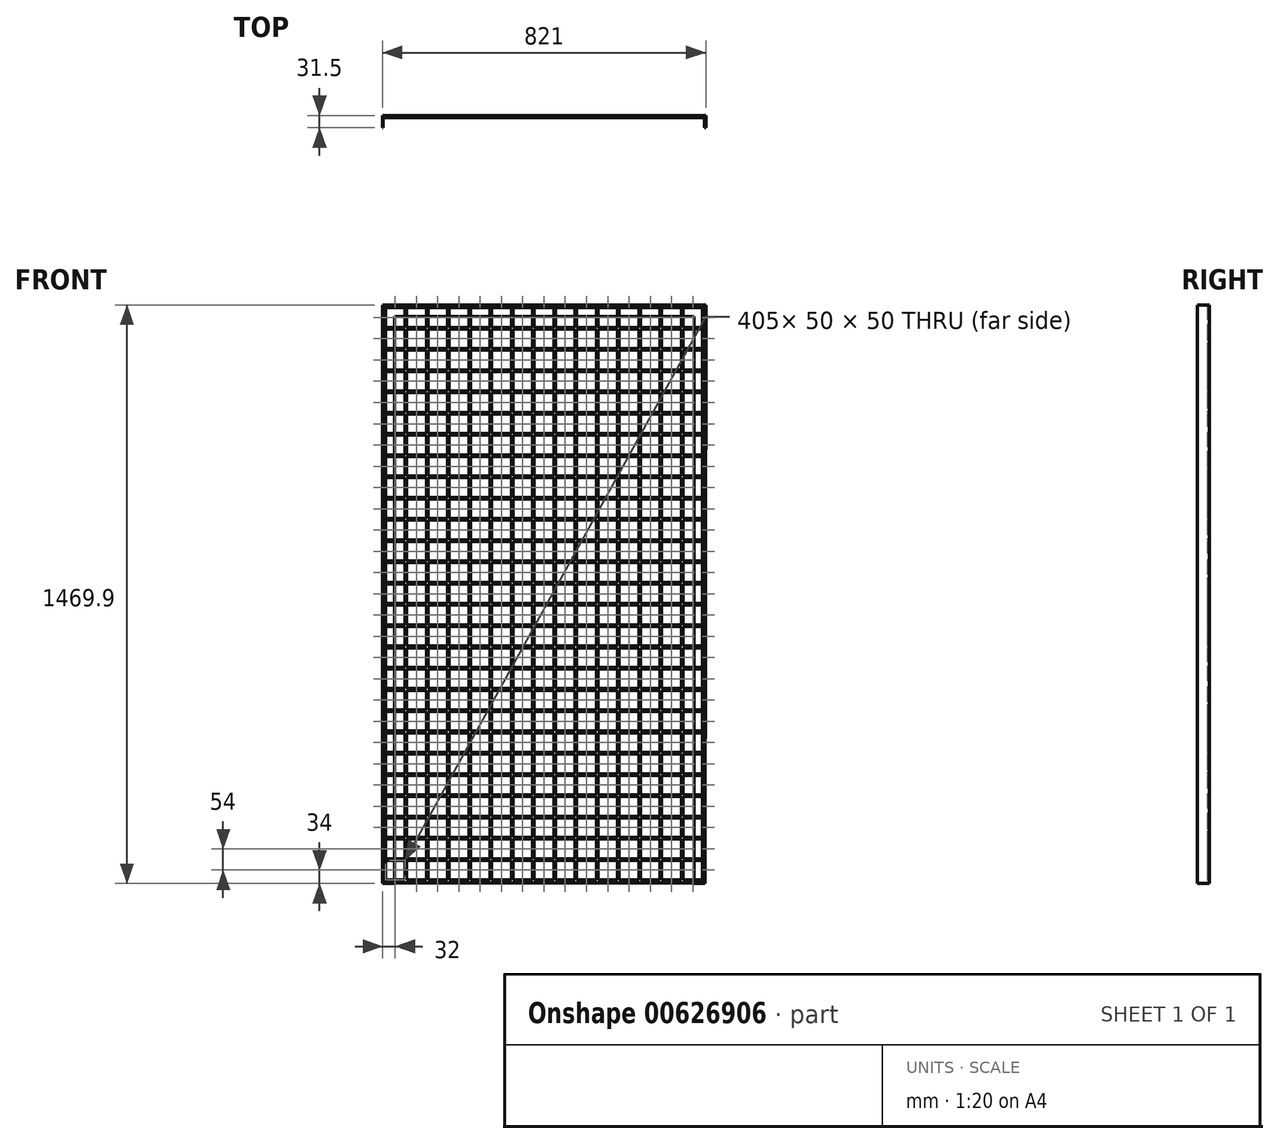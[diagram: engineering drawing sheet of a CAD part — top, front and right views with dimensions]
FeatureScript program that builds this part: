
annotation { "Feature Type Name" : "Feature", "Feature Type Description" : "" }
export const myFeature = defineFeature(function(context is Context, id is Id, definition is map)
    precondition{}
    {
        {
            var Q0;
            Q0=qCreatedBy(makeId("Front.planeOp"),FACE);
            var sketch = newSketch(context, id + "F0", { "sketchPlane" : qUnion([Q0])});
            skLineSegment(sketch, "E0.bottom", {"start": v(0, 0) * mm, "end": v(815, 0) * mm});
            skLineSegment(sketch, "E0.top", {"start": v(0, -1465) * mm, "end": v(815, -1465) * mm});
            skLineSegment(sketch, "E0.left", {"start": v(0, 0) * mm, "end": v(0, -1465) * mm});
            skLineSegment(sketch, "E0.right", {"start": v(815, 0) * mm, "end": v(815, -1465) * mm});
            skLineSegment(sketch, "E1.bottom", {"start": v(4, -4) * mm, "end": v(54, -4) * mm});
            skLineSegment(sketch, "E1.top", {"start": v(4, -54) * mm, "end": v(54, -54) * mm});
            skLineSegment(sketch, "E1.left", {"start": v(4, -4) * mm, "end": v(4, -54) * mm});
            skLineSegment(sketch, "E1.right", {"start": v(54, -4) * mm, "end": v(54, -54) * mm});
            skLineSegment(sketch, "E2.0.1.0", {"start": v(4, -58) * mm, "end": v(54, -58) * mm});
            skLineSegment(sketch, "E2.0.1.1", {"start": v(54, -58) * mm, "end": v(54, -108) * mm});
            skLineSegment(sketch, "E2.0.1.2", {"start": v(4, -108) * mm, "end": v(54, -108) * mm});
            skLineSegment(sketch, "E2.0.1.3", {"start": v(4, -58) * mm, "end": v(4, -108) * mm});
            skLineSegment(sketch, "E2.0.2.0", {"start": v(4, -112) * mm, "end": v(54, -112) * mm});
            skLineSegment(sketch, "E2.0.2.1", {"start": v(54, -112) * mm, "end": v(54, -162) * mm});
            skLineSegment(sketch, "E2.0.2.2", {"start": v(4, -162) * mm, "end": v(54, -162) * mm});
            skLineSegment(sketch, "E2.0.2.3", {"start": v(4, -112) * mm, "end": v(4, -162) * mm});
            skLineSegment(sketch, "E2.0.3.0", {"start": v(4, -166) * mm, "end": v(54, -166) * mm});
            skLineSegment(sketch, "E2.0.3.1", {"start": v(54, -166) * mm, "end": v(54, -216) * mm});
            skLineSegment(sketch, "E2.0.3.2", {"start": v(4, -216) * mm, "end": v(54, -216) * mm});
            skLineSegment(sketch, "E2.0.3.3", {"start": v(4, -166) * mm, "end": v(4, -216) * mm});
            skLineSegment(sketch, "E2.0.4.0", {"start": v(4, -220) * mm, "end": v(54, -220) * mm});
            skLineSegment(sketch, "E2.0.4.1", {"start": v(54, -220) * mm, "end": v(54, -270) * mm});
            skLineSegment(sketch, "E2.0.4.2", {"start": v(4, -270) * mm, "end": v(54, -270) * mm});
            skLineSegment(sketch, "E2.0.4.3", {"start": v(4, -220) * mm, "end": v(4, -270) * mm});
            skLineSegment(sketch, "E2.0.5.0", {"start": v(4, -274) * mm, "end": v(54, -274) * mm});
            skLineSegment(sketch, "E2.0.5.1", {"start": v(54, -274) * mm, "end": v(54, -324) * mm});
            skLineSegment(sketch, "E2.0.5.2", {"start": v(4, -324) * mm, "end": v(54, -324) * mm});
            skLineSegment(sketch, "E2.0.5.3", {"start": v(4, -274) * mm, "end": v(4, -324) * mm});
            skLineSegment(sketch, "E2.0.6.0", {"start": v(4, -328) * mm, "end": v(54, -328) * mm});
            skLineSegment(sketch, "E2.0.6.1", {"start": v(54, -328) * mm, "end": v(54, -378) * mm});
            skLineSegment(sketch, "E2.0.6.2", {"start": v(4, -378) * mm, "end": v(54, -378) * mm});
            skLineSegment(sketch, "E2.0.6.3", {"start": v(4, -328) * mm, "end": v(4, -378) * mm});
            skLineSegment(sketch, "E2.0.7.0", {"start": v(4, -382) * mm, "end": v(54, -382) * mm});
            skLineSegment(sketch, "E2.0.7.1", {"start": v(54, -382) * mm, "end": v(54, -432) * mm});
            skLineSegment(sketch, "E2.0.7.2", {"start": v(4, -432) * mm, "end": v(54, -432) * mm});
            skLineSegment(sketch, "E2.0.7.3", {"start": v(4, -382) * mm, "end": v(4, -432) * mm});
            skLineSegment(sketch, "E2.0.8.0", {"start": v(4, -436) * mm, "end": v(54, -436) * mm});
            skLineSegment(sketch, "E2.0.8.1", {"start": v(54, -436) * mm, "end": v(54, -486) * mm});
            skLineSegment(sketch, "E2.0.8.2", {"start": v(4, -486) * mm, "end": v(54, -486) * mm});
            skLineSegment(sketch, "E2.0.8.3", {"start": v(4, -436) * mm, "end": v(4, -486) * mm});
            skLineSegment(sketch, "E2.0.9.0", {"start": v(4, -490) * mm, "end": v(54, -490) * mm});
            skLineSegment(sketch, "E2.0.9.1", {"start": v(54, -490) * mm, "end": v(54, -540) * mm});
            skLineSegment(sketch, "E2.0.9.2", {"start": v(4, -540) * mm, "end": v(54, -540) * mm});
            skLineSegment(sketch, "E2.0.9.3", {"start": v(4, -490) * mm, "end": v(4, -540) * mm});
            skLineSegment(sketch, "E2.0.10.0", {"start": v(4, -544) * mm, "end": v(54, -544) * mm});
            skLineSegment(sketch, "E2.0.10.1", {"start": v(54, -544) * mm, "end": v(54, -594) * mm});
            skLineSegment(sketch, "E2.0.10.2", {"start": v(4, -594) * mm, "end": v(54, -594) * mm});
            skLineSegment(sketch, "E2.0.10.3", {"start": v(4, -544) * mm, "end": v(4, -594) * mm});
            skLineSegment(sketch, "E2.0.11.0", {"start": v(4, -598) * mm, "end": v(54, -598) * mm});
            skLineSegment(sketch, "E2.0.11.1", {"start": v(54, -598) * mm, "end": v(54, -648) * mm});
            skLineSegment(sketch, "E2.0.11.2", {"start": v(4, -648) * mm, "end": v(54, -648) * mm});
            skLineSegment(sketch, "E2.0.11.3", {"start": v(4, -598) * mm, "end": v(4, -648) * mm});
            skLineSegment(sketch, "E2.0.12.0", {"start": v(4, -652) * mm, "end": v(54, -652) * mm});
            skLineSegment(sketch, "E2.0.12.1", {"start": v(54, -652) * mm, "end": v(54, -702) * mm});
            skLineSegment(sketch, "E2.0.12.2", {"start": v(4, -702) * mm, "end": v(54, -702) * mm});
            skLineSegment(sketch, "E2.0.12.3", {"start": v(4, -652) * mm, "end": v(4, -702) * mm});
            skLineSegment(sketch, "E2.0.13.0", {"start": v(4, -706) * mm, "end": v(54, -706) * mm});
            skLineSegment(sketch, "E2.0.13.1", {"start": v(54, -706) * mm, "end": v(54, -756) * mm});
            skLineSegment(sketch, "E2.0.13.2", {"start": v(4, -756) * mm, "end": v(54, -756) * mm});
            skLineSegment(sketch, "E2.0.13.3", {"start": v(4, -706) * mm, "end": v(4, -756) * mm});
            skLineSegment(sketch, "E2.0.14.0", {"start": v(4, -760) * mm, "end": v(54, -760) * mm});
            skLineSegment(sketch, "E2.0.14.1", {"start": v(54, -760) * mm, "end": v(54, -810) * mm});
            skLineSegment(sketch, "E2.0.14.2", {"start": v(4, -810) * mm, "end": v(54, -810) * mm});
            skLineSegment(sketch, "E2.0.14.3", {"start": v(4, -760) * mm, "end": v(4, -810) * mm});
            skLineSegment(sketch, "E2.0.15.0", {"start": v(4, -814) * mm, "end": v(54, -814) * mm});
            skLineSegment(sketch, "E2.0.15.1", {"start": v(54, -814) * mm, "end": v(54, -864) * mm});
            skLineSegment(sketch, "E2.0.15.2", {"start": v(4, -864) * mm, "end": v(54, -864) * mm});
            skLineSegment(sketch, "E2.0.15.3", {"start": v(4, -814) * mm, "end": v(4, -864) * mm});
            skLineSegment(sketch, "E2.0.16.0", {"start": v(4, -868) * mm, "end": v(54, -868) * mm});
            skLineSegment(sketch, "E2.0.16.1", {"start": v(54, -868) * mm, "end": v(54, -918) * mm});
            skLineSegment(sketch, "E2.0.16.2", {"start": v(4, -918) * mm, "end": v(54, -918) * mm});
            skLineSegment(sketch, "E2.0.16.3", {"start": v(4, -868) * mm, "end": v(4, -918) * mm});
            skLineSegment(sketch, "E2.0.17.0", {"start": v(4, -922) * mm, "end": v(54, -922) * mm});
            skLineSegment(sketch, "E2.0.17.1", {"start": v(54, -922) * mm, "end": v(54, -972) * mm});
            skLineSegment(sketch, "E2.0.17.2", {"start": v(4, -972) * mm, "end": v(54, -972) * mm});
            skLineSegment(sketch, "E2.0.17.3", {"start": v(4, -922) * mm, "end": v(4, -972) * mm});
            skLineSegment(sketch, "E2.0.18.0", {"start": v(4, -976) * mm, "end": v(54, -976) * mm});
            skLineSegment(sketch, "E2.0.18.1", {"start": v(54, -976) * mm, "end": v(54, -1026) * mm});
            skLineSegment(sketch, "E2.0.18.2", {"start": v(4, -1026) * mm, "end": v(54, -1026) * mm});
            skLineSegment(sketch, "E2.0.18.3", {"start": v(4, -976) * mm, "end": v(4, -1026) * mm});
            skLineSegment(sketch, "E2.0.19.0", {"start": v(4, -1030) * mm, "end": v(54, -1030) * mm});
            skLineSegment(sketch, "E2.0.19.1", {"start": v(54, -1030) * mm, "end": v(54, -1080) * mm});
            skLineSegment(sketch, "E2.0.19.2", {"start": v(4, -1080) * mm, "end": v(54, -1080) * mm});
            skLineSegment(sketch, "E2.0.19.3", {"start": v(4, -1030) * mm, "end": v(4, -1080) * mm});
            skLineSegment(sketch, "E2.0.20.0", {"start": v(4, -1084) * mm, "end": v(54, -1084) * mm});
            skLineSegment(sketch, "E2.0.20.1", {"start": v(54, -1084) * mm, "end": v(54, -1134) * mm});
            skLineSegment(sketch, "E2.0.20.2", {"start": v(4, -1134) * mm, "end": v(54, -1134) * mm});
            skLineSegment(sketch, "E2.0.20.3", {"start": v(4, -1084) * mm, "end": v(4, -1134) * mm});
            skLineSegment(sketch, "E2.0.21.0", {"start": v(4, -1138) * mm, "end": v(54, -1138) * mm});
            skLineSegment(sketch, "E2.0.21.1", {"start": v(54, -1138) * mm, "end": v(54, -1188) * mm});
            skLineSegment(sketch, "E2.0.21.2", {"start": v(4, -1188) * mm, "end": v(54, -1188) * mm});
            skLineSegment(sketch, "E2.0.21.3", {"start": v(4, -1138) * mm, "end": v(4, -1188) * mm});
            skLineSegment(sketch, "E2.0.22.0", {"start": v(4, -1192) * mm, "end": v(54, -1192) * mm});
            skLineSegment(sketch, "E2.0.22.1", {"start": v(54, -1192) * mm, "end": v(54, -1242) * mm});
            skLineSegment(sketch, "E2.0.22.2", {"start": v(4, -1242) * mm, "end": v(54, -1242) * mm});
            skLineSegment(sketch, "E2.0.22.3", {"start": v(4, -1192) * mm, "end": v(4, -1242) * mm});
            skLineSegment(sketch, "E2.0.23.0", {"start": v(4, -1246) * mm, "end": v(54, -1246) * mm});
            skLineSegment(sketch, "E2.0.23.1", {"start": v(54, -1246) * mm, "end": v(54, -1296) * mm});
            skLineSegment(sketch, "E2.0.23.2", {"start": v(4, -1296) * mm, "end": v(54, -1296) * mm});
            skLineSegment(sketch, "E2.0.23.3", {"start": v(4, -1246) * mm, "end": v(4, -1296) * mm});
            skLineSegment(sketch, "E2.0.24.0", {"start": v(4, -1300) * mm, "end": v(54, -1300) * mm});
            skLineSegment(sketch, "E2.0.24.1", {"start": v(54, -1300) * mm, "end": v(54, -1350) * mm});
            skLineSegment(sketch, "E2.0.24.2", {"start": v(4, -1350) * mm, "end": v(54, -1350) * mm});
            skLineSegment(sketch, "E2.0.24.3", {"start": v(4, -1300) * mm, "end": v(4, -1350) * mm});
            skLineSegment(sketch, "E2.1.0.0", {"start": v(58, -4) * mm, "end": v(108, -4) * mm});
            skLineSegment(sketch, "E2.1.0.1", {"start": v(108, -4) * mm, "end": v(108, -54) * mm});
            skLineSegment(sketch, "E2.1.0.2", {"start": v(58, -54) * mm, "end": v(108, -54) * mm});
            skLineSegment(sketch, "E2.1.0.3", {"start": v(58, -4) * mm, "end": v(58, -54) * mm});
            skLineSegment(sketch, "E2.1.1.0", {"start": v(58, -58) * mm, "end": v(108, -58) * mm});
            skLineSegment(sketch, "E2.1.1.1", {"start": v(108, -58) * mm, "end": v(108, -108) * mm});
            skLineSegment(sketch, "E2.1.1.2", {"start": v(58, -108) * mm, "end": v(108, -108) * mm});
            skLineSegment(sketch, "E2.1.1.3", {"start": v(58, -58) * mm, "end": v(58, -108) * mm});
            skLineSegment(sketch, "E2.1.2.0", {"start": v(58, -112) * mm, "end": v(108, -112) * mm});
            skLineSegment(sketch, "E2.1.2.1", {"start": v(108, -112) * mm, "end": v(108, -162) * mm});
            skLineSegment(sketch, "E2.1.2.2", {"start": v(58, -162) * mm, "end": v(108, -162) * mm});
            skLineSegment(sketch, "E2.1.2.3", {"start": v(58, -112) * mm, "end": v(58, -162) * mm});
            skLineSegment(sketch, "E2.1.3.0", {"start": v(58, -166) * mm, "end": v(108, -166) * mm});
            skLineSegment(sketch, "E2.1.3.1", {"start": v(108, -166) * mm, "end": v(108, -216) * mm});
            skLineSegment(sketch, "E2.1.3.2", {"start": v(58, -216) * mm, "end": v(108, -216) * mm});
            skLineSegment(sketch, "E2.1.3.3", {"start": v(58, -166) * mm, "end": v(58, -216) * mm});
            skLineSegment(sketch, "E2.1.4.0", {"start": v(58, -220) * mm, "end": v(108, -220) * mm});
            skLineSegment(sketch, "E2.1.4.1", {"start": v(108, -220) * mm, "end": v(108, -270) * mm});
            skLineSegment(sketch, "E2.1.4.2", {"start": v(58, -270) * mm, "end": v(108, -270) * mm});
            skLineSegment(sketch, "E2.1.4.3", {"start": v(58, -220) * mm, "end": v(58, -270) * mm});
            skLineSegment(sketch, "E2.1.5.0", {"start": v(58, -274) * mm, "end": v(108, -274) * mm});
            skLineSegment(sketch, "E2.1.5.1", {"start": v(108, -274) * mm, "end": v(108, -324) * mm});
            skLineSegment(sketch, "E2.1.5.2", {"start": v(58, -324) * mm, "end": v(108, -324) * mm});
            skLineSegment(sketch, "E2.1.5.3", {"start": v(58, -274) * mm, "end": v(58, -324) * mm});
            skLineSegment(sketch, "E2.1.6.0", {"start": v(58, -328) * mm, "end": v(108, -328) * mm});
            skLineSegment(sketch, "E2.1.6.1", {"start": v(108, -328) * mm, "end": v(108, -378) * mm});
            skLineSegment(sketch, "E2.1.6.2", {"start": v(58, -378) * mm, "end": v(108, -378) * mm});
            skLineSegment(sketch, "E2.1.6.3", {"start": v(58, -328) * mm, "end": v(58, -378) * mm});
            skLineSegment(sketch, "E2.1.7.0", {"start": v(58, -382) * mm, "end": v(108, -382) * mm});
            skLineSegment(sketch, "E2.1.7.1", {"start": v(108, -382) * mm, "end": v(108, -432) * mm});
            skLineSegment(sketch, "E2.1.7.2", {"start": v(58, -432) * mm, "end": v(108, -432) * mm});
            skLineSegment(sketch, "E2.1.7.3", {"start": v(58, -382) * mm, "end": v(58, -432) * mm});
            skLineSegment(sketch, "E2.1.8.0", {"start": v(58, -436) * mm, "end": v(108, -436) * mm});
            skLineSegment(sketch, "E2.1.8.1", {"start": v(108, -436) * mm, "end": v(108, -486) * mm});
            skLineSegment(sketch, "E2.1.8.2", {"start": v(58, -486) * mm, "end": v(108, -486) * mm});
            skLineSegment(sketch, "E2.1.8.3", {"start": v(58, -436) * mm, "end": v(58, -486) * mm});
            skLineSegment(sketch, "E2.1.9.0", {"start": v(58, -490) * mm, "end": v(108, -490) * mm});
            skLineSegment(sketch, "E2.1.9.1", {"start": v(108, -490) * mm, "end": v(108, -540) * mm});
            skLineSegment(sketch, "E2.1.9.2", {"start": v(58, -540) * mm, "end": v(108, -540) * mm});
            skLineSegment(sketch, "E2.1.9.3", {"start": v(58, -490) * mm, "end": v(58, -540) * mm});
            skLineSegment(sketch, "E2.1.10.0", {"start": v(58, -544) * mm, "end": v(108, -544) * mm});
            skLineSegment(sketch, "E2.1.10.1", {"start": v(108, -544) * mm, "end": v(108, -594) * mm});
            skLineSegment(sketch, "E2.1.10.2", {"start": v(58, -594) * mm, "end": v(108, -594) * mm});
            skLineSegment(sketch, "E2.1.10.3", {"start": v(58, -544) * mm, "end": v(58, -594) * mm});
            skLineSegment(sketch, "E2.1.11.0", {"start": v(58, -598) * mm, "end": v(108, -598) * mm});
            skLineSegment(sketch, "E2.1.11.1", {"start": v(108, -598) * mm, "end": v(108, -648) * mm});
            skLineSegment(sketch, "E2.1.11.2", {"start": v(58, -648) * mm, "end": v(108, -648) * mm});
            skLineSegment(sketch, "E2.1.11.3", {"start": v(58, -598) * mm, "end": v(58, -648) * mm});
            skLineSegment(sketch, "E2.1.12.0", {"start": v(58, -652) * mm, "end": v(108, -652) * mm});
            skLineSegment(sketch, "E2.1.12.1", {"start": v(108, -652) * mm, "end": v(108, -702) * mm});
            skLineSegment(sketch, "E2.1.12.2", {"start": v(58, -702) * mm, "end": v(108, -702) * mm});
            skLineSegment(sketch, "E2.1.12.3", {"start": v(58, -652) * mm, "end": v(58, -702) * mm});
            skLineSegment(sketch, "E2.1.13.0", {"start": v(58, -706) * mm, "end": v(108, -706) * mm});
            skLineSegment(sketch, "E2.1.13.1", {"start": v(108, -706) * mm, "end": v(108, -756) * mm});
            skLineSegment(sketch, "E2.1.13.2", {"start": v(58, -756) * mm, "end": v(108, -756) * mm});
            skLineSegment(sketch, "E2.1.13.3", {"start": v(58, -706) * mm, "end": v(58, -756) * mm});
            skLineSegment(sketch, "E2.1.14.0", {"start": v(58, -760) * mm, "end": v(108, -760) * mm});
            skLineSegment(sketch, "E2.1.14.1", {"start": v(108, -760) * mm, "end": v(108, -810) * mm});
            skLineSegment(sketch, "E2.1.14.2", {"start": v(58, -810) * mm, "end": v(108, -810) * mm});
            skLineSegment(sketch, "E2.1.14.3", {"start": v(58, -760) * mm, "end": v(58, -810) * mm});
            skLineSegment(sketch, "E2.1.15.0", {"start": v(58, -814) * mm, "end": v(108, -814) * mm});
            skLineSegment(sketch, "E2.1.15.1", {"start": v(108, -814) * mm, "end": v(108, -864) * mm});
            skLineSegment(sketch, "E2.1.15.2", {"start": v(58, -864) * mm, "end": v(108, -864) * mm});
            skLineSegment(sketch, "E2.1.15.3", {"start": v(58, -814) * mm, "end": v(58, -864) * mm});
            skLineSegment(sketch, "E2.1.16.0", {"start": v(58, -868) * mm, "end": v(108, -868) * mm});
            skLineSegment(sketch, "E2.1.16.1", {"start": v(108, -868) * mm, "end": v(108, -918) * mm});
            skLineSegment(sketch, "E2.1.16.2", {"start": v(58, -918) * mm, "end": v(108, -918) * mm});
            skLineSegment(sketch, "E2.1.16.3", {"start": v(58, -868) * mm, "end": v(58, -918) * mm});
            skLineSegment(sketch, "E2.1.17.0", {"start": v(58, -922) * mm, "end": v(108, -922) * mm});
            skLineSegment(sketch, "E2.1.17.1", {"start": v(108, -922) * mm, "end": v(108, -972) * mm});
            skLineSegment(sketch, "E2.1.17.2", {"start": v(58, -972) * mm, "end": v(108, -972) * mm});
            skLineSegment(sketch, "E2.1.17.3", {"start": v(58, -922) * mm, "end": v(58, -972) * mm});
            skLineSegment(sketch, "E2.1.18.0", {"start": v(58, -976) * mm, "end": v(108, -976) * mm});
            skLineSegment(sketch, "E2.1.18.1", {"start": v(108, -976) * mm, "end": v(108, -1026) * mm});
            skLineSegment(sketch, "E2.1.18.2", {"start": v(58, -1026) * mm, "end": v(108, -1026) * mm});
            skLineSegment(sketch, "E2.1.18.3", {"start": v(58, -976) * mm, "end": v(58, -1026) * mm});
            skLineSegment(sketch, "E2.1.19.0", {"start": v(58, -1030) * mm, "end": v(108, -1030) * mm});
            skLineSegment(sketch, "E2.1.19.1", {"start": v(108, -1030) * mm, "end": v(108, -1080) * mm});
            skLineSegment(sketch, "E2.1.19.2", {"start": v(58, -1080) * mm, "end": v(108, -1080) * mm});
            skLineSegment(sketch, "E2.1.19.3", {"start": v(58, -1030) * mm, "end": v(58, -1080) * mm});
            skLineSegment(sketch, "E2.1.20.0", {"start": v(58, -1084) * mm, "end": v(108, -1084) * mm});
            skLineSegment(sketch, "E2.1.20.1", {"start": v(108, -1084) * mm, "end": v(108, -1134) * mm});
            skLineSegment(sketch, "E2.1.20.2", {"start": v(58, -1134) * mm, "end": v(108, -1134) * mm});
            skLineSegment(sketch, "E2.1.20.3", {"start": v(58, -1084) * mm, "end": v(58, -1134) * mm});
            skLineSegment(sketch, "E2.1.21.0", {"start": v(58, -1138) * mm, "end": v(108, -1138) * mm});
            skLineSegment(sketch, "E2.1.21.1", {"start": v(108, -1138) * mm, "end": v(108, -1188) * mm});
            skLineSegment(sketch, "E2.1.21.2", {"start": v(58, -1188) * mm, "end": v(108, -1188) * mm});
            skLineSegment(sketch, "E2.1.21.3", {"start": v(58, -1138) * mm, "end": v(58, -1188) * mm});
            skLineSegment(sketch, "E2.1.22.0", {"start": v(58, -1192) * mm, "end": v(108, -1192) * mm});
            skLineSegment(sketch, "E2.1.22.1", {"start": v(108, -1192) * mm, "end": v(108, -1242) * mm});
            skLineSegment(sketch, "E2.1.22.2", {"start": v(58, -1242) * mm, "end": v(108, -1242) * mm});
            skLineSegment(sketch, "E2.1.22.3", {"start": v(58, -1192) * mm, "end": v(58, -1242) * mm});
            skLineSegment(sketch, "E2.1.23.0", {"start": v(58, -1246) * mm, "end": v(108, -1246) * mm});
            skLineSegment(sketch, "E2.1.23.1", {"start": v(108, -1246) * mm, "end": v(108, -1296) * mm});
            skLineSegment(sketch, "E2.1.23.2", {"start": v(58, -1296) * mm, "end": v(108, -1296) * mm});
            skLineSegment(sketch, "E2.1.23.3", {"start": v(58, -1246) * mm, "end": v(58, -1296) * mm});
            skLineSegment(sketch, "E2.1.24.0", {"start": v(58, -1300) * mm, "end": v(108, -1300) * mm});
            skLineSegment(sketch, "E2.1.24.1", {"start": v(108, -1300) * mm, "end": v(108, -1350) * mm});
            skLineSegment(sketch, "E2.1.24.2", {"start": v(58, -1350) * mm, "end": v(108, -1350) * mm});
            skLineSegment(sketch, "E2.1.24.3", {"start": v(58, -1300) * mm, "end": v(58, -1350) * mm});
            skLineSegment(sketch, "E2.2.0.0", {"start": v(112, -4) * mm, "end": v(162, -4) * mm});
            skLineSegment(sketch, "E2.2.0.1", {"start": v(162, -4) * mm, "end": v(162, -54) * mm});
            skLineSegment(sketch, "E2.2.0.2", {"start": v(112, -54) * mm, "end": v(162, -54) * mm});
            skLineSegment(sketch, "E2.2.0.3", {"start": v(112, -4) * mm, "end": v(112, -54) * mm});
            skLineSegment(sketch, "E2.2.1.0", {"start": v(112, -58) * mm, "end": v(162, -58) * mm});
            skLineSegment(sketch, "E2.2.1.1", {"start": v(162, -58) * mm, "end": v(162, -108) * mm});
            skLineSegment(sketch, "E2.2.1.2", {"start": v(112, -108) * mm, "end": v(162, -108) * mm});
            skLineSegment(sketch, "E2.2.1.3", {"start": v(112, -58) * mm, "end": v(112, -108) * mm});
            skLineSegment(sketch, "E2.2.2.0", {"start": v(112, -112) * mm, "end": v(162, -112) * mm});
            skLineSegment(sketch, "E2.2.2.1", {"start": v(162, -112) * mm, "end": v(162, -162) * mm});
            skLineSegment(sketch, "E2.2.2.2", {"start": v(112, -162) * mm, "end": v(162, -162) * mm});
            skLineSegment(sketch, "E2.2.2.3", {"start": v(112, -112) * mm, "end": v(112, -162) * mm});
            skLineSegment(sketch, "E2.2.3.0", {"start": v(112, -166) * mm, "end": v(162, -166) * mm});
            skLineSegment(sketch, "E2.2.3.1", {"start": v(162, -166) * mm, "end": v(162, -216) * mm});
            skLineSegment(sketch, "E2.2.3.2", {"start": v(112, -216) * mm, "end": v(162, -216) * mm});
            skLineSegment(sketch, "E2.2.3.3", {"start": v(112, -166) * mm, "end": v(112, -216) * mm});
            skLineSegment(sketch, "E2.2.4.0", {"start": v(112, -220) * mm, "end": v(162, -220) * mm});
            skLineSegment(sketch, "E2.2.4.1", {"start": v(162, -220) * mm, "end": v(162, -270) * mm});
            skLineSegment(sketch, "E2.2.4.2", {"start": v(112, -270) * mm, "end": v(162, -270) * mm});
            skLineSegment(sketch, "E2.2.4.3", {"start": v(112, -220) * mm, "end": v(112, -270) * mm});
            skLineSegment(sketch, "E2.2.5.0", {"start": v(112, -274) * mm, "end": v(162, -274) * mm});
            skLineSegment(sketch, "E2.2.5.1", {"start": v(162, -274) * mm, "end": v(162, -324) * mm});
            skLineSegment(sketch, "E2.2.5.2", {"start": v(112, -324) * mm, "end": v(162, -324) * mm});
            skLineSegment(sketch, "E2.2.5.3", {"start": v(112, -274) * mm, "end": v(112, -324) * mm});
            skLineSegment(sketch, "E2.2.6.0", {"start": v(112, -328) * mm, "end": v(162, -328) * mm});
            skLineSegment(sketch, "E2.2.6.1", {"start": v(162, -328) * mm, "end": v(162, -378) * mm});
            skLineSegment(sketch, "E2.2.6.2", {"start": v(112, -378) * mm, "end": v(162, -378) * mm});
            skLineSegment(sketch, "E2.2.6.3", {"start": v(112, -328) * mm, "end": v(112, -378) * mm});
            skLineSegment(sketch, "E2.2.7.0", {"start": v(112, -382) * mm, "end": v(162, -382) * mm});
            skLineSegment(sketch, "E2.2.7.1", {"start": v(162, -382) * mm, "end": v(162, -432) * mm});
            skLineSegment(sketch, "E2.2.7.2", {"start": v(112, -432) * mm, "end": v(162, -432) * mm});
            skLineSegment(sketch, "E2.2.7.3", {"start": v(112, -382) * mm, "end": v(112, -432) * mm});
            skLineSegment(sketch, "E2.2.8.0", {"start": v(112, -436) * mm, "end": v(162, -436) * mm});
            skLineSegment(sketch, "E2.2.8.1", {"start": v(162, -436) * mm, "end": v(162, -486) * mm});
            skLineSegment(sketch, "E2.2.8.2", {"start": v(112, -486) * mm, "end": v(162, -486) * mm});
            skLineSegment(sketch, "E2.2.8.3", {"start": v(112, -436) * mm, "end": v(112, -486) * mm});
            skLineSegment(sketch, "E2.2.9.0", {"start": v(112, -490) * mm, "end": v(162, -490) * mm});
            skLineSegment(sketch, "E2.2.9.1", {"start": v(162, -490) * mm, "end": v(162, -540) * mm});
            skLineSegment(sketch, "E2.2.9.2", {"start": v(112, -540) * mm, "end": v(162, -540) * mm});
            skLineSegment(sketch, "E2.2.9.3", {"start": v(112, -490) * mm, "end": v(112, -540) * mm});
            skLineSegment(sketch, "E2.2.10.0", {"start": v(112, -544) * mm, "end": v(162, -544) * mm});
            skLineSegment(sketch, "E2.2.10.1", {"start": v(162, -544) * mm, "end": v(162, -594) * mm});
            skLineSegment(sketch, "E2.2.10.2", {"start": v(112, -594) * mm, "end": v(162, -594) * mm});
            skLineSegment(sketch, "E2.2.10.3", {"start": v(112, -544) * mm, "end": v(112, -594) * mm});
            skLineSegment(sketch, "E2.2.11.0", {"start": v(112, -598) * mm, "end": v(162, -598) * mm});
            skLineSegment(sketch, "E2.2.11.1", {"start": v(162, -598) * mm, "end": v(162, -648) * mm});
            skLineSegment(sketch, "E2.2.11.2", {"start": v(112, -648) * mm, "end": v(162, -648) * mm});
            skLineSegment(sketch, "E2.2.11.3", {"start": v(112, -598) * mm, "end": v(112, -648) * mm});
            skLineSegment(sketch, "E2.2.12.0", {"start": v(112, -652) * mm, "end": v(162, -652) * mm});
            skLineSegment(sketch, "E2.2.12.1", {"start": v(162, -652) * mm, "end": v(162, -702) * mm});
            skLineSegment(sketch, "E2.2.12.2", {"start": v(112, -702) * mm, "end": v(162, -702) * mm});
            skLineSegment(sketch, "E2.2.12.3", {"start": v(112, -652) * mm, "end": v(112, -702) * mm});
            skLineSegment(sketch, "E2.2.13.0", {"start": v(112, -706) * mm, "end": v(162, -706) * mm});
            skLineSegment(sketch, "E2.2.13.1", {"start": v(162, -706) * mm, "end": v(162, -756) * mm});
            skLineSegment(sketch, "E2.2.13.2", {"start": v(112, -756) * mm, "end": v(162, -756) * mm});
            skLineSegment(sketch, "E2.2.13.3", {"start": v(112, -706) * mm, "end": v(112, -756) * mm});
            skLineSegment(sketch, "E2.2.14.0", {"start": v(112, -760) * mm, "end": v(162, -760) * mm});
            skLineSegment(sketch, "E2.2.14.1", {"start": v(162, -760) * mm, "end": v(162, -810) * mm});
            skLineSegment(sketch, "E2.2.14.2", {"start": v(112, -810) * mm, "end": v(162, -810) * mm});
            skLineSegment(sketch, "E2.2.14.3", {"start": v(112, -760) * mm, "end": v(112, -810) * mm});
            skLineSegment(sketch, "E2.2.15.0", {"start": v(112, -814) * mm, "end": v(162, -814) * mm});
            skLineSegment(sketch, "E2.2.15.1", {"start": v(162, -814) * mm, "end": v(162, -864) * mm});
            skLineSegment(sketch, "E2.2.15.2", {"start": v(112, -864) * mm, "end": v(162, -864) * mm});
            skLineSegment(sketch, "E2.2.15.3", {"start": v(112, -814) * mm, "end": v(112, -864) * mm});
            skLineSegment(sketch, "E2.2.16.0", {"start": v(112, -868) * mm, "end": v(162, -868) * mm});
            skLineSegment(sketch, "E2.2.16.1", {"start": v(162, -868) * mm, "end": v(162, -918) * mm});
            skLineSegment(sketch, "E2.2.16.2", {"start": v(112, -918) * mm, "end": v(162, -918) * mm});
            skLineSegment(sketch, "E2.2.16.3", {"start": v(112, -868) * mm, "end": v(112, -918) * mm});
            skLineSegment(sketch, "E2.2.17.0", {"start": v(112, -922) * mm, "end": v(162, -922) * mm});
            skLineSegment(sketch, "E2.2.17.1", {"start": v(162, -922) * mm, "end": v(162, -972) * mm});
            skLineSegment(sketch, "E2.2.17.2", {"start": v(112, -972) * mm, "end": v(162, -972) * mm});
            skLineSegment(sketch, "E2.2.17.3", {"start": v(112, -922) * mm, "end": v(112, -972) * mm});
            skLineSegment(sketch, "E2.2.18.0", {"start": v(112, -976) * mm, "end": v(162, -976) * mm});
            skLineSegment(sketch, "E2.2.18.1", {"start": v(162, -976) * mm, "end": v(162, -1026) * mm});
            skLineSegment(sketch, "E2.2.18.2", {"start": v(112, -1026) * mm, "end": v(162, -1026) * mm});
            skLineSegment(sketch, "E2.2.18.3", {"start": v(112, -976) * mm, "end": v(112, -1026) * mm});
            skLineSegment(sketch, "E2.2.19.0", {"start": v(112, -1030) * mm, "end": v(162, -1030) * mm});
            skLineSegment(sketch, "E2.2.19.1", {"start": v(162, -1030) * mm, "end": v(162, -1080) * mm});
            skLineSegment(sketch, "E2.2.19.2", {"start": v(112, -1080) * mm, "end": v(162, -1080) * mm});
            skLineSegment(sketch, "E2.2.19.3", {"start": v(112, -1030) * mm, "end": v(112, -1080) * mm});
            skLineSegment(sketch, "E2.2.20.0", {"start": v(112, -1084) * mm, "end": v(162, -1084) * mm});
            skLineSegment(sketch, "E2.2.20.1", {"start": v(162, -1084) * mm, "end": v(162, -1134) * mm});
            skLineSegment(sketch, "E2.2.20.2", {"start": v(112, -1134) * mm, "end": v(162, -1134) * mm});
            skLineSegment(sketch, "E2.2.20.3", {"start": v(112, -1084) * mm, "end": v(112, -1134) * mm});
            skLineSegment(sketch, "E2.2.21.0", {"start": v(112, -1138) * mm, "end": v(162, -1138) * mm});
            skLineSegment(sketch, "E2.2.21.1", {"start": v(162, -1138) * mm, "end": v(162, -1188) * mm});
            skLineSegment(sketch, "E2.2.21.2", {"start": v(112, -1188) * mm, "end": v(162, -1188) * mm});
            skLineSegment(sketch, "E2.2.21.3", {"start": v(112, -1138) * mm, "end": v(112, -1188) * mm});
            skLineSegment(sketch, "E2.2.22.0", {"start": v(112, -1192) * mm, "end": v(162, -1192) * mm});
            skLineSegment(sketch, "E2.2.22.1", {"start": v(162, -1192) * mm, "end": v(162, -1242) * mm});
            skLineSegment(sketch, "E2.2.22.2", {"start": v(112, -1242) * mm, "end": v(162, -1242) * mm});
            skLineSegment(sketch, "E2.2.22.3", {"start": v(112, -1192) * mm, "end": v(112, -1242) * mm});
            skLineSegment(sketch, "E2.2.23.0", {"start": v(112, -1246) * mm, "end": v(162, -1246) * mm});
            skLineSegment(sketch, "E2.2.23.1", {"start": v(162, -1246) * mm, "end": v(162, -1296) * mm});
            skLineSegment(sketch, "E2.2.23.2", {"start": v(112, -1296) * mm, "end": v(162, -1296) * mm});
            skLineSegment(sketch, "E2.2.23.3", {"start": v(112, -1246) * mm, "end": v(112, -1296) * mm});
            skLineSegment(sketch, "E2.2.24.0", {"start": v(112, -1300) * mm, "end": v(162, -1300) * mm});
            skLineSegment(sketch, "E2.2.24.1", {"start": v(162, -1300) * mm, "end": v(162, -1350) * mm});
            skLineSegment(sketch, "E2.2.24.2", {"start": v(112, -1350) * mm, "end": v(162, -1350) * mm});
            skLineSegment(sketch, "E2.2.24.3", {"start": v(112, -1300) * mm, "end": v(112, -1350) * mm});
            skLineSegment(sketch, "E2.3.0.0", {"start": v(166, -4) * mm, "end": v(216, -4) * mm});
            skLineSegment(sketch, "E2.3.0.1", {"start": v(216, -4) * mm, "end": v(216, -54) * mm});
            skLineSegment(sketch, "E2.3.0.2", {"start": v(166, -54) * mm, "end": v(216, -54) * mm});
            skLineSegment(sketch, "E2.3.0.3", {"start": v(166, -4) * mm, "end": v(166, -54) * mm});
            skLineSegment(sketch, "E2.3.1.0", {"start": v(166, -58) * mm, "end": v(216, -58) * mm});
            skLineSegment(sketch, "E2.3.1.1", {"start": v(216, -58) * mm, "end": v(216, -108) * mm});
            skLineSegment(sketch, "E2.3.1.2", {"start": v(166, -108) * mm, "end": v(216, -108) * mm});
            skLineSegment(sketch, "E2.3.1.3", {"start": v(166, -58) * mm, "end": v(166, -108) * mm});
            skLineSegment(sketch, "E2.3.2.0", {"start": v(166, -112) * mm, "end": v(216, -112) * mm});
            skLineSegment(sketch, "E2.3.2.1", {"start": v(216, -112) * mm, "end": v(216, -162) * mm});
            skLineSegment(sketch, "E2.3.2.2", {"start": v(166, -162) * mm, "end": v(216, -162) * mm});
            skLineSegment(sketch, "E2.3.2.3", {"start": v(166, -112) * mm, "end": v(166, -162) * mm});
            skLineSegment(sketch, "E2.3.3.0", {"start": v(166, -166) * mm, "end": v(216, -166) * mm});
            skLineSegment(sketch, "E2.3.3.1", {"start": v(216, -166) * mm, "end": v(216, -216) * mm});
            skLineSegment(sketch, "E2.3.3.2", {"start": v(166, -216) * mm, "end": v(216, -216) * mm});
            skLineSegment(sketch, "E2.3.3.3", {"start": v(166, -166) * mm, "end": v(166, -216) * mm});
            skLineSegment(sketch, "E2.3.4.0", {"start": v(166, -220) * mm, "end": v(216, -220) * mm});
            skLineSegment(sketch, "E2.3.4.1", {"start": v(216, -220) * mm, "end": v(216, -270) * mm});
            skLineSegment(sketch, "E2.3.4.2", {"start": v(166, -270) * mm, "end": v(216, -270) * mm});
            skLineSegment(sketch, "E2.3.4.3", {"start": v(166, -220) * mm, "end": v(166, -270) * mm});
            skLineSegment(sketch, "E2.3.5.0", {"start": v(166, -274) * mm, "end": v(216, -274) * mm});
            skLineSegment(sketch, "E2.3.5.1", {"start": v(216, -274) * mm, "end": v(216, -324) * mm});
            skLineSegment(sketch, "E2.3.5.2", {"start": v(166, -324) * mm, "end": v(216, -324) * mm});
            skLineSegment(sketch, "E2.3.5.3", {"start": v(166, -274) * mm, "end": v(166, -324) * mm});
            skLineSegment(sketch, "E2.3.6.0", {"start": v(166, -328) * mm, "end": v(216, -328) * mm});
            skLineSegment(sketch, "E2.3.6.1", {"start": v(216, -328) * mm, "end": v(216, -378) * mm});
            skLineSegment(sketch, "E2.3.6.2", {"start": v(166, -378) * mm, "end": v(216, -378) * mm});
            skLineSegment(sketch, "E2.3.6.3", {"start": v(166, -328) * mm, "end": v(166, -378) * mm});
            skLineSegment(sketch, "E2.3.7.0", {"start": v(166, -382) * mm, "end": v(216, -382) * mm});
            skLineSegment(sketch, "E2.3.7.1", {"start": v(216, -382) * mm, "end": v(216, -432) * mm});
            skLineSegment(sketch, "E2.3.7.2", {"start": v(166, -432) * mm, "end": v(216, -432) * mm});
            skLineSegment(sketch, "E2.3.7.3", {"start": v(166, -382) * mm, "end": v(166, -432) * mm});
            skLineSegment(sketch, "E2.3.8.0", {"start": v(166, -436) * mm, "end": v(216, -436) * mm});
            skLineSegment(sketch, "E2.3.8.1", {"start": v(216, -436) * mm, "end": v(216, -486) * mm});
            skLineSegment(sketch, "E2.3.8.2", {"start": v(166, -486) * mm, "end": v(216, -486) * mm});
            skLineSegment(sketch, "E2.3.8.3", {"start": v(166, -436) * mm, "end": v(166, -486) * mm});
            skLineSegment(sketch, "E2.3.9.0", {"start": v(166, -490) * mm, "end": v(216, -490) * mm});
            skLineSegment(sketch, "E2.3.9.1", {"start": v(216, -490) * mm, "end": v(216, -540) * mm});
            skLineSegment(sketch, "E2.3.9.2", {"start": v(166, -540) * mm, "end": v(216, -540) * mm});
            skLineSegment(sketch, "E2.3.9.3", {"start": v(166, -490) * mm, "end": v(166, -540) * mm});
            skLineSegment(sketch, "E2.3.10.0", {"start": v(166, -544) * mm, "end": v(216, -544) * mm});
            skLineSegment(sketch, "E2.3.10.1", {"start": v(216, -544) * mm, "end": v(216, -594) * mm});
            skLineSegment(sketch, "E2.3.10.2", {"start": v(166, -594) * mm, "end": v(216, -594) * mm});
            skLineSegment(sketch, "E2.3.10.3", {"start": v(166, -544) * mm, "end": v(166, -594) * mm});
            skLineSegment(sketch, "E2.3.11.0", {"start": v(166, -598) * mm, "end": v(216, -598) * mm});
            skLineSegment(sketch, "E2.3.11.1", {"start": v(216, -598) * mm, "end": v(216, -648) * mm});
            skLineSegment(sketch, "E2.3.11.2", {"start": v(166, -648) * mm, "end": v(216, -648) * mm});
            skLineSegment(sketch, "E2.3.11.3", {"start": v(166, -598) * mm, "end": v(166, -648) * mm});
            skLineSegment(sketch, "E2.3.12.0", {"start": v(166, -652) * mm, "end": v(216, -652) * mm});
            skLineSegment(sketch, "E2.3.12.1", {"start": v(216, -652) * mm, "end": v(216, -702) * mm});
            skLineSegment(sketch, "E2.3.12.2", {"start": v(166, -702) * mm, "end": v(216, -702) * mm});
            skLineSegment(sketch, "E2.3.12.3", {"start": v(166, -652) * mm, "end": v(166, -702) * mm});
            skLineSegment(sketch, "E2.3.13.0", {"start": v(166, -706) * mm, "end": v(216, -706) * mm});
            skLineSegment(sketch, "E2.3.13.1", {"start": v(216, -706) * mm, "end": v(216, -756) * mm});
            skLineSegment(sketch, "E2.3.13.2", {"start": v(166, -756) * mm, "end": v(216, -756) * mm});
            skLineSegment(sketch, "E2.3.13.3", {"start": v(166, -706) * mm, "end": v(166, -756) * mm});
            skLineSegment(sketch, "E2.3.14.0", {"start": v(166, -760) * mm, "end": v(216, -760) * mm});
            skLineSegment(sketch, "E2.3.14.1", {"start": v(216, -760) * mm, "end": v(216, -810) * mm});
            skLineSegment(sketch, "E2.3.14.2", {"start": v(166, -810) * mm, "end": v(216, -810) * mm});
            skLineSegment(sketch, "E2.3.14.3", {"start": v(166, -760) * mm, "end": v(166, -810) * mm});
            skLineSegment(sketch, "E2.3.15.0", {"start": v(166, -814) * mm, "end": v(216, -814) * mm});
            skLineSegment(sketch, "E2.3.15.1", {"start": v(216, -814) * mm, "end": v(216, -864) * mm});
            skLineSegment(sketch, "E2.3.15.2", {"start": v(166, -864) * mm, "end": v(216, -864) * mm});
            skLineSegment(sketch, "E2.3.15.3", {"start": v(166, -814) * mm, "end": v(166, -864) * mm});
            skLineSegment(sketch, "E2.3.16.0", {"start": v(166, -868) * mm, "end": v(216, -868) * mm});
            skLineSegment(sketch, "E2.3.16.1", {"start": v(216, -868) * mm, "end": v(216, -918) * mm});
            skLineSegment(sketch, "E2.3.16.2", {"start": v(166, -918) * mm, "end": v(216, -918) * mm});
            skLineSegment(sketch, "E2.3.16.3", {"start": v(166, -868) * mm, "end": v(166, -918) * mm});
            skLineSegment(sketch, "E2.3.17.0", {"start": v(166, -922) * mm, "end": v(216, -922) * mm});
            skLineSegment(sketch, "E2.3.17.1", {"start": v(216, -922) * mm, "end": v(216, -972) * mm});
            skLineSegment(sketch, "E2.3.17.2", {"start": v(166, -972) * mm, "end": v(216, -972) * mm});
            skLineSegment(sketch, "E2.3.17.3", {"start": v(166, -922) * mm, "end": v(166, -972) * mm});
            skLineSegment(sketch, "E2.3.18.0", {"start": v(166, -976) * mm, "end": v(216, -976) * mm});
            skLineSegment(sketch, "E2.3.18.1", {"start": v(216, -976) * mm, "end": v(216, -1026) * mm});
            skLineSegment(sketch, "E2.3.18.2", {"start": v(166, -1026) * mm, "end": v(216, -1026) * mm});
            skLineSegment(sketch, "E2.3.18.3", {"start": v(166, -976) * mm, "end": v(166, -1026) * mm});
            skLineSegment(sketch, "E2.3.19.0", {"start": v(166, -1030) * mm, "end": v(216, -1030) * mm});
            skLineSegment(sketch, "E2.3.19.1", {"start": v(216, -1030) * mm, "end": v(216, -1080) * mm});
            skLineSegment(sketch, "E2.3.19.2", {"start": v(166, -1080) * mm, "end": v(216, -1080) * mm});
            skLineSegment(sketch, "E2.3.19.3", {"start": v(166, -1030) * mm, "end": v(166, -1080) * mm});
            skLineSegment(sketch, "E2.3.20.0", {"start": v(166, -1084) * mm, "end": v(216, -1084) * mm});
            skLineSegment(sketch, "E2.3.20.1", {"start": v(216, -1084) * mm, "end": v(216, -1134) * mm});
            skLineSegment(sketch, "E2.3.20.2", {"start": v(166, -1134) * mm, "end": v(216, -1134) * mm});
            skLineSegment(sketch, "E2.3.20.3", {"start": v(166, -1084) * mm, "end": v(166, -1134) * mm});
            skLineSegment(sketch, "E2.3.21.0", {"start": v(166, -1138) * mm, "end": v(216, -1138) * mm});
            skLineSegment(sketch, "E2.3.21.1", {"start": v(216, -1138) * mm, "end": v(216, -1188) * mm});
            skLineSegment(sketch, "E2.3.21.2", {"start": v(166, -1188) * mm, "end": v(216, -1188) * mm});
            skLineSegment(sketch, "E2.3.21.3", {"start": v(166, -1138) * mm, "end": v(166, -1188) * mm});
            skLineSegment(sketch, "E2.3.22.0", {"start": v(166, -1192) * mm, "end": v(216, -1192) * mm});
            skLineSegment(sketch, "E2.3.22.1", {"start": v(216, -1192) * mm, "end": v(216, -1242) * mm});
            skLineSegment(sketch, "E2.3.22.2", {"start": v(166, -1242) * mm, "end": v(216, -1242) * mm});
            skLineSegment(sketch, "E2.3.22.3", {"start": v(166, -1192) * mm, "end": v(166, -1242) * mm});
            skLineSegment(sketch, "E2.3.23.0", {"start": v(166, -1246) * mm, "end": v(216, -1246) * mm});
            skLineSegment(sketch, "E2.3.23.1", {"start": v(216, -1246) * mm, "end": v(216, -1296) * mm});
            skLineSegment(sketch, "E2.3.23.2", {"start": v(166, -1296) * mm, "end": v(216, -1296) * mm});
            skLineSegment(sketch, "E2.3.23.3", {"start": v(166, -1246) * mm, "end": v(166, -1296) * mm});
            skLineSegment(sketch, "E2.3.24.0", {"start": v(166, -1300) * mm, "end": v(216, -1300) * mm});
            skLineSegment(sketch, "E2.3.24.1", {"start": v(216, -1300) * mm, "end": v(216, -1350) * mm});
            skLineSegment(sketch, "E2.3.24.2", {"start": v(166, -1350) * mm, "end": v(216, -1350) * mm});
            skLineSegment(sketch, "E2.3.24.3", {"start": v(166, -1300) * mm, "end": v(166, -1350) * mm});
            skLineSegment(sketch, "E2.4.0.0", {"start": v(220, -4) * mm, "end": v(270, -4) * mm});
            skLineSegment(sketch, "E2.4.0.1", {"start": v(270, -4) * mm, "end": v(270, -54) * mm});
            skLineSegment(sketch, "E2.4.0.2", {"start": v(220, -54) * mm, "end": v(270, -54) * mm});
            skLineSegment(sketch, "E2.4.0.3", {"start": v(220, -4) * mm, "end": v(220, -54) * mm});
            skLineSegment(sketch, "E2.4.1.0", {"start": v(220, -58) * mm, "end": v(270, -58) * mm});
            skLineSegment(sketch, "E2.4.1.1", {"start": v(270, -58) * mm, "end": v(270, -108) * mm});
            skLineSegment(sketch, "E2.4.1.2", {"start": v(220, -108) * mm, "end": v(270, -108) * mm});
            skLineSegment(sketch, "E2.4.1.3", {"start": v(220, -58) * mm, "end": v(220, -108) * mm});
            skLineSegment(sketch, "E2.4.2.0", {"start": v(220, -112) * mm, "end": v(270, -112) * mm});
            skLineSegment(sketch, "E2.4.2.1", {"start": v(270, -112) * mm, "end": v(270, -162) * mm});
            skLineSegment(sketch, "E2.4.2.2", {"start": v(220, -162) * mm, "end": v(270, -162) * mm});
            skLineSegment(sketch, "E2.4.2.3", {"start": v(220, -112) * mm, "end": v(220, -162) * mm});
            skLineSegment(sketch, "E2.4.3.0", {"start": v(220, -166) * mm, "end": v(270, -166) * mm});
            skLineSegment(sketch, "E2.4.3.1", {"start": v(270, -166) * mm, "end": v(270, -216) * mm});
            skLineSegment(sketch, "E2.4.3.2", {"start": v(220, -216) * mm, "end": v(270, -216) * mm});
            skLineSegment(sketch, "E2.4.3.3", {"start": v(220, -166) * mm, "end": v(220, -216) * mm});
            skLineSegment(sketch, "E2.4.4.0", {"start": v(220, -220) * mm, "end": v(270, -220) * mm});
            skLineSegment(sketch, "E2.4.4.1", {"start": v(270, -220) * mm, "end": v(270, -270) * mm});
            skLineSegment(sketch, "E2.4.4.2", {"start": v(220, -270) * mm, "end": v(270, -270) * mm});
            skLineSegment(sketch, "E2.4.4.3", {"start": v(220, -220) * mm, "end": v(220, -270) * mm});
            skLineSegment(sketch, "E2.4.5.0", {"start": v(220, -274) * mm, "end": v(270, -274) * mm});
            skLineSegment(sketch, "E2.4.5.1", {"start": v(270, -274) * mm, "end": v(270, -324) * mm});
            skLineSegment(sketch, "E2.4.5.2", {"start": v(220, -324) * mm, "end": v(270, -324) * mm});
            skLineSegment(sketch, "E2.4.5.3", {"start": v(220, -274) * mm, "end": v(220, -324) * mm});
            skLineSegment(sketch, "E2.4.6.0", {"start": v(220, -328) * mm, "end": v(270, -328) * mm});
            skLineSegment(sketch, "E2.4.6.1", {"start": v(270, -328) * mm, "end": v(270, -378) * mm});
            skLineSegment(sketch, "E2.4.6.2", {"start": v(220, -378) * mm, "end": v(270, -378) * mm});
            skLineSegment(sketch, "E2.4.6.3", {"start": v(220, -328) * mm, "end": v(220, -378) * mm});
            skLineSegment(sketch, "E2.4.7.0", {"start": v(220, -382) * mm, "end": v(270, -382) * mm});
            skLineSegment(sketch, "E2.4.7.1", {"start": v(270, -382) * mm, "end": v(270, -432) * mm});
            skLineSegment(sketch, "E2.4.7.2", {"start": v(220, -432) * mm, "end": v(270, -432) * mm});
            skLineSegment(sketch, "E2.4.7.3", {"start": v(220, -382) * mm, "end": v(220, -432) * mm});
            skLineSegment(sketch, "E2.4.8.0", {"start": v(220, -436) * mm, "end": v(270, -436) * mm});
            skLineSegment(sketch, "E2.4.8.1", {"start": v(270, -436) * mm, "end": v(270, -486) * mm});
            skLineSegment(sketch, "E2.4.8.2", {"start": v(220, -486) * mm, "end": v(270, -486) * mm});
            skLineSegment(sketch, "E2.4.8.3", {"start": v(220, -436) * mm, "end": v(220, -486) * mm});
            skLineSegment(sketch, "E2.4.9.0", {"start": v(220, -490) * mm, "end": v(270, -490) * mm});
            skLineSegment(sketch, "E2.4.9.1", {"start": v(270, -490) * mm, "end": v(270, -540) * mm});
            skLineSegment(sketch, "E2.4.9.2", {"start": v(220, -540) * mm, "end": v(270, -540) * mm});
            skLineSegment(sketch, "E2.4.9.3", {"start": v(220, -490) * mm, "end": v(220, -540) * mm});
            skLineSegment(sketch, "E2.4.10.0", {"start": v(220, -544) * mm, "end": v(270, -544) * mm});
            skLineSegment(sketch, "E2.4.10.1", {"start": v(270, -544) * mm, "end": v(270, -594) * mm});
            skLineSegment(sketch, "E2.4.10.2", {"start": v(220, -594) * mm, "end": v(270, -594) * mm});
            skLineSegment(sketch, "E2.4.10.3", {"start": v(220, -544) * mm, "end": v(220, -594) * mm});
            skLineSegment(sketch, "E2.4.11.0", {"start": v(220, -598) * mm, "end": v(270, -598) * mm});
            skLineSegment(sketch, "E2.4.11.1", {"start": v(270, -598) * mm, "end": v(270, -648) * mm});
            skLineSegment(sketch, "E2.4.11.2", {"start": v(220, -648) * mm, "end": v(270, -648) * mm});
            skLineSegment(sketch, "E2.4.11.3", {"start": v(220, -598) * mm, "end": v(220, -648) * mm});
            skLineSegment(sketch, "E2.4.12.0", {"start": v(220, -652) * mm, "end": v(270, -652) * mm});
            skLineSegment(sketch, "E2.4.12.1", {"start": v(270, -652) * mm, "end": v(270, -702) * mm});
            skLineSegment(sketch, "E2.4.12.2", {"start": v(220, -702) * mm, "end": v(270, -702) * mm});
            skLineSegment(sketch, "E2.4.12.3", {"start": v(220, -652) * mm, "end": v(220, -702) * mm});
            skLineSegment(sketch, "E2.4.13.0", {"start": v(220, -706) * mm, "end": v(270, -706) * mm});
            skLineSegment(sketch, "E2.4.13.1", {"start": v(270, -706) * mm, "end": v(270, -756) * mm});
            skLineSegment(sketch, "E2.4.13.2", {"start": v(220, -756) * mm, "end": v(270, -756) * mm});
            skLineSegment(sketch, "E2.4.13.3", {"start": v(220, -706) * mm, "end": v(220, -756) * mm});
            skLineSegment(sketch, "E2.4.14.0", {"start": v(220, -760) * mm, "end": v(270, -760) * mm});
            skLineSegment(sketch, "E2.4.14.1", {"start": v(270, -760) * mm, "end": v(270, -810) * mm});
            skLineSegment(sketch, "E2.4.14.2", {"start": v(220, -810) * mm, "end": v(270, -810) * mm});
            skLineSegment(sketch, "E2.4.14.3", {"start": v(220, -760) * mm, "end": v(220, -810) * mm});
            skLineSegment(sketch, "E2.4.15.0", {"start": v(220, -814) * mm, "end": v(270, -814) * mm});
            skLineSegment(sketch, "E2.4.15.1", {"start": v(270, -814) * mm, "end": v(270, -864) * mm});
            skLineSegment(sketch, "E2.4.15.2", {"start": v(220, -864) * mm, "end": v(270, -864) * mm});
            skLineSegment(sketch, "E2.4.15.3", {"start": v(220, -814) * mm, "end": v(220, -864) * mm});
            skLineSegment(sketch, "E2.4.16.0", {"start": v(220, -868) * mm, "end": v(270, -868) * mm});
            skLineSegment(sketch, "E2.4.16.1", {"start": v(270, -868) * mm, "end": v(270, -918) * mm});
            skLineSegment(sketch, "E2.4.16.2", {"start": v(220, -918) * mm, "end": v(270, -918) * mm});
            skLineSegment(sketch, "E2.4.16.3", {"start": v(220, -868) * mm, "end": v(220, -918) * mm});
            skLineSegment(sketch, "E2.4.17.0", {"start": v(220, -922) * mm, "end": v(270, -922) * mm});
            skLineSegment(sketch, "E2.4.17.1", {"start": v(270, -922) * mm, "end": v(270, -972) * mm});
            skLineSegment(sketch, "E2.4.17.2", {"start": v(220, -972) * mm, "end": v(270, -972) * mm});
            skLineSegment(sketch, "E2.4.17.3", {"start": v(220, -922) * mm, "end": v(220, -972) * mm});
            skLineSegment(sketch, "E2.4.18.0", {"start": v(220, -976) * mm, "end": v(270, -976) * mm});
            skLineSegment(sketch, "E2.4.18.1", {"start": v(270, -976) * mm, "end": v(270, -1026) * mm});
            skLineSegment(sketch, "E2.4.18.2", {"start": v(220, -1026) * mm, "end": v(270, -1026) * mm});
            skLineSegment(sketch, "E2.4.18.3", {"start": v(220, -976) * mm, "end": v(220, -1026) * mm});
            skLineSegment(sketch, "E2.4.19.0", {"start": v(220, -1030) * mm, "end": v(270, -1030) * mm});
            skLineSegment(sketch, "E2.4.19.1", {"start": v(270, -1030) * mm, "end": v(270, -1080) * mm});
            skLineSegment(sketch, "E2.4.19.2", {"start": v(220, -1080) * mm, "end": v(270, -1080) * mm});
            skLineSegment(sketch, "E2.4.19.3", {"start": v(220, -1030) * mm, "end": v(220, -1080) * mm});
            skLineSegment(sketch, "E2.4.20.0", {"start": v(220, -1084) * mm, "end": v(270, -1084) * mm});
            skLineSegment(sketch, "E2.4.20.1", {"start": v(270, -1084) * mm, "end": v(270, -1134) * mm});
            skLineSegment(sketch, "E2.4.20.2", {"start": v(220, -1134) * mm, "end": v(270, -1134) * mm});
            skLineSegment(sketch, "E2.4.20.3", {"start": v(220, -1084) * mm, "end": v(220, -1134) * mm});
            skLineSegment(sketch, "E2.4.21.0", {"start": v(220, -1138) * mm, "end": v(270, -1138) * mm});
            skLineSegment(sketch, "E2.4.21.1", {"start": v(270, -1138) * mm, "end": v(270, -1188) * mm});
            skLineSegment(sketch, "E2.4.21.2", {"start": v(220, -1188) * mm, "end": v(270, -1188) * mm});
            skLineSegment(sketch, "E2.4.21.3", {"start": v(220, -1138) * mm, "end": v(220, -1188) * mm});
            skLineSegment(sketch, "E2.4.22.0", {"start": v(220, -1192) * mm, "end": v(270, -1192) * mm});
            skLineSegment(sketch, "E2.4.22.1", {"start": v(270, -1192) * mm, "end": v(270, -1242) * mm});
            skLineSegment(sketch, "E2.4.22.2", {"start": v(220, -1242) * mm, "end": v(270, -1242) * mm});
            skLineSegment(sketch, "E2.4.22.3", {"start": v(220, -1192) * mm, "end": v(220, -1242) * mm});
            skLineSegment(sketch, "E2.4.23.0", {"start": v(220, -1246) * mm, "end": v(270, -1246) * mm});
            skLineSegment(sketch, "E2.4.23.1", {"start": v(270, -1246) * mm, "end": v(270, -1296) * mm});
            skLineSegment(sketch, "E2.4.23.2", {"start": v(220, -1296) * mm, "end": v(270, -1296) * mm});
            skLineSegment(sketch, "E2.4.23.3", {"start": v(220, -1246) * mm, "end": v(220, -1296) * mm});
            skLineSegment(sketch, "E2.4.24.0", {"start": v(220, -1300) * mm, "end": v(270, -1300) * mm});
            skLineSegment(sketch, "E2.4.24.1", {"start": v(270, -1300) * mm, "end": v(270, -1350) * mm});
            skLineSegment(sketch, "E2.4.24.2", {"start": v(220, -1350) * mm, "end": v(270, -1350) * mm});
            skLineSegment(sketch, "E2.4.24.3", {"start": v(220, -1300) * mm, "end": v(220, -1350) * mm});
            skLineSegment(sketch, "E2.5.0.0", {"start": v(274, -4) * mm, "end": v(324, -4) * mm});
            skLineSegment(sketch, "E2.5.0.1", {"start": v(324, -4) * mm, "end": v(324, -54) * mm});
            skLineSegment(sketch, "E2.5.0.2", {"start": v(274, -54) * mm, "end": v(324, -54) * mm});
            skLineSegment(sketch, "E2.5.0.3", {"start": v(274, -4) * mm, "end": v(274, -54) * mm});
            skLineSegment(sketch, "E2.5.1.0", {"start": v(274, -58) * mm, "end": v(324, -58) * mm});
            skLineSegment(sketch, "E2.5.1.1", {"start": v(324, -58) * mm, "end": v(324, -108) * mm});
            skLineSegment(sketch, "E2.5.1.2", {"start": v(274, -108) * mm, "end": v(324, -108) * mm});
            skLineSegment(sketch, "E2.5.1.3", {"start": v(274, -58) * mm, "end": v(274, -108) * mm});
            skLineSegment(sketch, "E2.5.2.0", {"start": v(274, -112) * mm, "end": v(324, -112) * mm});
            skLineSegment(sketch, "E2.5.2.1", {"start": v(324, -112) * mm, "end": v(324, -162) * mm});
            skLineSegment(sketch, "E2.5.2.2", {"start": v(274, -162) * mm, "end": v(324, -162) * mm});
            skLineSegment(sketch, "E2.5.2.3", {"start": v(274, -112) * mm, "end": v(274, -162) * mm});
            skLineSegment(sketch, "E2.5.3.0", {"start": v(274, -166) * mm, "end": v(324, -166) * mm});
            skLineSegment(sketch, "E2.5.3.1", {"start": v(324, -166) * mm, "end": v(324, -216) * mm});
            skLineSegment(sketch, "E2.5.3.2", {"start": v(274, -216) * mm, "end": v(324, -216) * mm});
            skLineSegment(sketch, "E2.5.3.3", {"start": v(274, -166) * mm, "end": v(274, -216) * mm});
            skLineSegment(sketch, "E2.5.4.0", {"start": v(274, -220) * mm, "end": v(324, -220) * mm});
            skLineSegment(sketch, "E2.5.4.1", {"start": v(324, -220) * mm, "end": v(324, -270) * mm});
            skLineSegment(sketch, "E2.5.4.2", {"start": v(274, -270) * mm, "end": v(324, -270) * mm});
            skLineSegment(sketch, "E2.5.4.3", {"start": v(274, -220) * mm, "end": v(274, -270) * mm});
            skLineSegment(sketch, "E2.5.5.0", {"start": v(274, -274) * mm, "end": v(324, -274) * mm});
            skLineSegment(sketch, "E2.5.5.1", {"start": v(324, -274) * mm, "end": v(324, -324) * mm});
            skLineSegment(sketch, "E2.5.5.2", {"start": v(274, -324) * mm, "end": v(324, -324) * mm});
            skLineSegment(sketch, "E2.5.5.3", {"start": v(274, -274) * mm, "end": v(274, -324) * mm});
            skLineSegment(sketch, "E2.5.6.0", {"start": v(274, -328) * mm, "end": v(324, -328) * mm});
            skLineSegment(sketch, "E2.5.6.1", {"start": v(324, -328) * mm, "end": v(324, -378) * mm});
            skLineSegment(sketch, "E2.5.6.2", {"start": v(274, -378) * mm, "end": v(324, -378) * mm});
            skLineSegment(sketch, "E2.5.6.3", {"start": v(274, -328) * mm, "end": v(274, -378) * mm});
            skLineSegment(sketch, "E2.5.7.0", {"start": v(274, -382) * mm, "end": v(324, -382) * mm});
            skLineSegment(sketch, "E2.5.7.1", {"start": v(324, -382) * mm, "end": v(324, -432) * mm});
            skLineSegment(sketch, "E2.5.7.2", {"start": v(274, -432) * mm, "end": v(324, -432) * mm});
            skLineSegment(sketch, "E2.5.7.3", {"start": v(274, -382) * mm, "end": v(274, -432) * mm});
            skLineSegment(sketch, "E2.5.8.0", {"start": v(274, -436) * mm, "end": v(324, -436) * mm});
            skLineSegment(sketch, "E2.5.8.1", {"start": v(324, -436) * mm, "end": v(324, -486) * mm});
            skLineSegment(sketch, "E2.5.8.2", {"start": v(274, -486) * mm, "end": v(324, -486) * mm});
            skLineSegment(sketch, "E2.5.8.3", {"start": v(274, -436) * mm, "end": v(274, -486) * mm});
            skLineSegment(sketch, "E2.5.9.0", {"start": v(274, -490) * mm, "end": v(324, -490) * mm});
            skLineSegment(sketch, "E2.5.9.1", {"start": v(324, -490) * mm, "end": v(324, -540) * mm});
            skLineSegment(sketch, "E2.5.9.2", {"start": v(274, -540) * mm, "end": v(324, -540) * mm});
            skLineSegment(sketch, "E2.5.9.3", {"start": v(274, -490) * mm, "end": v(274, -540) * mm});
            skLineSegment(sketch, "E2.5.10.0", {"start": v(274, -544) * mm, "end": v(324, -544) * mm});
            skLineSegment(sketch, "E2.5.10.1", {"start": v(324, -544) * mm, "end": v(324, -594) * mm});
            skLineSegment(sketch, "E2.5.10.2", {"start": v(274, -594) * mm, "end": v(324, -594) * mm});
            skLineSegment(sketch, "E2.5.10.3", {"start": v(274, -544) * mm, "end": v(274, -594) * mm});
            skLineSegment(sketch, "E2.5.11.0", {"start": v(274, -598) * mm, "end": v(324, -598) * mm});
            skLineSegment(sketch, "E2.5.11.1", {"start": v(324, -598) * mm, "end": v(324, -648) * mm});
            skLineSegment(sketch, "E2.5.11.2", {"start": v(274, -648) * mm, "end": v(324, -648) * mm});
            skLineSegment(sketch, "E2.5.11.3", {"start": v(274, -598) * mm, "end": v(274, -648) * mm});
            skLineSegment(sketch, "E2.5.12.0", {"start": v(274, -652) * mm, "end": v(324, -652) * mm});
            skLineSegment(sketch, "E2.5.12.1", {"start": v(324, -652) * mm, "end": v(324, -702) * mm});
            skLineSegment(sketch, "E2.5.12.2", {"start": v(274, -702) * mm, "end": v(324, -702) * mm});
            skLineSegment(sketch, "E2.5.12.3", {"start": v(274, -652) * mm, "end": v(274, -702) * mm});
            skLineSegment(sketch, "E2.5.13.0", {"start": v(274, -706) * mm, "end": v(324, -706) * mm});
            skLineSegment(sketch, "E2.5.13.1", {"start": v(324, -706) * mm, "end": v(324, -756) * mm});
            skLineSegment(sketch, "E2.5.13.2", {"start": v(274, -756) * mm, "end": v(324, -756) * mm});
            skLineSegment(sketch, "E2.5.13.3", {"start": v(274, -706) * mm, "end": v(274, -756) * mm});
            skLineSegment(sketch, "E2.5.14.0", {"start": v(274, -760) * mm, "end": v(324, -760) * mm});
            skLineSegment(sketch, "E2.5.14.1", {"start": v(324, -760) * mm, "end": v(324, -810) * mm});
            skLineSegment(sketch, "E2.5.14.2", {"start": v(274, -810) * mm, "end": v(324, -810) * mm});
            skLineSegment(sketch, "E2.5.14.3", {"start": v(274, -760) * mm, "end": v(274, -810) * mm});
            skLineSegment(sketch, "E2.5.15.0", {"start": v(274, -814) * mm, "end": v(324, -814) * mm});
            skLineSegment(sketch, "E2.5.15.1", {"start": v(324, -814) * mm, "end": v(324, -864) * mm});
            skLineSegment(sketch, "E2.5.15.2", {"start": v(274, -864) * mm, "end": v(324, -864) * mm});
            skLineSegment(sketch, "E2.5.15.3", {"start": v(274, -814) * mm, "end": v(274, -864) * mm});
            skLineSegment(sketch, "E2.5.16.0", {"start": v(274, -868) * mm, "end": v(324, -868) * mm});
            skLineSegment(sketch, "E2.5.16.1", {"start": v(324, -868) * mm, "end": v(324, -918) * mm});
            skLineSegment(sketch, "E2.5.16.2", {"start": v(274, -918) * mm, "end": v(324, -918) * mm});
            skLineSegment(sketch, "E2.5.16.3", {"start": v(274, -868) * mm, "end": v(274, -918) * mm});
            skLineSegment(sketch, "E2.5.17.0", {"start": v(274, -922) * mm, "end": v(324, -922) * mm});
            skLineSegment(sketch, "E2.5.17.1", {"start": v(324, -922) * mm, "end": v(324, -972) * mm});
            skLineSegment(sketch, "E2.5.17.2", {"start": v(274, -972) * mm, "end": v(324, -972) * mm});
            skLineSegment(sketch, "E2.5.17.3", {"start": v(274, -922) * mm, "end": v(274, -972) * mm});
            skLineSegment(sketch, "E2.5.18.0", {"start": v(274, -976) * mm, "end": v(324, -976) * mm});
            skLineSegment(sketch, "E2.5.18.1", {"start": v(324, -976) * mm, "end": v(324, -1026) * mm});
            skLineSegment(sketch, "E2.5.18.2", {"start": v(274, -1026) * mm, "end": v(324, -1026) * mm});
            skLineSegment(sketch, "E2.5.18.3", {"start": v(274, -976) * mm, "end": v(274, -1026) * mm});
            skLineSegment(sketch, "E2.5.19.0", {"start": v(274, -1030) * mm, "end": v(324, -1030) * mm});
            skLineSegment(sketch, "E2.5.19.1", {"start": v(324, -1030) * mm, "end": v(324, -1080) * mm});
            skLineSegment(sketch, "E2.5.19.2", {"start": v(274, -1080) * mm, "end": v(324, -1080) * mm});
            skLineSegment(sketch, "E2.5.19.3", {"start": v(274, -1030) * mm, "end": v(274, -1080) * mm});
            skLineSegment(sketch, "E2.5.20.0", {"start": v(274, -1084) * mm, "end": v(324, -1084) * mm});
            skLineSegment(sketch, "E2.5.20.1", {"start": v(324, -1084) * mm, "end": v(324, -1134) * mm});
            skLineSegment(sketch, "E2.5.20.2", {"start": v(274, -1134) * mm, "end": v(324, -1134) * mm});
            skLineSegment(sketch, "E2.5.20.3", {"start": v(274, -1084) * mm, "end": v(274, -1134) * mm});
            skLineSegment(sketch, "E2.5.21.0", {"start": v(274, -1138) * mm, "end": v(324, -1138) * mm});
            skLineSegment(sketch, "E2.5.21.1", {"start": v(324, -1138) * mm, "end": v(324, -1188) * mm});
            skLineSegment(sketch, "E2.5.21.2", {"start": v(274, -1188) * mm, "end": v(324, -1188) * mm});
            skLineSegment(sketch, "E2.5.21.3", {"start": v(274, -1138) * mm, "end": v(274, -1188) * mm});
            skLineSegment(sketch, "E2.5.22.0", {"start": v(274, -1192) * mm, "end": v(324, -1192) * mm});
            skLineSegment(sketch, "E2.5.22.1", {"start": v(324, -1192) * mm, "end": v(324, -1242) * mm});
            skLineSegment(sketch, "E2.5.22.2", {"start": v(274, -1242) * mm, "end": v(324, -1242) * mm});
            skLineSegment(sketch, "E2.5.22.3", {"start": v(274, -1192) * mm, "end": v(274, -1242) * mm});
            skLineSegment(sketch, "E2.5.23.0", {"start": v(274, -1246) * mm, "end": v(324, -1246) * mm});
            skLineSegment(sketch, "E2.5.23.1", {"start": v(324, -1246) * mm, "end": v(324, -1296) * mm});
            skLineSegment(sketch, "E2.5.23.2", {"start": v(274, -1296) * mm, "end": v(324, -1296) * mm});
            skLineSegment(sketch, "E2.5.23.3", {"start": v(274, -1246) * mm, "end": v(274, -1296) * mm});
            skLineSegment(sketch, "E2.5.24.0", {"start": v(274, -1300) * mm, "end": v(324, -1300) * mm});
            skLineSegment(sketch, "E2.5.24.1", {"start": v(324, -1300) * mm, "end": v(324, -1350) * mm});
            skLineSegment(sketch, "E2.5.24.2", {"start": v(274, -1350) * mm, "end": v(324, -1350) * mm});
            skLineSegment(sketch, "E2.5.24.3", {"start": v(274, -1300) * mm, "end": v(274, -1350) * mm});
            skLineSegment(sketch, "E2.6.0.0", {"start": v(328, -4) * mm, "end": v(378, -4) * mm});
            skLineSegment(sketch, "E2.6.0.1", {"start": v(378, -4) * mm, "end": v(378, -54) * mm});
            skLineSegment(sketch, "E2.6.0.2", {"start": v(328, -54) * mm, "end": v(378, -54) * mm});
            skLineSegment(sketch, "E2.6.0.3", {"start": v(328, -4) * mm, "end": v(328, -54) * mm});
            skLineSegment(sketch, "E2.6.1.0", {"start": v(328, -58) * mm, "end": v(378, -58) * mm});
            skLineSegment(sketch, "E2.6.1.1", {"start": v(378, -58) * mm, "end": v(378, -108) * mm});
            skLineSegment(sketch, "E2.6.1.2", {"start": v(328, -108) * mm, "end": v(378, -108) * mm});
            skLineSegment(sketch, "E2.6.1.3", {"start": v(328, -58) * mm, "end": v(328, -108) * mm});
            skLineSegment(sketch, "E2.6.2.0", {"start": v(328, -112) * mm, "end": v(378, -112) * mm});
            skLineSegment(sketch, "E2.6.2.1", {"start": v(378, -112) * mm, "end": v(378, -162) * mm});
            skLineSegment(sketch, "E2.6.2.2", {"start": v(328, -162) * mm, "end": v(378, -162) * mm});
            skLineSegment(sketch, "E2.6.2.3", {"start": v(328, -112) * mm, "end": v(328, -162) * mm});
            skLineSegment(sketch, "E2.6.3.0", {"start": v(328, -166) * mm, "end": v(378, -166) * mm});
            skLineSegment(sketch, "E2.6.3.1", {"start": v(378, -166) * mm, "end": v(378, -216) * mm});
            skLineSegment(sketch, "E2.6.3.2", {"start": v(328, -216) * mm, "end": v(378, -216) * mm});
            skLineSegment(sketch, "E2.6.3.3", {"start": v(328, -166) * mm, "end": v(328, -216) * mm});
            skLineSegment(sketch, "E2.6.4.0", {"start": v(328, -220) * mm, "end": v(378, -220) * mm});
            skLineSegment(sketch, "E2.6.4.1", {"start": v(378, -220) * mm, "end": v(378, -270) * mm});
            skLineSegment(sketch, "E2.6.4.2", {"start": v(328, -270) * mm, "end": v(378, -270) * mm});
            skLineSegment(sketch, "E2.6.4.3", {"start": v(328, -220) * mm, "end": v(328, -270) * mm});
            skLineSegment(sketch, "E2.6.5.0", {"start": v(328, -274) * mm, "end": v(378, -274) * mm});
            skLineSegment(sketch, "E2.6.5.1", {"start": v(378, -274) * mm, "end": v(378, -324) * mm});
            skLineSegment(sketch, "E2.6.5.2", {"start": v(328, -324) * mm, "end": v(378, -324) * mm});
            skLineSegment(sketch, "E2.6.5.3", {"start": v(328, -274) * mm, "end": v(328, -324) * mm});
            skLineSegment(sketch, "E2.6.6.0", {"start": v(328, -328) * mm, "end": v(378, -328) * mm});
            skLineSegment(sketch, "E2.6.6.1", {"start": v(378, -328) * mm, "end": v(378, -378) * mm});
            skLineSegment(sketch, "E2.6.6.2", {"start": v(328, -378) * mm, "end": v(378, -378) * mm});
            skLineSegment(sketch, "E2.6.6.3", {"start": v(328, -328) * mm, "end": v(328, -378) * mm});
            skLineSegment(sketch, "E2.6.7.0", {"start": v(328, -382) * mm, "end": v(378, -382) * mm});
            skLineSegment(sketch, "E2.6.7.1", {"start": v(378, -382) * mm, "end": v(378, -432) * mm});
            skLineSegment(sketch, "E2.6.7.2", {"start": v(328, -432) * mm, "end": v(378, -432) * mm});
            skLineSegment(sketch, "E2.6.7.3", {"start": v(328, -382) * mm, "end": v(328, -432) * mm});
            skLineSegment(sketch, "E2.6.8.0", {"start": v(328, -436) * mm, "end": v(378, -436) * mm});
            skLineSegment(sketch, "E2.6.8.1", {"start": v(378, -436) * mm, "end": v(378, -486) * mm});
            skLineSegment(sketch, "E2.6.8.2", {"start": v(328, -486) * mm, "end": v(378, -486) * mm});
            skLineSegment(sketch, "E2.6.8.3", {"start": v(328, -436) * mm, "end": v(328, -486) * mm});
            skLineSegment(sketch, "E2.6.9.0", {"start": v(328, -490) * mm, "end": v(378, -490) * mm});
            skLineSegment(sketch, "E2.6.9.1", {"start": v(378, -490) * mm, "end": v(378, -540) * mm});
            skLineSegment(sketch, "E2.6.9.2", {"start": v(328, -540) * mm, "end": v(378, -540) * mm});
            skLineSegment(sketch, "E2.6.9.3", {"start": v(328, -490) * mm, "end": v(328, -540) * mm});
            skLineSegment(sketch, "E2.6.10.0", {"start": v(328, -544) * mm, "end": v(378, -544) * mm});
            skLineSegment(sketch, "E2.6.10.1", {"start": v(378, -544) * mm, "end": v(378, -594) * mm});
            skLineSegment(sketch, "E2.6.10.2", {"start": v(328, -594) * mm, "end": v(378, -594) * mm});
            skLineSegment(sketch, "E2.6.10.3", {"start": v(328, -544) * mm, "end": v(328, -594) * mm});
            skLineSegment(sketch, "E2.6.11.0", {"start": v(328, -598) * mm, "end": v(378, -598) * mm});
            skLineSegment(sketch, "E2.6.11.1", {"start": v(378, -598) * mm, "end": v(378, -648) * mm});
            skLineSegment(sketch, "E2.6.11.2", {"start": v(328, -648) * mm, "end": v(378, -648) * mm});
            skLineSegment(sketch, "E2.6.11.3", {"start": v(328, -598) * mm, "end": v(328, -648) * mm});
            skLineSegment(sketch, "E2.6.12.0", {"start": v(328, -652) * mm, "end": v(378, -652) * mm});
            skLineSegment(sketch, "E2.6.12.1", {"start": v(378, -652) * mm, "end": v(378, -702) * mm});
            skLineSegment(sketch, "E2.6.12.2", {"start": v(328, -702) * mm, "end": v(378, -702) * mm});
            skLineSegment(sketch, "E2.6.12.3", {"start": v(328, -652) * mm, "end": v(328, -702) * mm});
            skLineSegment(sketch, "E2.6.13.0", {"start": v(328, -706) * mm, "end": v(378, -706) * mm});
            skLineSegment(sketch, "E2.6.13.1", {"start": v(378, -706) * mm, "end": v(378, -756) * mm});
            skLineSegment(sketch, "E2.6.13.2", {"start": v(328, -756) * mm, "end": v(378, -756) * mm});
            skLineSegment(sketch, "E2.6.13.3", {"start": v(328, -706) * mm, "end": v(328, -756) * mm});
            skLineSegment(sketch, "E2.6.14.0", {"start": v(328, -760) * mm, "end": v(378, -760) * mm});
            skLineSegment(sketch, "E2.6.14.1", {"start": v(378, -760) * mm, "end": v(378, -810) * mm});
            skLineSegment(sketch, "E2.6.14.2", {"start": v(328, -810) * mm, "end": v(378, -810) * mm});
            skLineSegment(sketch, "E2.6.14.3", {"start": v(328, -760) * mm, "end": v(328, -810) * mm});
            skLineSegment(sketch, "E2.6.15.0", {"start": v(328, -814) * mm, "end": v(378, -814) * mm});
            skLineSegment(sketch, "E2.6.15.1", {"start": v(378, -814) * mm, "end": v(378, -864) * mm});
            skLineSegment(sketch, "E2.6.15.2", {"start": v(328, -864) * mm, "end": v(378, -864) * mm});
            skLineSegment(sketch, "E2.6.15.3", {"start": v(328, -814) * mm, "end": v(328, -864) * mm});
            skLineSegment(sketch, "E2.6.16.0", {"start": v(328, -868) * mm, "end": v(378, -868) * mm});
            skLineSegment(sketch, "E2.6.16.1", {"start": v(378, -868) * mm, "end": v(378, -918) * mm});
            skLineSegment(sketch, "E2.6.16.2", {"start": v(328, -918) * mm, "end": v(378, -918) * mm});
            skLineSegment(sketch, "E2.6.16.3", {"start": v(328, -868) * mm, "end": v(328, -918) * mm});
            skLineSegment(sketch, "E2.6.17.0", {"start": v(328, -922) * mm, "end": v(378, -922) * mm});
            skLineSegment(sketch, "E2.6.17.1", {"start": v(378, -922) * mm, "end": v(378, -972) * mm});
            skLineSegment(sketch, "E2.6.17.2", {"start": v(328, -972) * mm, "end": v(378, -972) * mm});
            skLineSegment(sketch, "E2.6.17.3", {"start": v(328, -922) * mm, "end": v(328, -972) * mm});
            skLineSegment(sketch, "E2.6.18.0", {"start": v(328, -976) * mm, "end": v(378, -976) * mm});
            skLineSegment(sketch, "E2.6.18.1", {"start": v(378, -976) * mm, "end": v(378, -1026) * mm});
            skLineSegment(sketch, "E2.6.18.2", {"start": v(328, -1026) * mm, "end": v(378, -1026) * mm});
            skLineSegment(sketch, "E2.6.18.3", {"start": v(328, -976) * mm, "end": v(328, -1026) * mm});
            skLineSegment(sketch, "E2.6.19.0", {"start": v(328, -1030) * mm, "end": v(378, -1030) * mm});
            skLineSegment(sketch, "E2.6.19.1", {"start": v(378, -1030) * mm, "end": v(378, -1080) * mm});
            skLineSegment(sketch, "E2.6.19.2", {"start": v(328, -1080) * mm, "end": v(378, -1080) * mm});
            skLineSegment(sketch, "E2.6.19.3", {"start": v(328, -1030) * mm, "end": v(328, -1080) * mm});
            skLineSegment(sketch, "E2.6.20.0", {"start": v(328, -1084) * mm, "end": v(378, -1084) * mm});
            skLineSegment(sketch, "E2.6.20.1", {"start": v(378, -1084) * mm, "end": v(378, -1134) * mm});
            skLineSegment(sketch, "E2.6.20.2", {"start": v(328, -1134) * mm, "end": v(378, -1134) * mm});
            skLineSegment(sketch, "E2.6.20.3", {"start": v(328, -1084) * mm, "end": v(328, -1134) * mm});
            skLineSegment(sketch, "E2.6.21.0", {"start": v(328, -1138) * mm, "end": v(378, -1138) * mm});
            skLineSegment(sketch, "E2.6.21.1", {"start": v(378, -1138) * mm, "end": v(378, -1188) * mm});
            skLineSegment(sketch, "E2.6.21.2", {"start": v(328, -1188) * mm, "end": v(378, -1188) * mm});
            skLineSegment(sketch, "E2.6.21.3", {"start": v(328, -1138) * mm, "end": v(328, -1188) * mm});
            skLineSegment(sketch, "E2.6.22.0", {"start": v(328, -1192) * mm, "end": v(378, -1192) * mm});
            skLineSegment(sketch, "E2.6.22.1", {"start": v(378, -1192) * mm, "end": v(378, -1242) * mm});
            skLineSegment(sketch, "E2.6.22.2", {"start": v(328, -1242) * mm, "end": v(378, -1242) * mm});
            skLineSegment(sketch, "E2.6.22.3", {"start": v(328, -1192) * mm, "end": v(328, -1242) * mm});
            skLineSegment(sketch, "E2.6.23.0", {"start": v(328, -1246) * mm, "end": v(378, -1246) * mm});
            skLineSegment(sketch, "E2.6.23.1", {"start": v(378, -1246) * mm, "end": v(378, -1296) * mm});
            skLineSegment(sketch, "E2.6.23.2", {"start": v(328, -1296) * mm, "end": v(378, -1296) * mm});
            skLineSegment(sketch, "E2.6.23.3", {"start": v(328, -1246) * mm, "end": v(328, -1296) * mm});
            skLineSegment(sketch, "E2.6.24.0", {"start": v(328, -1300) * mm, "end": v(378, -1300) * mm});
            skLineSegment(sketch, "E2.6.24.1", {"start": v(378, -1300) * mm, "end": v(378, -1350) * mm});
            skLineSegment(sketch, "E2.6.24.2", {"start": v(328, -1350) * mm, "end": v(378, -1350) * mm});
            skLineSegment(sketch, "E2.6.24.3", {"start": v(328, -1300) * mm, "end": v(328, -1350) * mm});
            skLineSegment(sketch, "E2.direction1", {"start": v(4, -4) * mm, "end": v(58, -4) * mm, "construction": true});
            skLineSegment(sketch, "E2.direction2", {"start": v(4, -4) * mm, "end": v(4, -58) * mm, "construction": true});
            skLineSegment(sketch, "E3.0.0.25", {"start": v(4, -1354) * mm, "end": v(54, -1354) * mm});
            skLineSegment(sketch, "E3.3.0.25", {"start": v(54, -1354) * mm, "end": v(54, -1404) * mm});
            skLineSegment(sketch, "E3.6.0.25", {"start": v(4, -1404) * mm, "end": v(54, -1404) * mm});
            skLineSegment(sketch, "E3.9.0.25", {"start": v(4, -1354) * mm, "end": v(4, -1404) * mm});
            skLineSegment(sketch, "E3.0.1.25", {"start": v(58, -1354) * mm, "end": v(108, -1354) * mm});
            skLineSegment(sketch, "E3.3.1.25", {"start": v(108, -1354) * mm, "end": v(108, -1404) * mm});
            skLineSegment(sketch, "E3.6.1.25", {"start": v(58, -1404) * mm, "end": v(108, -1404) * mm});
            skLineSegment(sketch, "E3.9.1.25", {"start": v(58, -1354) * mm, "end": v(58, -1404) * mm});
            skLineSegment(sketch, "E3.0.2.25", {"start": v(112, -1354) * mm, "end": v(162, -1354) * mm});
            skLineSegment(sketch, "E3.3.2.25", {"start": v(162, -1354) * mm, "end": v(162, -1404) * mm});
            skLineSegment(sketch, "E3.6.2.25", {"start": v(112, -1404) * mm, "end": v(162, -1404) * mm});
            skLineSegment(sketch, "E3.9.2.25", {"start": v(112, -1354) * mm, "end": v(112, -1404) * mm});
            skLineSegment(sketch, "E3.0.3.25", {"start": v(166, -1354) * mm, "end": v(216, -1354) * mm});
            skLineSegment(sketch, "E3.3.3.25", {"start": v(216, -1354) * mm, "end": v(216, -1404) * mm});
            skLineSegment(sketch, "E3.6.3.25", {"start": v(166, -1404) * mm, "end": v(216, -1404) * mm});
            skLineSegment(sketch, "E3.9.3.25", {"start": v(166, -1354) * mm, "end": v(166, -1404) * mm});
            skLineSegment(sketch, "E3.0.4.25", {"start": v(220, -1354) * mm, "end": v(270, -1354) * mm});
            skLineSegment(sketch, "E3.3.4.25", {"start": v(270, -1354) * mm, "end": v(270, -1404) * mm});
            skLineSegment(sketch, "E3.6.4.25", {"start": v(220, -1404) * mm, "end": v(270, -1404) * mm});
            skLineSegment(sketch, "E3.9.4.25", {"start": v(220, -1354) * mm, "end": v(220, -1404) * mm});
            skLineSegment(sketch, "E3.0.5.25", {"start": v(274, -1354) * mm, "end": v(324, -1354) * mm});
            skLineSegment(sketch, "E3.3.5.25", {"start": v(324, -1354) * mm, "end": v(324, -1404) * mm});
            skLineSegment(sketch, "E3.6.5.25", {"start": v(274, -1404) * mm, "end": v(324, -1404) * mm});
            skLineSegment(sketch, "E3.9.5.25", {"start": v(274, -1354) * mm, "end": v(274, -1404) * mm});
            skLineSegment(sketch, "E3.0.6.25", {"start": v(328, -1354) * mm, "end": v(378, -1354) * mm});
            skLineSegment(sketch, "E3.3.6.25", {"start": v(378, -1354) * mm, "end": v(378, -1404) * mm});
            skLineSegment(sketch, "E3.6.6.25", {"start": v(328, -1404) * mm, "end": v(378, -1404) * mm});
            skLineSegment(sketch, "E3.9.6.25", {"start": v(328, -1354) * mm, "end": v(328, -1404) * mm});
            skLineSegment(sketch, "E4.0.7.0", {"start": v(382, -4) * mm, "end": v(432, -4) * mm});
            skLineSegment(sketch, "E4.3.7.0", {"start": v(432, -4) * mm, "end": v(432, -54) * mm});
            skLineSegment(sketch, "E4.6.7.0", {"start": v(382, -54) * mm, "end": v(432, -54) * mm});
            skLineSegment(sketch, "E4.9.7.0", {"start": v(382, -4) * mm, "end": v(382, -54) * mm});
            skLineSegment(sketch, "E4.0.7.1", {"start": v(382, -58) * mm, "end": v(432, -58) * mm});
            skLineSegment(sketch, "E4.3.7.1", {"start": v(432, -58) * mm, "end": v(432, -108) * mm});
            skLineSegment(sketch, "E4.6.7.1", {"start": v(382, -108) * mm, "end": v(432, -108) * mm});
            skLineSegment(sketch, "E4.9.7.1", {"start": v(382, -58) * mm, "end": v(382, -108) * mm});
            skLineSegment(sketch, "E4.0.7.2", {"start": v(382, -112) * mm, "end": v(432, -112) * mm});
            skLineSegment(sketch, "E4.3.7.2", {"start": v(432, -112) * mm, "end": v(432, -162) * mm});
            skLineSegment(sketch, "E4.6.7.2", {"start": v(382, -162) * mm, "end": v(432, -162) * mm});
            skLineSegment(sketch, "E4.9.7.2", {"start": v(382, -112) * mm, "end": v(382, -162) * mm});
            skLineSegment(sketch, "E4.0.7.3", {"start": v(382, -166) * mm, "end": v(432, -166) * mm});
            skLineSegment(sketch, "E4.3.7.3", {"start": v(432, -166) * mm, "end": v(432, -216) * mm});
            skLineSegment(sketch, "E4.6.7.3", {"start": v(382, -216) * mm, "end": v(432, -216) * mm});
            skLineSegment(sketch, "E4.9.7.3", {"start": v(382, -166) * mm, "end": v(382, -216) * mm});
            skLineSegment(sketch, "E4.0.7.4", {"start": v(382, -220) * mm, "end": v(432, -220) * mm});
            skLineSegment(sketch, "E4.3.7.4", {"start": v(432, -220) * mm, "end": v(432, -270) * mm});
            skLineSegment(sketch, "E4.6.7.4", {"start": v(382, -270) * mm, "end": v(432, -270) * mm});
            skLineSegment(sketch, "E4.9.7.4", {"start": v(382, -220) * mm, "end": v(382, -270) * mm});
            skLineSegment(sketch, "E4.0.7.5", {"start": v(382, -274) * mm, "end": v(432, -274) * mm});
            skLineSegment(sketch, "E4.3.7.5", {"start": v(432, -274) * mm, "end": v(432, -324) * mm});
            skLineSegment(sketch, "E4.6.7.5", {"start": v(382, -324) * mm, "end": v(432, -324) * mm});
            skLineSegment(sketch, "E4.9.7.5", {"start": v(382, -274) * mm, "end": v(382, -324) * mm});
            skLineSegment(sketch, "E4.0.7.6", {"start": v(382, -328) * mm, "end": v(432, -328) * mm});
            skLineSegment(sketch, "E4.3.7.6", {"start": v(432, -328) * mm, "end": v(432, -378) * mm});
            skLineSegment(sketch, "E4.6.7.6", {"start": v(382, -378) * mm, "end": v(432, -378) * mm});
            skLineSegment(sketch, "E4.9.7.6", {"start": v(382, -328) * mm, "end": v(382, -378) * mm});
            skLineSegment(sketch, "E4.0.7.7", {"start": v(382, -382) * mm, "end": v(432, -382) * mm});
            skLineSegment(sketch, "E4.3.7.7", {"start": v(432, -382) * mm, "end": v(432, -432) * mm});
            skLineSegment(sketch, "E4.6.7.7", {"start": v(382, -432) * mm, "end": v(432, -432) * mm});
            skLineSegment(sketch, "E4.9.7.7", {"start": v(382, -382) * mm, "end": v(382, -432) * mm});
            skLineSegment(sketch, "E4.0.7.8", {"start": v(382, -436) * mm, "end": v(432, -436) * mm});
            skLineSegment(sketch, "E4.3.7.8", {"start": v(432, -436) * mm, "end": v(432, -486) * mm});
            skLineSegment(sketch, "E4.6.7.8", {"start": v(382, -486) * mm, "end": v(432, -486) * mm});
            skLineSegment(sketch, "E4.9.7.8", {"start": v(382, -436) * mm, "end": v(382, -486) * mm});
            skLineSegment(sketch, "E4.0.7.9", {"start": v(382, -490) * mm, "end": v(432, -490) * mm});
            skLineSegment(sketch, "E4.3.7.9", {"start": v(432, -490) * mm, "end": v(432, -540) * mm});
            skLineSegment(sketch, "E4.6.7.9", {"start": v(382, -540) * mm, "end": v(432, -540) * mm});
            skLineSegment(sketch, "E4.9.7.9", {"start": v(382, -490) * mm, "end": v(382, -540) * mm});
            skLineSegment(sketch, "E4.0.7.10", {"start": v(382, -544) * mm, "end": v(432, -544) * mm});
            skLineSegment(sketch, "E4.3.7.10", {"start": v(432, -544) * mm, "end": v(432, -594) * mm});
            skLineSegment(sketch, "E4.6.7.10", {"start": v(382, -594) * mm, "end": v(432, -594) * mm});
            skLineSegment(sketch, "E4.9.7.10", {"start": v(382, -544) * mm, "end": v(382, -594) * mm});
            skLineSegment(sketch, "E4.0.7.11", {"start": v(382, -598) * mm, "end": v(432, -598) * mm});
            skLineSegment(sketch, "E4.3.7.11", {"start": v(432, -598) * mm, "end": v(432, -648) * mm});
            skLineSegment(sketch, "E4.6.7.11", {"start": v(382, -648) * mm, "end": v(432, -648) * mm});
            skLineSegment(sketch, "E4.9.7.11", {"start": v(382, -598) * mm, "end": v(382, -648) * mm});
            skLineSegment(sketch, "E4.0.7.12", {"start": v(382, -652) * mm, "end": v(432, -652) * mm});
            skLineSegment(sketch, "E4.3.7.12", {"start": v(432, -652) * mm, "end": v(432, -702) * mm});
            skLineSegment(sketch, "E4.6.7.12", {"start": v(382, -702) * mm, "end": v(432, -702) * mm});
            skLineSegment(sketch, "E4.9.7.12", {"start": v(382, -652) * mm, "end": v(382, -702) * mm});
            skLineSegment(sketch, "E4.0.7.13", {"start": v(382, -706) * mm, "end": v(432, -706) * mm});
            skLineSegment(sketch, "E4.3.7.13", {"start": v(432, -706) * mm, "end": v(432, -756) * mm});
            skLineSegment(sketch, "E4.6.7.13", {"start": v(382, -756) * mm, "end": v(432, -756) * mm});
            skLineSegment(sketch, "E4.9.7.13", {"start": v(382, -706) * mm, "end": v(382, -756) * mm});
            skLineSegment(sketch, "E4.0.7.14", {"start": v(382, -760) * mm, "end": v(432, -760) * mm});
            skLineSegment(sketch, "E4.3.7.14", {"start": v(432, -760) * mm, "end": v(432, -810) * mm});
            skLineSegment(sketch, "E4.6.7.14", {"start": v(382, -810) * mm, "end": v(432, -810) * mm});
            skLineSegment(sketch, "E4.9.7.14", {"start": v(382, -760) * mm, "end": v(382, -810) * mm});
            skLineSegment(sketch, "E4.0.7.15", {"start": v(382, -814) * mm, "end": v(432, -814) * mm});
            skLineSegment(sketch, "E4.3.7.15", {"start": v(432, -814) * mm, "end": v(432, -864) * mm});
            skLineSegment(sketch, "E4.6.7.15", {"start": v(382, -864) * mm, "end": v(432, -864) * mm});
            skLineSegment(sketch, "E4.9.7.15", {"start": v(382, -814) * mm, "end": v(382, -864) * mm});
            skLineSegment(sketch, "E4.0.7.16", {"start": v(382, -868) * mm, "end": v(432, -868) * mm});
            skLineSegment(sketch, "E4.3.7.16", {"start": v(432, -868) * mm, "end": v(432, -918) * mm});
            skLineSegment(sketch, "E4.6.7.16", {"start": v(382, -918) * mm, "end": v(432, -918) * mm});
            skLineSegment(sketch, "E4.9.7.16", {"start": v(382, -868) * mm, "end": v(382, -918) * mm});
            skLineSegment(sketch, "E4.0.7.17", {"start": v(382, -922) * mm, "end": v(432, -922) * mm});
            skLineSegment(sketch, "E4.3.7.17", {"start": v(432, -922) * mm, "end": v(432, -972) * mm});
            skLineSegment(sketch, "E4.6.7.17", {"start": v(382, -972) * mm, "end": v(432, -972) * mm});
            skLineSegment(sketch, "E4.9.7.17", {"start": v(382, -922) * mm, "end": v(382, -972) * mm});
            skLineSegment(sketch, "E4.0.7.18", {"start": v(382, -976) * mm, "end": v(432, -976) * mm});
            skLineSegment(sketch, "E4.3.7.18", {"start": v(432, -976) * mm, "end": v(432, -1026) * mm});
            skLineSegment(sketch, "E4.6.7.18", {"start": v(382, -1026) * mm, "end": v(432, -1026) * mm});
            skLineSegment(sketch, "E4.9.7.18", {"start": v(382, -976) * mm, "end": v(382, -1026) * mm});
            skLineSegment(sketch, "E4.0.7.19", {"start": v(382, -1030) * mm, "end": v(432, -1030) * mm});
            skLineSegment(sketch, "E4.3.7.19", {"start": v(432, -1030) * mm, "end": v(432, -1080) * mm});
            skLineSegment(sketch, "E4.6.7.19", {"start": v(382, -1080) * mm, "end": v(432, -1080) * mm});
            skLineSegment(sketch, "E4.9.7.19", {"start": v(382, -1030) * mm, "end": v(382, -1080) * mm});
            skLineSegment(sketch, "E4.0.7.20", {"start": v(382, -1084) * mm, "end": v(432, -1084) * mm});
            skLineSegment(sketch, "E4.3.7.20", {"start": v(432, -1084) * mm, "end": v(432, -1134) * mm});
            skLineSegment(sketch, "E4.6.7.20", {"start": v(382, -1134) * mm, "end": v(432, -1134) * mm});
            skLineSegment(sketch, "E4.9.7.20", {"start": v(382, -1084) * mm, "end": v(382, -1134) * mm});
            skLineSegment(sketch, "E4.0.7.21", {"start": v(382, -1138) * mm, "end": v(432, -1138) * mm});
            skLineSegment(sketch, "E4.3.7.21", {"start": v(432, -1138) * mm, "end": v(432, -1188) * mm});
            skLineSegment(sketch, "E4.6.7.21", {"start": v(382, -1188) * mm, "end": v(432, -1188) * mm});
            skLineSegment(sketch, "E4.9.7.21", {"start": v(382, -1138) * mm, "end": v(382, -1188) * mm});
            skLineSegment(sketch, "E4.0.7.22", {"start": v(382, -1192) * mm, "end": v(432, -1192) * mm});
            skLineSegment(sketch, "E4.3.7.22", {"start": v(432, -1192) * mm, "end": v(432, -1242) * mm});
            skLineSegment(sketch, "E4.6.7.22", {"start": v(382, -1242) * mm, "end": v(432, -1242) * mm});
            skLineSegment(sketch, "E4.9.7.22", {"start": v(382, -1192) * mm, "end": v(382, -1242) * mm});
            skLineSegment(sketch, "E4.0.7.23", {"start": v(382, -1246) * mm, "end": v(432, -1246) * mm});
            skLineSegment(sketch, "E4.3.7.23", {"start": v(432, -1246) * mm, "end": v(432, -1296) * mm});
            skLineSegment(sketch, "E4.6.7.23", {"start": v(382, -1296) * mm, "end": v(432, -1296) * mm});
            skLineSegment(sketch, "E4.9.7.23", {"start": v(382, -1246) * mm, "end": v(382, -1296) * mm});
            skLineSegment(sketch, "E4.0.7.24", {"start": v(382, -1300) * mm, "end": v(432, -1300) * mm});
            skLineSegment(sketch, "E4.3.7.24", {"start": v(432, -1300) * mm, "end": v(432, -1350) * mm});
            skLineSegment(sketch, "E4.6.7.24", {"start": v(382, -1350) * mm, "end": v(432, -1350) * mm});
            skLineSegment(sketch, "E4.9.7.24", {"start": v(382, -1300) * mm, "end": v(382, -1350) * mm});
            skLineSegment(sketch, "E4.0.7.25", {"start": v(382, -1354) * mm, "end": v(432, -1354) * mm});
            skLineSegment(sketch, "E4.3.7.25", {"start": v(432, -1354) * mm, "end": v(432, -1404) * mm});
            skLineSegment(sketch, "E4.6.7.25", {"start": v(382, -1404) * mm, "end": v(432, -1404) * mm});
            skLineSegment(sketch, "E4.9.7.25", {"start": v(382, -1354) * mm, "end": v(382, -1404) * mm});
            skLineSegment(sketch, "E5.0.8.0", {"start": v(436, -4) * mm, "end": v(486, -4) * mm});
            skLineSegment(sketch, "E5.3.8.0", {"start": v(486, -4) * mm, "end": v(486, -54) * mm});
            skLineSegment(sketch, "E5.6.8.0", {"start": v(436, -54) * mm, "end": v(486, -54) * mm});
            skLineSegment(sketch, "E5.9.8.0", {"start": v(436, -4) * mm, "end": v(436, -54) * mm});
            skLineSegment(sketch, "E5.0.8.1", {"start": v(436, -58) * mm, "end": v(486, -58) * mm});
            skLineSegment(sketch, "E5.3.8.1", {"start": v(486, -58) * mm, "end": v(486, -108) * mm});
            skLineSegment(sketch, "E5.6.8.1", {"start": v(436, -108) * mm, "end": v(486, -108) * mm});
            skLineSegment(sketch, "E5.9.8.1", {"start": v(436, -58) * mm, "end": v(436, -108) * mm});
            skLineSegment(sketch, "E5.0.8.2", {"start": v(436, -112) * mm, "end": v(486, -112) * mm});
            skLineSegment(sketch, "E5.3.8.2", {"start": v(486, -112) * mm, "end": v(486, -162) * mm});
            skLineSegment(sketch, "E5.6.8.2", {"start": v(436, -162) * mm, "end": v(486, -162) * mm});
            skLineSegment(sketch, "E5.9.8.2", {"start": v(436, -112) * mm, "end": v(436, -162) * mm});
            skLineSegment(sketch, "E5.0.8.3", {"start": v(436, -166) * mm, "end": v(486, -166) * mm});
            skLineSegment(sketch, "E5.3.8.3", {"start": v(486, -166) * mm, "end": v(486, -216) * mm});
            skLineSegment(sketch, "E5.6.8.3", {"start": v(436, -216) * mm, "end": v(486, -216) * mm});
            skLineSegment(sketch, "E5.9.8.3", {"start": v(436, -166) * mm, "end": v(436, -216) * mm});
            skLineSegment(sketch, "E5.0.8.4", {"start": v(436, -220) * mm, "end": v(486, -220) * mm});
            skLineSegment(sketch, "E5.3.8.4", {"start": v(486, -220) * mm, "end": v(486, -270) * mm});
            skLineSegment(sketch, "E5.6.8.4", {"start": v(436, -270) * mm, "end": v(486, -270) * mm});
            skLineSegment(sketch, "E5.9.8.4", {"start": v(436, -220) * mm, "end": v(436, -270) * mm});
            skLineSegment(sketch, "E5.0.8.5", {"start": v(436, -274) * mm, "end": v(486, -274) * mm});
            skLineSegment(sketch, "E5.3.8.5", {"start": v(486, -274) * mm, "end": v(486, -324) * mm});
            skLineSegment(sketch, "E5.6.8.5", {"start": v(436, -324) * mm, "end": v(486, -324) * mm});
            skLineSegment(sketch, "E5.9.8.5", {"start": v(436, -274) * mm, "end": v(436, -324) * mm});
            skLineSegment(sketch, "E5.0.8.6", {"start": v(436, -328) * mm, "end": v(486, -328) * mm});
            skLineSegment(sketch, "E5.3.8.6", {"start": v(486, -328) * mm, "end": v(486, -378) * mm});
            skLineSegment(sketch, "E5.6.8.6", {"start": v(436, -378) * mm, "end": v(486, -378) * mm});
            skLineSegment(sketch, "E5.9.8.6", {"start": v(436, -328) * mm, "end": v(436, -378) * mm});
            skLineSegment(sketch, "E5.0.8.7", {"start": v(436, -382) * mm, "end": v(486, -382) * mm});
            skLineSegment(sketch, "E5.3.8.7", {"start": v(486, -382) * mm, "end": v(486, -432) * mm});
            skLineSegment(sketch, "E5.6.8.7", {"start": v(436, -432) * mm, "end": v(486, -432) * mm});
            skLineSegment(sketch, "E5.9.8.7", {"start": v(436, -382) * mm, "end": v(436, -432) * mm});
            skLineSegment(sketch, "E5.0.8.8", {"start": v(436, -436) * mm, "end": v(486, -436) * mm});
            skLineSegment(sketch, "E5.3.8.8", {"start": v(486, -436) * mm, "end": v(486, -486) * mm});
            skLineSegment(sketch, "E5.6.8.8", {"start": v(436, -486) * mm, "end": v(486, -486) * mm});
            skLineSegment(sketch, "E5.9.8.8", {"start": v(436, -436) * mm, "end": v(436, -486) * mm});
            skLineSegment(sketch, "E5.0.8.9", {"start": v(436, -490) * mm, "end": v(486, -490) * mm});
            skLineSegment(sketch, "E5.3.8.9", {"start": v(486, -490) * mm, "end": v(486, -540) * mm});
            skLineSegment(sketch, "E5.6.8.9", {"start": v(436, -540) * mm, "end": v(486, -540) * mm});
            skLineSegment(sketch, "E5.9.8.9", {"start": v(436, -490) * mm, "end": v(436, -540) * mm});
            skLineSegment(sketch, "E5.0.8.10", {"start": v(436, -544) * mm, "end": v(486, -544) * mm});
            skLineSegment(sketch, "E5.3.8.10", {"start": v(486, -544) * mm, "end": v(486, -594) * mm});
            skLineSegment(sketch, "E5.6.8.10", {"start": v(436, -594) * mm, "end": v(486, -594) * mm});
            skLineSegment(sketch, "E5.9.8.10", {"start": v(436, -544) * mm, "end": v(436, -594) * mm});
            skLineSegment(sketch, "E5.0.8.11", {"start": v(436, -598) * mm, "end": v(486, -598) * mm});
            skLineSegment(sketch, "E5.3.8.11", {"start": v(486, -598) * mm, "end": v(486, -648) * mm});
            skLineSegment(sketch, "E5.6.8.11", {"start": v(436, -648) * mm, "end": v(486, -648) * mm});
            skLineSegment(sketch, "E5.9.8.11", {"start": v(436, -598) * mm, "end": v(436, -648) * mm});
            skLineSegment(sketch, "E5.0.8.12", {"start": v(436, -652) * mm, "end": v(486, -652) * mm});
            skLineSegment(sketch, "E5.3.8.12", {"start": v(486, -652) * mm, "end": v(486, -702) * mm});
            skLineSegment(sketch, "E5.6.8.12", {"start": v(436, -702) * mm, "end": v(486, -702) * mm});
            skLineSegment(sketch, "E5.9.8.12", {"start": v(436, -652) * mm, "end": v(436, -702) * mm});
            skLineSegment(sketch, "E5.0.8.13", {"start": v(436, -706) * mm, "end": v(486, -706) * mm});
            skLineSegment(sketch, "E5.3.8.13", {"start": v(486, -706) * mm, "end": v(486, -756) * mm});
            skLineSegment(sketch, "E5.6.8.13", {"start": v(436, -756) * mm, "end": v(486, -756) * mm});
            skLineSegment(sketch, "E5.9.8.13", {"start": v(436, -706) * mm, "end": v(436, -756) * mm});
            skLineSegment(sketch, "E5.0.8.14", {"start": v(436, -760) * mm, "end": v(486, -760) * mm});
            skLineSegment(sketch, "E5.3.8.14", {"start": v(486, -760) * mm, "end": v(486, -810) * mm});
            skLineSegment(sketch, "E5.6.8.14", {"start": v(436, -810) * mm, "end": v(486, -810) * mm});
            skLineSegment(sketch, "E5.9.8.14", {"start": v(436, -760) * mm, "end": v(436, -810) * mm});
            skLineSegment(sketch, "E5.0.8.15", {"start": v(436, -814) * mm, "end": v(486, -814) * mm});
            skLineSegment(sketch, "E5.3.8.15", {"start": v(486, -814) * mm, "end": v(486, -864) * mm});
            skLineSegment(sketch, "E5.6.8.15", {"start": v(436, -864) * mm, "end": v(486, -864) * mm});
            skLineSegment(sketch, "E5.9.8.15", {"start": v(436, -814) * mm, "end": v(436, -864) * mm});
            skLineSegment(sketch, "E5.0.8.16", {"start": v(436, -868) * mm, "end": v(486, -868) * mm});
            skLineSegment(sketch, "E5.3.8.16", {"start": v(486, -868) * mm, "end": v(486, -918) * mm});
            skLineSegment(sketch, "E5.6.8.16", {"start": v(436, -918) * mm, "end": v(486, -918) * mm});
            skLineSegment(sketch, "E5.9.8.16", {"start": v(436, -868) * mm, "end": v(436, -918) * mm});
            skLineSegment(sketch, "E5.0.8.17", {"start": v(436, -922) * mm, "end": v(486, -922) * mm});
            skLineSegment(sketch, "E5.3.8.17", {"start": v(486, -922) * mm, "end": v(486, -972) * mm});
            skLineSegment(sketch, "E5.6.8.17", {"start": v(436, -972) * mm, "end": v(486, -972) * mm});
            skLineSegment(sketch, "E5.9.8.17", {"start": v(436, -922) * mm, "end": v(436, -972) * mm});
            skLineSegment(sketch, "E5.0.8.18", {"start": v(436, -976) * mm, "end": v(486, -976) * mm});
            skLineSegment(sketch, "E5.3.8.18", {"start": v(486, -976) * mm, "end": v(486, -1026) * mm});
            skLineSegment(sketch, "E5.6.8.18", {"start": v(436, -1026) * mm, "end": v(486, -1026) * mm});
            skLineSegment(sketch, "E5.9.8.18", {"start": v(436, -976) * mm, "end": v(436, -1026) * mm});
            skLineSegment(sketch, "E5.0.8.19", {"start": v(436, -1030) * mm, "end": v(486, -1030) * mm});
            skLineSegment(sketch, "E5.3.8.19", {"start": v(486, -1030) * mm, "end": v(486, -1080) * mm});
            skLineSegment(sketch, "E5.6.8.19", {"start": v(436, -1080) * mm, "end": v(486, -1080) * mm});
            skLineSegment(sketch, "E5.9.8.19", {"start": v(436, -1030) * mm, "end": v(436, -1080) * mm});
            skLineSegment(sketch, "E5.0.8.20", {"start": v(436, -1084) * mm, "end": v(486, -1084) * mm});
            skLineSegment(sketch, "E5.3.8.20", {"start": v(486, -1084) * mm, "end": v(486, -1134) * mm});
            skLineSegment(sketch, "E5.6.8.20", {"start": v(436, -1134) * mm, "end": v(486, -1134) * mm});
            skLineSegment(sketch, "E5.9.8.20", {"start": v(436, -1084) * mm, "end": v(436, -1134) * mm});
            skLineSegment(sketch, "E5.0.8.21", {"start": v(436, -1138) * mm, "end": v(486, -1138) * mm});
            skLineSegment(sketch, "E5.3.8.21", {"start": v(486, -1138) * mm, "end": v(486, -1188) * mm});
            skLineSegment(sketch, "E5.6.8.21", {"start": v(436, -1188) * mm, "end": v(486, -1188) * mm});
            skLineSegment(sketch, "E5.9.8.21", {"start": v(436, -1138) * mm, "end": v(436, -1188) * mm});
            skLineSegment(sketch, "E5.0.8.22", {"start": v(436, -1192) * mm, "end": v(486, -1192) * mm});
            skLineSegment(sketch, "E5.3.8.22", {"start": v(486, -1192) * mm, "end": v(486, -1242) * mm});
            skLineSegment(sketch, "E5.6.8.22", {"start": v(436, -1242) * mm, "end": v(486, -1242) * mm});
            skLineSegment(sketch, "E5.9.8.22", {"start": v(436, -1192) * mm, "end": v(436, -1242) * mm});
            skLineSegment(sketch, "E5.0.8.23", {"start": v(436, -1246) * mm, "end": v(486, -1246) * mm});
            skLineSegment(sketch, "E5.3.8.23", {"start": v(486, -1246) * mm, "end": v(486, -1296) * mm});
            skLineSegment(sketch, "E5.6.8.23", {"start": v(436, -1296) * mm, "end": v(486, -1296) * mm});
            skLineSegment(sketch, "E5.9.8.23", {"start": v(436, -1246) * mm, "end": v(436, -1296) * mm});
            skLineSegment(sketch, "E5.0.8.24", {"start": v(436, -1300) * mm, "end": v(486, -1300) * mm});
            skLineSegment(sketch, "E5.3.8.24", {"start": v(486, -1300) * mm, "end": v(486, -1350) * mm});
            skLineSegment(sketch, "E5.6.8.24", {"start": v(436, -1350) * mm, "end": v(486, -1350) * mm});
            skLineSegment(sketch, "E5.9.8.24", {"start": v(436, -1300) * mm, "end": v(436, -1350) * mm});
            skLineSegment(sketch, "E5.0.8.25", {"start": v(436, -1354) * mm, "end": v(486, -1354) * mm});
            skLineSegment(sketch, "E5.3.8.25", {"start": v(486, -1354) * mm, "end": v(486, -1404) * mm});
            skLineSegment(sketch, "E5.6.8.25", {"start": v(436, -1404) * mm, "end": v(486, -1404) * mm});
            skLineSegment(sketch, "E5.9.8.25", {"start": v(436, -1354) * mm, "end": v(436, -1404) * mm});
            skLineSegment(sketch, "E6.0.9.0", {"start": v(490, -4) * mm, "end": v(540, -4) * mm});
            skLineSegment(sketch, "E6.3.9.0", {"start": v(540, -4) * mm, "end": v(540, -54) * mm});
            skLineSegment(sketch, "E6.6.9.0", {"start": v(490, -54) * mm, "end": v(540, -54) * mm});
            skLineSegment(sketch, "E6.9.9.0", {"start": v(490, -4) * mm, "end": v(490, -54) * mm});
            skLineSegment(sketch, "E6.0.9.1", {"start": v(490, -58) * mm, "end": v(540, -58) * mm});
            skLineSegment(sketch, "E6.3.9.1", {"start": v(540, -58) * mm, "end": v(540, -108) * mm});
            skLineSegment(sketch, "E6.6.9.1", {"start": v(490, -108) * mm, "end": v(540, -108) * mm});
            skLineSegment(sketch, "E6.9.9.1", {"start": v(490, -58) * mm, "end": v(490, -108) * mm});
            skLineSegment(sketch, "E6.0.9.2", {"start": v(490, -112) * mm, "end": v(540, -112) * mm});
            skLineSegment(sketch, "E6.3.9.2", {"start": v(540, -112) * mm, "end": v(540, -162) * mm});
            skLineSegment(sketch, "E6.6.9.2", {"start": v(490, -162) * mm, "end": v(540, -162) * mm});
            skLineSegment(sketch, "E6.9.9.2", {"start": v(490, -112) * mm, "end": v(490, -162) * mm});
            skLineSegment(sketch, "E6.0.9.3", {"start": v(490, -166) * mm, "end": v(540, -166) * mm});
            skLineSegment(sketch, "E6.3.9.3", {"start": v(540, -166) * mm, "end": v(540, -216) * mm});
            skLineSegment(sketch, "E6.6.9.3", {"start": v(490, -216) * mm, "end": v(540, -216) * mm});
            skLineSegment(sketch, "E6.9.9.3", {"start": v(490, -166) * mm, "end": v(490, -216) * mm});
            skLineSegment(sketch, "E6.0.9.4", {"start": v(490, -220) * mm, "end": v(540, -220) * mm});
            skLineSegment(sketch, "E6.3.9.4", {"start": v(540, -220) * mm, "end": v(540, -270) * mm});
            skLineSegment(sketch, "E6.6.9.4", {"start": v(490, -270) * mm, "end": v(540, -270) * mm});
            skLineSegment(sketch, "E6.9.9.4", {"start": v(490, -220) * mm, "end": v(490, -270) * mm});
            skLineSegment(sketch, "E6.0.9.5", {"start": v(490, -274) * mm, "end": v(540, -274) * mm});
            skLineSegment(sketch, "E6.3.9.5", {"start": v(540, -274) * mm, "end": v(540, -324) * mm});
            skLineSegment(sketch, "E6.6.9.5", {"start": v(490, -324) * mm, "end": v(540, -324) * mm});
            skLineSegment(sketch, "E6.9.9.5", {"start": v(490, -274) * mm, "end": v(490, -324) * mm});
            skLineSegment(sketch, "E6.0.9.6", {"start": v(490, -328) * mm, "end": v(540, -328) * mm});
            skLineSegment(sketch, "E6.3.9.6", {"start": v(540, -328) * mm, "end": v(540, -378) * mm});
            skLineSegment(sketch, "E6.6.9.6", {"start": v(490, -378) * mm, "end": v(540, -378) * mm});
            skLineSegment(sketch, "E6.9.9.6", {"start": v(490, -328) * mm, "end": v(490, -378) * mm});
            skLineSegment(sketch, "E6.0.9.7", {"start": v(490, -382) * mm, "end": v(540, -382) * mm});
            skLineSegment(sketch, "E6.3.9.7", {"start": v(540, -382) * mm, "end": v(540, -432) * mm});
            skLineSegment(sketch, "E6.6.9.7", {"start": v(490, -432) * mm, "end": v(540, -432) * mm});
            skLineSegment(sketch, "E6.9.9.7", {"start": v(490, -382) * mm, "end": v(490, -432) * mm});
            skLineSegment(sketch, "E6.0.9.8", {"start": v(490, -436) * mm, "end": v(540, -436) * mm});
            skLineSegment(sketch, "E6.3.9.8", {"start": v(540, -436) * mm, "end": v(540, -486) * mm});
            skLineSegment(sketch, "E6.6.9.8", {"start": v(490, -486) * mm, "end": v(540, -486) * mm});
            skLineSegment(sketch, "E6.9.9.8", {"start": v(490, -436) * mm, "end": v(490, -486) * mm});
            skLineSegment(sketch, "E6.0.9.9", {"start": v(490, -490) * mm, "end": v(540, -490) * mm});
            skLineSegment(sketch, "E6.3.9.9", {"start": v(540, -490) * mm, "end": v(540, -540) * mm});
            skLineSegment(sketch, "E6.6.9.9", {"start": v(490, -540) * mm, "end": v(540, -540) * mm});
            skLineSegment(sketch, "E6.9.9.9", {"start": v(490, -490) * mm, "end": v(490, -540) * mm});
            skLineSegment(sketch, "E6.0.9.10", {"start": v(490, -544) * mm, "end": v(540, -544) * mm});
            skLineSegment(sketch, "E6.3.9.10", {"start": v(540, -544) * mm, "end": v(540, -594) * mm});
            skLineSegment(sketch, "E6.6.9.10", {"start": v(490, -594) * mm, "end": v(540, -594) * mm});
            skLineSegment(sketch, "E6.9.9.10", {"start": v(490, -544) * mm, "end": v(490, -594) * mm});
            skLineSegment(sketch, "E6.0.9.11", {"start": v(490, -598) * mm, "end": v(540, -598) * mm});
            skLineSegment(sketch, "E6.3.9.11", {"start": v(540, -598) * mm, "end": v(540, -648) * mm});
            skLineSegment(sketch, "E6.6.9.11", {"start": v(490, -648) * mm, "end": v(540, -648) * mm});
            skLineSegment(sketch, "E6.9.9.11", {"start": v(490, -598) * mm, "end": v(490, -648) * mm});
            skLineSegment(sketch, "E6.0.9.12", {"start": v(490, -652) * mm, "end": v(540, -652) * mm});
            skLineSegment(sketch, "E6.3.9.12", {"start": v(540, -652) * mm, "end": v(540, -702) * mm});
            skLineSegment(sketch, "E6.6.9.12", {"start": v(490, -702) * mm, "end": v(540, -702) * mm});
            skLineSegment(sketch, "E6.9.9.12", {"start": v(490, -652) * mm, "end": v(490, -702) * mm});
            skLineSegment(sketch, "E6.0.9.13", {"start": v(490, -706) * mm, "end": v(540, -706) * mm});
            skLineSegment(sketch, "E6.3.9.13", {"start": v(540, -706) * mm, "end": v(540, -756) * mm});
            skLineSegment(sketch, "E6.6.9.13", {"start": v(490, -756) * mm, "end": v(540, -756) * mm});
            skLineSegment(sketch, "E6.9.9.13", {"start": v(490, -706) * mm, "end": v(490, -756) * mm});
            skLineSegment(sketch, "E6.0.9.14", {"start": v(490, -760) * mm, "end": v(540, -760) * mm});
            skLineSegment(sketch, "E6.3.9.14", {"start": v(540, -760) * mm, "end": v(540, -810) * mm});
            skLineSegment(sketch, "E6.6.9.14", {"start": v(490, -810) * mm, "end": v(540, -810) * mm});
            skLineSegment(sketch, "E6.9.9.14", {"start": v(490, -760) * mm, "end": v(490, -810) * mm});
            skLineSegment(sketch, "E6.0.9.15", {"start": v(490, -814) * mm, "end": v(540, -814) * mm});
            skLineSegment(sketch, "E6.3.9.15", {"start": v(540, -814) * mm, "end": v(540, -864) * mm});
            skLineSegment(sketch, "E6.6.9.15", {"start": v(490, -864) * mm, "end": v(540, -864) * mm});
            skLineSegment(sketch, "E6.9.9.15", {"start": v(490, -814) * mm, "end": v(490, -864) * mm});
            skLineSegment(sketch, "E6.0.9.16", {"start": v(490, -868) * mm, "end": v(540, -868) * mm});
            skLineSegment(sketch, "E6.3.9.16", {"start": v(540, -868) * mm, "end": v(540, -918) * mm});
            skLineSegment(sketch, "E6.6.9.16", {"start": v(490, -918) * mm, "end": v(540, -918) * mm});
            skLineSegment(sketch, "E6.9.9.16", {"start": v(490, -868) * mm, "end": v(490, -918) * mm});
            skLineSegment(sketch, "E6.0.9.17", {"start": v(490, -922) * mm, "end": v(540, -922) * mm});
            skLineSegment(sketch, "E6.3.9.17", {"start": v(540, -922) * mm, "end": v(540, -972) * mm});
            skLineSegment(sketch, "E6.6.9.17", {"start": v(490, -972) * mm, "end": v(540, -972) * mm});
            skLineSegment(sketch, "E6.9.9.17", {"start": v(490, -922) * mm, "end": v(490, -972) * mm});
            skLineSegment(sketch, "E6.0.9.18", {"start": v(490, -976) * mm, "end": v(540, -976) * mm});
            skLineSegment(sketch, "E6.3.9.18", {"start": v(540, -976) * mm, "end": v(540, -1026) * mm});
            skLineSegment(sketch, "E6.6.9.18", {"start": v(490, -1026) * mm, "end": v(540, -1026) * mm});
            skLineSegment(sketch, "E6.9.9.18", {"start": v(490, -976) * mm, "end": v(490, -1026) * mm});
            skLineSegment(sketch, "E6.0.9.19", {"start": v(490, -1030) * mm, "end": v(540, -1030) * mm});
            skLineSegment(sketch, "E6.3.9.19", {"start": v(540, -1030) * mm, "end": v(540, -1080) * mm});
            skLineSegment(sketch, "E6.6.9.19", {"start": v(490, -1080) * mm, "end": v(540, -1080) * mm});
            skLineSegment(sketch, "E6.9.9.19", {"start": v(490, -1030) * mm, "end": v(490, -1080) * mm});
            skLineSegment(sketch, "E6.0.9.20", {"start": v(490, -1084) * mm, "end": v(540, -1084) * mm});
            skLineSegment(sketch, "E6.3.9.20", {"start": v(540, -1084) * mm, "end": v(540, -1134) * mm});
            skLineSegment(sketch, "E6.6.9.20", {"start": v(490, -1134) * mm, "end": v(540, -1134) * mm});
            skLineSegment(sketch, "E6.9.9.20", {"start": v(490, -1084) * mm, "end": v(490, -1134) * mm});
            skLineSegment(sketch, "E6.0.9.21", {"start": v(490, -1138) * mm, "end": v(540, -1138) * mm});
            skLineSegment(sketch, "E6.3.9.21", {"start": v(540, -1138) * mm, "end": v(540, -1188) * mm});
            skLineSegment(sketch, "E6.6.9.21", {"start": v(490, -1188) * mm, "end": v(540, -1188) * mm});
            skLineSegment(sketch, "E6.9.9.21", {"start": v(490, -1138) * mm, "end": v(490, -1188) * mm});
            skLineSegment(sketch, "E6.0.9.22", {"start": v(490, -1192) * mm, "end": v(540, -1192) * mm});
            skLineSegment(sketch, "E6.3.9.22", {"start": v(540, -1192) * mm, "end": v(540, -1242) * mm});
            skLineSegment(sketch, "E6.6.9.22", {"start": v(490, -1242) * mm, "end": v(540, -1242) * mm});
            skLineSegment(sketch, "E6.9.9.22", {"start": v(490, -1192) * mm, "end": v(490, -1242) * mm});
            skLineSegment(sketch, "E6.0.9.23", {"start": v(490, -1246) * mm, "end": v(540, -1246) * mm});
            skLineSegment(sketch, "E6.3.9.23", {"start": v(540, -1246) * mm, "end": v(540, -1296) * mm});
            skLineSegment(sketch, "E6.6.9.23", {"start": v(490, -1296) * mm, "end": v(540, -1296) * mm});
            skLineSegment(sketch, "E6.9.9.23", {"start": v(490, -1246) * mm, "end": v(490, -1296) * mm});
            skLineSegment(sketch, "E6.0.9.24", {"start": v(490, -1300) * mm, "end": v(540, -1300) * mm});
            skLineSegment(sketch, "E6.3.9.24", {"start": v(540, -1300) * mm, "end": v(540, -1350) * mm});
            skLineSegment(sketch, "E6.6.9.24", {"start": v(490, -1350) * mm, "end": v(540, -1350) * mm});
            skLineSegment(sketch, "E6.9.9.24", {"start": v(490, -1300) * mm, "end": v(490, -1350) * mm});
            skLineSegment(sketch, "E6.0.9.25", {"start": v(490, -1354) * mm, "end": v(540, -1354) * mm});
            skLineSegment(sketch, "E6.3.9.25", {"start": v(540, -1354) * mm, "end": v(540, -1404) * mm});
            skLineSegment(sketch, "E6.6.9.25", {"start": v(490, -1404) * mm, "end": v(540, -1404) * mm});
            skLineSegment(sketch, "E6.9.9.25", {"start": v(490, -1354) * mm, "end": v(490, -1404) * mm});
            skLineSegment(sketch, "E7.0.10.0", {"start": v(544, -4) * mm, "end": v(594, -4) * mm});
            skLineSegment(sketch, "E7.3.10.0", {"start": v(594, -4) * mm, "end": v(594, -54) * mm});
            skLineSegment(sketch, "E7.6.10.0", {"start": v(544, -54) * mm, "end": v(594, -54) * mm});
            skLineSegment(sketch, "E7.9.10.0", {"start": v(544, -4) * mm, "end": v(544, -54) * mm});
            skLineSegment(sketch, "E7.0.10.1", {"start": v(544, -58) * mm, "end": v(594, -58) * mm});
            skLineSegment(sketch, "E7.3.10.1", {"start": v(594, -58) * mm, "end": v(594, -108) * mm});
            skLineSegment(sketch, "E7.6.10.1", {"start": v(544, -108) * mm, "end": v(594, -108) * mm});
            skLineSegment(sketch, "E7.9.10.1", {"start": v(544, -58) * mm, "end": v(544, -108) * mm});
            skLineSegment(sketch, "E7.0.10.2", {"start": v(544, -112) * mm, "end": v(594, -112) * mm});
            skLineSegment(sketch, "E7.3.10.2", {"start": v(594, -112) * mm, "end": v(594, -162) * mm});
            skLineSegment(sketch, "E7.6.10.2", {"start": v(544, -162) * mm, "end": v(594, -162) * mm});
            skLineSegment(sketch, "E7.9.10.2", {"start": v(544, -112) * mm, "end": v(544, -162) * mm});
            skLineSegment(sketch, "E7.0.10.3", {"start": v(544, -166) * mm, "end": v(594, -166) * mm});
            skLineSegment(sketch, "E7.3.10.3", {"start": v(594, -166) * mm, "end": v(594, -216) * mm});
            skLineSegment(sketch, "E7.6.10.3", {"start": v(544, -216) * mm, "end": v(594, -216) * mm});
            skLineSegment(sketch, "E7.9.10.3", {"start": v(544, -166) * mm, "end": v(544, -216) * mm});
            skLineSegment(sketch, "E7.0.10.4", {"start": v(544, -220) * mm, "end": v(594, -220) * mm});
            skLineSegment(sketch, "E7.3.10.4", {"start": v(594, -220) * mm, "end": v(594, -270) * mm});
            skLineSegment(sketch, "E7.6.10.4", {"start": v(544, -270) * mm, "end": v(594, -270) * mm});
            skLineSegment(sketch, "E7.9.10.4", {"start": v(544, -220) * mm, "end": v(544, -270) * mm});
            skLineSegment(sketch, "E7.0.10.5", {"start": v(544, -274) * mm, "end": v(594, -274) * mm});
            skLineSegment(sketch, "E7.3.10.5", {"start": v(594, -274) * mm, "end": v(594, -324) * mm});
            skLineSegment(sketch, "E7.6.10.5", {"start": v(544, -324) * mm, "end": v(594, -324) * mm});
            skLineSegment(sketch, "E7.9.10.5", {"start": v(544, -274) * mm, "end": v(544, -324) * mm});
            skLineSegment(sketch, "E7.0.10.6", {"start": v(544, -328) * mm, "end": v(594, -328) * mm});
            skLineSegment(sketch, "E7.3.10.6", {"start": v(594, -328) * mm, "end": v(594, -378) * mm});
            skLineSegment(sketch, "E7.6.10.6", {"start": v(544, -378) * mm, "end": v(594, -378) * mm});
            skLineSegment(sketch, "E7.9.10.6", {"start": v(544, -328) * mm, "end": v(544, -378) * mm});
            skLineSegment(sketch, "E7.0.10.7", {"start": v(544, -382) * mm, "end": v(594, -382) * mm});
            skLineSegment(sketch, "E7.3.10.7", {"start": v(594, -382) * mm, "end": v(594, -432) * mm});
            skLineSegment(sketch, "E7.6.10.7", {"start": v(544, -432) * mm, "end": v(594, -432) * mm});
            skLineSegment(sketch, "E7.9.10.7", {"start": v(544, -382) * mm, "end": v(544, -432) * mm});
            skLineSegment(sketch, "E7.0.10.8", {"start": v(544, -436) * mm, "end": v(594, -436) * mm});
            skLineSegment(sketch, "E7.3.10.8", {"start": v(594, -436) * mm, "end": v(594, -486) * mm});
            skLineSegment(sketch, "E7.6.10.8", {"start": v(544, -486) * mm, "end": v(594, -486) * mm});
            skLineSegment(sketch, "E7.9.10.8", {"start": v(544, -436) * mm, "end": v(544, -486) * mm});
            skLineSegment(sketch, "E7.0.10.9", {"start": v(544, -490) * mm, "end": v(594, -490) * mm});
            skLineSegment(sketch, "E7.3.10.9", {"start": v(594, -490) * mm, "end": v(594, -540) * mm});
            skLineSegment(sketch, "E7.6.10.9", {"start": v(544, -540) * mm, "end": v(594, -540) * mm});
            skLineSegment(sketch, "E7.9.10.9", {"start": v(544, -490) * mm, "end": v(544, -540) * mm});
            skLineSegment(sketch, "E7.0.10.10", {"start": v(544, -544) * mm, "end": v(594, -544) * mm});
            skLineSegment(sketch, "E7.3.10.10", {"start": v(594, -544) * mm, "end": v(594, -594) * mm});
            skLineSegment(sketch, "E7.6.10.10", {"start": v(544, -594) * mm, "end": v(594, -594) * mm});
            skLineSegment(sketch, "E7.9.10.10", {"start": v(544, -544) * mm, "end": v(544, -594) * mm});
            skLineSegment(sketch, "E7.0.10.11", {"start": v(544, -598) * mm, "end": v(594, -598) * mm});
            skLineSegment(sketch, "E7.3.10.11", {"start": v(594, -598) * mm, "end": v(594, -648) * mm});
            skLineSegment(sketch, "E7.6.10.11", {"start": v(544, -648) * mm, "end": v(594, -648) * mm});
            skLineSegment(sketch, "E7.9.10.11", {"start": v(544, -598) * mm, "end": v(544, -648) * mm});
            skLineSegment(sketch, "E7.0.10.12", {"start": v(544, -652) * mm, "end": v(594, -652) * mm});
            skLineSegment(sketch, "E7.3.10.12", {"start": v(594, -652) * mm, "end": v(594, -702) * mm});
            skLineSegment(sketch, "E7.6.10.12", {"start": v(544, -702) * mm, "end": v(594, -702) * mm});
            skLineSegment(sketch, "E7.9.10.12", {"start": v(544, -652) * mm, "end": v(544, -702) * mm});
            skLineSegment(sketch, "E7.0.10.13", {"start": v(544, -706) * mm, "end": v(594, -706) * mm});
            skLineSegment(sketch, "E7.3.10.13", {"start": v(594, -706) * mm, "end": v(594, -756) * mm});
            skLineSegment(sketch, "E7.6.10.13", {"start": v(544, -756) * mm, "end": v(594, -756) * mm});
            skLineSegment(sketch, "E7.9.10.13", {"start": v(544, -706) * mm, "end": v(544, -756) * mm});
            skLineSegment(sketch, "E7.0.10.14", {"start": v(544, -760) * mm, "end": v(594, -760) * mm});
            skLineSegment(sketch, "E7.3.10.14", {"start": v(594, -760) * mm, "end": v(594, -810) * mm});
            skLineSegment(sketch, "E7.6.10.14", {"start": v(544, -810) * mm, "end": v(594, -810) * mm});
            skLineSegment(sketch, "E7.9.10.14", {"start": v(544, -760) * mm, "end": v(544, -810) * mm});
            skLineSegment(sketch, "E7.0.10.15", {"start": v(544, -814) * mm, "end": v(594, -814) * mm});
            skLineSegment(sketch, "E7.3.10.15", {"start": v(594, -814) * mm, "end": v(594, -864) * mm});
            skLineSegment(sketch, "E7.6.10.15", {"start": v(544, -864) * mm, "end": v(594, -864) * mm});
            skLineSegment(sketch, "E7.9.10.15", {"start": v(544, -814) * mm, "end": v(544, -864) * mm});
            skLineSegment(sketch, "E7.0.10.16", {"start": v(544, -868) * mm, "end": v(594, -868) * mm});
            skLineSegment(sketch, "E7.3.10.16", {"start": v(594, -868) * mm, "end": v(594, -918) * mm});
            skLineSegment(sketch, "E7.6.10.16", {"start": v(544, -918) * mm, "end": v(594, -918) * mm});
            skLineSegment(sketch, "E7.9.10.16", {"start": v(544, -868) * mm, "end": v(544, -918) * mm});
            skLineSegment(sketch, "E7.0.10.17", {"start": v(544, -922) * mm, "end": v(594, -922) * mm});
            skLineSegment(sketch, "E7.3.10.17", {"start": v(594, -922) * mm, "end": v(594, -972) * mm});
            skLineSegment(sketch, "E7.6.10.17", {"start": v(544, -972) * mm, "end": v(594, -972) * mm});
            skLineSegment(sketch, "E7.9.10.17", {"start": v(544, -922) * mm, "end": v(544, -972) * mm});
            skLineSegment(sketch, "E7.0.10.18", {"start": v(544, -976) * mm, "end": v(594, -976) * mm});
            skLineSegment(sketch, "E7.3.10.18", {"start": v(594, -976) * mm, "end": v(594, -1026) * mm});
            skLineSegment(sketch, "E7.6.10.18", {"start": v(544, -1026) * mm, "end": v(594, -1026) * mm});
            skLineSegment(sketch, "E7.9.10.18", {"start": v(544, -976) * mm, "end": v(544, -1026) * mm});
            skLineSegment(sketch, "E7.0.10.19", {"start": v(544, -1030) * mm, "end": v(594, -1030) * mm});
            skLineSegment(sketch, "E7.3.10.19", {"start": v(594, -1030) * mm, "end": v(594, -1080) * mm});
            skLineSegment(sketch, "E7.6.10.19", {"start": v(544, -1080) * mm, "end": v(594, -1080) * mm});
            skLineSegment(sketch, "E7.9.10.19", {"start": v(544, -1030) * mm, "end": v(544, -1080) * mm});
            skLineSegment(sketch, "E7.0.10.20", {"start": v(544, -1084) * mm, "end": v(594, -1084) * mm});
            skLineSegment(sketch, "E7.3.10.20", {"start": v(594, -1084) * mm, "end": v(594, -1134) * mm});
            skLineSegment(sketch, "E7.6.10.20", {"start": v(544, -1134) * mm, "end": v(594, -1134) * mm});
            skLineSegment(sketch, "E7.9.10.20", {"start": v(544, -1084) * mm, "end": v(544, -1134) * mm});
            skLineSegment(sketch, "E7.0.10.21", {"start": v(544, -1138) * mm, "end": v(594, -1138) * mm});
            skLineSegment(sketch, "E7.3.10.21", {"start": v(594, -1138) * mm, "end": v(594, -1188) * mm});
            skLineSegment(sketch, "E7.6.10.21", {"start": v(544, -1188) * mm, "end": v(594, -1188) * mm});
            skLineSegment(sketch, "E7.9.10.21", {"start": v(544, -1138) * mm, "end": v(544, -1188) * mm});
            skLineSegment(sketch, "E7.0.10.22", {"start": v(544, -1192) * mm, "end": v(594, -1192) * mm});
            skLineSegment(sketch, "E7.3.10.22", {"start": v(594, -1192) * mm, "end": v(594, -1242) * mm});
            skLineSegment(sketch, "E7.6.10.22", {"start": v(544, -1242) * mm, "end": v(594, -1242) * mm});
            skLineSegment(sketch, "E7.9.10.22", {"start": v(544, -1192) * mm, "end": v(544, -1242) * mm});
            skLineSegment(sketch, "E7.0.10.23", {"start": v(544, -1246) * mm, "end": v(594, -1246) * mm});
            skLineSegment(sketch, "E7.3.10.23", {"start": v(594, -1246) * mm, "end": v(594, -1296) * mm});
            skLineSegment(sketch, "E7.6.10.23", {"start": v(544, -1296) * mm, "end": v(594, -1296) * mm});
            skLineSegment(sketch, "E7.9.10.23", {"start": v(544, -1246) * mm, "end": v(544, -1296) * mm});
            skLineSegment(sketch, "E7.0.10.24", {"start": v(544, -1300) * mm, "end": v(594, -1300) * mm});
            skLineSegment(sketch, "E7.3.10.24", {"start": v(594, -1300) * mm, "end": v(594, -1350) * mm});
            skLineSegment(sketch, "E7.6.10.24", {"start": v(544, -1350) * mm, "end": v(594, -1350) * mm});
            skLineSegment(sketch, "E7.9.10.24", {"start": v(544, -1300) * mm, "end": v(544, -1350) * mm});
            skLineSegment(sketch, "E7.0.10.25", {"start": v(544, -1354) * mm, "end": v(594, -1354) * mm});
            skLineSegment(sketch, "E7.3.10.25", {"start": v(594, -1354) * mm, "end": v(594, -1404) * mm});
            skLineSegment(sketch, "E7.6.10.25", {"start": v(544, -1404) * mm, "end": v(594, -1404) * mm});
            skLineSegment(sketch, "E7.9.10.25", {"start": v(544, -1354) * mm, "end": v(544, -1404) * mm});
            skLineSegment(sketch, "E8.0.11.0", {"start": v(598, -4) * mm, "end": v(648, -4) * mm});
            skLineSegment(sketch, "E8.3.11.0", {"start": v(648, -4) * mm, "end": v(648, -54) * mm});
            skLineSegment(sketch, "E8.6.11.0", {"start": v(598, -54) * mm, "end": v(648, -54) * mm});
            skLineSegment(sketch, "E8.9.11.0", {"start": v(598, -4) * mm, "end": v(598, -54) * mm});
            skLineSegment(sketch, "E8.0.11.1", {"start": v(598, -58) * mm, "end": v(648, -58) * mm});
            skLineSegment(sketch, "E8.3.11.1", {"start": v(648, -58) * mm, "end": v(648, -108) * mm});
            skLineSegment(sketch, "E8.6.11.1", {"start": v(598, -108) * mm, "end": v(648, -108) * mm});
            skLineSegment(sketch, "E8.9.11.1", {"start": v(598, -58) * mm, "end": v(598, -108) * mm});
            skLineSegment(sketch, "E8.0.11.2", {"start": v(598, -112) * mm, "end": v(648, -112) * mm});
            skLineSegment(sketch, "E8.3.11.2", {"start": v(648, -112) * mm, "end": v(648, -162) * mm});
            skLineSegment(sketch, "E8.6.11.2", {"start": v(598, -162) * mm, "end": v(648, -162) * mm});
            skLineSegment(sketch, "E8.9.11.2", {"start": v(598, -112) * mm, "end": v(598, -162) * mm});
            skLineSegment(sketch, "E8.0.11.3", {"start": v(598, -166) * mm, "end": v(648, -166) * mm});
            skLineSegment(sketch, "E8.3.11.3", {"start": v(648, -166) * mm, "end": v(648, -216) * mm});
            skLineSegment(sketch, "E8.6.11.3", {"start": v(598, -216) * mm, "end": v(648, -216) * mm});
            skLineSegment(sketch, "E8.9.11.3", {"start": v(598, -166) * mm, "end": v(598, -216) * mm});
            skLineSegment(sketch, "E8.0.11.4", {"start": v(598, -220) * mm, "end": v(648, -220) * mm});
            skLineSegment(sketch, "E8.3.11.4", {"start": v(648, -220) * mm, "end": v(648, -270) * mm});
            skLineSegment(sketch, "E8.6.11.4", {"start": v(598, -270) * mm, "end": v(648, -270) * mm});
            skLineSegment(sketch, "E8.9.11.4", {"start": v(598, -220) * mm, "end": v(598, -270) * mm});
            skLineSegment(sketch, "E8.0.11.5", {"start": v(598, -274) * mm, "end": v(648, -274) * mm});
            skLineSegment(sketch, "E8.3.11.5", {"start": v(648, -274) * mm, "end": v(648, -324) * mm});
            skLineSegment(sketch, "E8.6.11.5", {"start": v(598, -324) * mm, "end": v(648, -324) * mm});
            skLineSegment(sketch, "E8.9.11.5", {"start": v(598, -274) * mm, "end": v(598, -324) * mm});
            skLineSegment(sketch, "E8.0.11.6", {"start": v(598, -328) * mm, "end": v(648, -328) * mm});
            skLineSegment(sketch, "E8.3.11.6", {"start": v(648, -328) * mm, "end": v(648, -378) * mm});
            skLineSegment(sketch, "E8.6.11.6", {"start": v(598, -378) * mm, "end": v(648, -378) * mm});
            skLineSegment(sketch, "E8.9.11.6", {"start": v(598, -328) * mm, "end": v(598, -378) * mm});
            skLineSegment(sketch, "E8.0.11.7", {"start": v(598, -382) * mm, "end": v(648, -382) * mm});
            skLineSegment(sketch, "E8.3.11.7", {"start": v(648, -382) * mm, "end": v(648, -432) * mm});
            skLineSegment(sketch, "E8.6.11.7", {"start": v(598, -432) * mm, "end": v(648, -432) * mm});
            skLineSegment(sketch, "E8.9.11.7", {"start": v(598, -382) * mm, "end": v(598, -432) * mm});
            skLineSegment(sketch, "E8.0.11.8", {"start": v(598, -436) * mm, "end": v(648, -436) * mm});
            skLineSegment(sketch, "E8.3.11.8", {"start": v(648, -436) * mm, "end": v(648, -486) * mm});
            skLineSegment(sketch, "E8.6.11.8", {"start": v(598, -486) * mm, "end": v(648, -486) * mm});
            skLineSegment(sketch, "E8.9.11.8", {"start": v(598, -436) * mm, "end": v(598, -486) * mm});
            skLineSegment(sketch, "E8.0.11.9", {"start": v(598, -490) * mm, "end": v(648, -490) * mm});
            skLineSegment(sketch, "E8.3.11.9", {"start": v(648, -490) * mm, "end": v(648, -540) * mm});
            skLineSegment(sketch, "E8.6.11.9", {"start": v(598, -540) * mm, "end": v(648, -540) * mm});
            skLineSegment(sketch, "E8.9.11.9", {"start": v(598, -490) * mm, "end": v(598, -540) * mm});
            skLineSegment(sketch, "E8.0.11.10", {"start": v(598, -544) * mm, "end": v(648, -544) * mm});
            skLineSegment(sketch, "E8.3.11.10", {"start": v(648, -544) * mm, "end": v(648, -594) * mm});
            skLineSegment(sketch, "E8.6.11.10", {"start": v(598, -594) * mm, "end": v(648, -594) * mm});
            skLineSegment(sketch, "E8.9.11.10", {"start": v(598, -544) * mm, "end": v(598, -594) * mm});
            skLineSegment(sketch, "E8.0.11.11", {"start": v(598, -598) * mm, "end": v(648, -598) * mm});
            skLineSegment(sketch, "E8.3.11.11", {"start": v(648, -598) * mm, "end": v(648, -648) * mm});
            skLineSegment(sketch, "E8.6.11.11", {"start": v(598, -648) * mm, "end": v(648, -648) * mm});
            skLineSegment(sketch, "E8.9.11.11", {"start": v(598, -598) * mm, "end": v(598, -648) * mm});
            skLineSegment(sketch, "E8.0.11.12", {"start": v(598, -652) * mm, "end": v(648, -652) * mm});
            skLineSegment(sketch, "E8.3.11.12", {"start": v(648, -652) * mm, "end": v(648, -702) * mm});
            skLineSegment(sketch, "E8.6.11.12", {"start": v(598, -702) * mm, "end": v(648, -702) * mm});
            skLineSegment(sketch, "E8.9.11.12", {"start": v(598, -652) * mm, "end": v(598, -702) * mm});
            skLineSegment(sketch, "E8.0.11.13", {"start": v(598, -706) * mm, "end": v(648, -706) * mm});
            skLineSegment(sketch, "E8.3.11.13", {"start": v(648, -706) * mm, "end": v(648, -756) * mm});
            skLineSegment(sketch, "E8.6.11.13", {"start": v(598, -756) * mm, "end": v(648, -756) * mm});
            skLineSegment(sketch, "E8.9.11.13", {"start": v(598, -706) * mm, "end": v(598, -756) * mm});
            skLineSegment(sketch, "E8.0.11.14", {"start": v(598, -760) * mm, "end": v(648, -760) * mm});
            skLineSegment(sketch, "E8.3.11.14", {"start": v(648, -760) * mm, "end": v(648, -810) * mm});
            skLineSegment(sketch, "E8.6.11.14", {"start": v(598, -810) * mm, "end": v(648, -810) * mm});
            skLineSegment(sketch, "E8.9.11.14", {"start": v(598, -760) * mm, "end": v(598, -810) * mm});
            skLineSegment(sketch, "E8.0.11.15", {"start": v(598, -814) * mm, "end": v(648, -814) * mm});
            skLineSegment(sketch, "E8.3.11.15", {"start": v(648, -814) * mm, "end": v(648, -864) * mm});
            skLineSegment(sketch, "E8.6.11.15", {"start": v(598, -864) * mm, "end": v(648, -864) * mm});
            skLineSegment(sketch, "E8.9.11.15", {"start": v(598, -814) * mm, "end": v(598, -864) * mm});
            skLineSegment(sketch, "E8.0.11.16", {"start": v(598, -868) * mm, "end": v(648, -868) * mm});
            skLineSegment(sketch, "E8.3.11.16", {"start": v(648, -868) * mm, "end": v(648, -918) * mm});
            skLineSegment(sketch, "E8.6.11.16", {"start": v(598, -918) * mm, "end": v(648, -918) * mm});
            skLineSegment(sketch, "E8.9.11.16", {"start": v(598, -868) * mm, "end": v(598, -918) * mm});
            skLineSegment(sketch, "E8.0.11.17", {"start": v(598, -922) * mm, "end": v(648, -922) * mm});
            skLineSegment(sketch, "E8.3.11.17", {"start": v(648, -922) * mm, "end": v(648, -972) * mm});
            skLineSegment(sketch, "E8.6.11.17", {"start": v(598, -972) * mm, "end": v(648, -972) * mm});
            skLineSegment(sketch, "E8.9.11.17", {"start": v(598, -922) * mm, "end": v(598, -972) * mm});
            skLineSegment(sketch, "E8.0.11.18", {"start": v(598, -976) * mm, "end": v(648, -976) * mm});
            skLineSegment(sketch, "E8.3.11.18", {"start": v(648, -976) * mm, "end": v(648, -1026) * mm});
            skLineSegment(sketch, "E8.6.11.18", {"start": v(598, -1026) * mm, "end": v(648, -1026) * mm});
            skLineSegment(sketch, "E8.9.11.18", {"start": v(598, -976) * mm, "end": v(598, -1026) * mm});
            skLineSegment(sketch, "E8.0.11.19", {"start": v(598, -1030) * mm, "end": v(648, -1030) * mm});
            skLineSegment(sketch, "E8.3.11.19", {"start": v(648, -1030) * mm, "end": v(648, -1080) * mm});
            skLineSegment(sketch, "E8.6.11.19", {"start": v(598, -1080) * mm, "end": v(648, -1080) * mm});
            skLineSegment(sketch, "E8.9.11.19", {"start": v(598, -1030) * mm, "end": v(598, -1080) * mm});
            skLineSegment(sketch, "E8.0.11.20", {"start": v(598, -1084) * mm, "end": v(648, -1084) * mm});
            skLineSegment(sketch, "E8.3.11.20", {"start": v(648, -1084) * mm, "end": v(648, -1134) * mm});
            skLineSegment(sketch, "E8.6.11.20", {"start": v(598, -1134) * mm, "end": v(648, -1134) * mm});
            skLineSegment(sketch, "E8.9.11.20", {"start": v(598, -1084) * mm, "end": v(598, -1134) * mm});
            skLineSegment(sketch, "E8.0.11.21", {"start": v(598, -1138) * mm, "end": v(648, -1138) * mm});
            skLineSegment(sketch, "E8.3.11.21", {"start": v(648, -1138) * mm, "end": v(648, -1188) * mm});
            skLineSegment(sketch, "E8.6.11.21", {"start": v(598, -1188) * mm, "end": v(648, -1188) * mm});
            skLineSegment(sketch, "E8.9.11.21", {"start": v(598, -1138) * mm, "end": v(598, -1188) * mm});
            skLineSegment(sketch, "E8.0.11.22", {"start": v(598, -1192) * mm, "end": v(648, -1192) * mm});
            skLineSegment(sketch, "E8.3.11.22", {"start": v(648, -1192) * mm, "end": v(648, -1242) * mm});
            skLineSegment(sketch, "E8.6.11.22", {"start": v(598, -1242) * mm, "end": v(648, -1242) * mm});
            skLineSegment(sketch, "E8.9.11.22", {"start": v(598, -1192) * mm, "end": v(598, -1242) * mm});
            skLineSegment(sketch, "E8.0.11.23", {"start": v(598, -1246) * mm, "end": v(648, -1246) * mm});
            skLineSegment(sketch, "E8.3.11.23", {"start": v(648, -1246) * mm, "end": v(648, -1296) * mm});
            skLineSegment(sketch, "E8.6.11.23", {"start": v(598, -1296) * mm, "end": v(648, -1296) * mm});
            skLineSegment(sketch, "E8.9.11.23", {"start": v(598, -1246) * mm, "end": v(598, -1296) * mm});
            skLineSegment(sketch, "E8.0.11.24", {"start": v(598, -1300) * mm, "end": v(648, -1300) * mm});
            skLineSegment(sketch, "E8.3.11.24", {"start": v(648, -1300) * mm, "end": v(648, -1350) * mm});
            skLineSegment(sketch, "E8.6.11.24", {"start": v(598, -1350) * mm, "end": v(648, -1350) * mm});
            skLineSegment(sketch, "E8.9.11.24", {"start": v(598, -1300) * mm, "end": v(598, -1350) * mm});
            skLineSegment(sketch, "E8.0.11.25", {"start": v(598, -1354) * mm, "end": v(648, -1354) * mm});
            skLineSegment(sketch, "E8.3.11.25", {"start": v(648, -1354) * mm, "end": v(648, -1404) * mm});
            skLineSegment(sketch, "E8.6.11.25", {"start": v(598, -1404) * mm, "end": v(648, -1404) * mm});
            skLineSegment(sketch, "E8.9.11.25", {"start": v(598, -1354) * mm, "end": v(598, -1404) * mm});
            skLineSegment(sketch, "E9.0.12.0", {"start": v(652, -4) * mm, "end": v(702, -4) * mm});
            skLineSegment(sketch, "E9.3.12.0", {"start": v(702, -4) * mm, "end": v(702, -54) * mm});
            skLineSegment(sketch, "E9.6.12.0", {"start": v(652, -54) * mm, "end": v(702, -54) * mm});
            skLineSegment(sketch, "E9.9.12.0", {"start": v(652, -4) * mm, "end": v(652, -54) * mm});
            skLineSegment(sketch, "E9.0.12.1", {"start": v(652, -58) * mm, "end": v(702, -58) * mm});
            skLineSegment(sketch, "E9.3.12.1", {"start": v(702, -58) * mm, "end": v(702, -108) * mm});
            skLineSegment(sketch, "E9.6.12.1", {"start": v(652, -108) * mm, "end": v(702, -108) * mm});
            skLineSegment(sketch, "E9.9.12.1", {"start": v(652, -58) * mm, "end": v(652, -108) * mm});
            skLineSegment(sketch, "E9.0.12.2", {"start": v(652, -112) * mm, "end": v(702, -112) * mm});
            skLineSegment(sketch, "E9.3.12.2", {"start": v(702, -112) * mm, "end": v(702, -162) * mm});
            skLineSegment(sketch, "E9.6.12.2", {"start": v(652, -162) * mm, "end": v(702, -162) * mm});
            skLineSegment(sketch, "E9.9.12.2", {"start": v(652, -112) * mm, "end": v(652, -162) * mm});
            skLineSegment(sketch, "E9.0.12.3", {"start": v(652, -166) * mm, "end": v(702, -166) * mm});
            skLineSegment(sketch, "E9.3.12.3", {"start": v(702, -166) * mm, "end": v(702, -216) * mm});
            skLineSegment(sketch, "E9.6.12.3", {"start": v(652, -216) * mm, "end": v(702, -216) * mm});
            skLineSegment(sketch, "E9.9.12.3", {"start": v(652, -166) * mm, "end": v(652, -216) * mm});
            skLineSegment(sketch, "E9.0.12.4", {"start": v(652, -220) * mm, "end": v(702, -220) * mm});
            skLineSegment(sketch, "E9.3.12.4", {"start": v(702, -220) * mm, "end": v(702, -270) * mm});
            skLineSegment(sketch, "E9.6.12.4", {"start": v(652, -270) * mm, "end": v(702, -270) * mm});
            skLineSegment(sketch, "E9.9.12.4", {"start": v(652, -220) * mm, "end": v(652, -270) * mm});
            skLineSegment(sketch, "E9.0.12.5", {"start": v(652, -274) * mm, "end": v(702, -274) * mm});
            skLineSegment(sketch, "E9.3.12.5", {"start": v(702, -274) * mm, "end": v(702, -324) * mm});
            skLineSegment(sketch, "E9.6.12.5", {"start": v(652, -324) * mm, "end": v(702, -324) * mm});
            skLineSegment(sketch, "E9.9.12.5", {"start": v(652, -274) * mm, "end": v(652, -324) * mm});
            skLineSegment(sketch, "E9.0.12.6", {"start": v(652, -328) * mm, "end": v(702, -328) * mm});
            skLineSegment(sketch, "E9.3.12.6", {"start": v(702, -328) * mm, "end": v(702, -378) * mm});
            skLineSegment(sketch, "E9.6.12.6", {"start": v(652, -378) * mm, "end": v(702, -378) * mm});
            skLineSegment(sketch, "E9.9.12.6", {"start": v(652, -328) * mm, "end": v(652, -378) * mm});
            skLineSegment(sketch, "E9.0.12.7", {"start": v(652, -382) * mm, "end": v(702, -382) * mm});
            skLineSegment(sketch, "E9.3.12.7", {"start": v(702, -382) * mm, "end": v(702, -432) * mm});
            skLineSegment(sketch, "E9.6.12.7", {"start": v(652, -432) * mm, "end": v(702, -432) * mm});
            skLineSegment(sketch, "E9.9.12.7", {"start": v(652, -382) * mm, "end": v(652, -432) * mm});
            skLineSegment(sketch, "E9.0.12.8", {"start": v(652, -436) * mm, "end": v(702, -436) * mm});
            skLineSegment(sketch, "E9.3.12.8", {"start": v(702, -436) * mm, "end": v(702, -486) * mm});
            skLineSegment(sketch, "E9.6.12.8", {"start": v(652, -486) * mm, "end": v(702, -486) * mm});
            skLineSegment(sketch, "E9.9.12.8", {"start": v(652, -436) * mm, "end": v(652, -486) * mm});
            skLineSegment(sketch, "E9.0.12.9", {"start": v(652, -490) * mm, "end": v(702, -490) * mm});
            skLineSegment(sketch, "E9.3.12.9", {"start": v(702, -490) * mm, "end": v(702, -540) * mm});
            skLineSegment(sketch, "E9.6.12.9", {"start": v(652, -540) * mm, "end": v(702, -540) * mm});
            skLineSegment(sketch, "E9.9.12.9", {"start": v(652, -490) * mm, "end": v(652, -540) * mm});
            skLineSegment(sketch, "E9.0.12.10", {"start": v(652, -544) * mm, "end": v(702, -544) * mm});
            skLineSegment(sketch, "E9.3.12.10", {"start": v(702, -544) * mm, "end": v(702, -594) * mm});
            skLineSegment(sketch, "E9.6.12.10", {"start": v(652, -594) * mm, "end": v(702, -594) * mm});
            skLineSegment(sketch, "E9.9.12.10", {"start": v(652, -544) * mm, "end": v(652, -594) * mm});
            skLineSegment(sketch, "E9.0.12.11", {"start": v(652, -598) * mm, "end": v(702, -598) * mm});
            skLineSegment(sketch, "E9.3.12.11", {"start": v(702, -598) * mm, "end": v(702, -648) * mm});
            skLineSegment(sketch, "E9.6.12.11", {"start": v(652, -648) * mm, "end": v(702, -648) * mm});
            skLineSegment(sketch, "E9.9.12.11", {"start": v(652, -598) * mm, "end": v(652, -648) * mm});
            skLineSegment(sketch, "E9.0.12.12", {"start": v(652, -652) * mm, "end": v(702, -652) * mm});
            skLineSegment(sketch, "E9.3.12.12", {"start": v(702, -652) * mm, "end": v(702, -702) * mm});
            skLineSegment(sketch, "E9.6.12.12", {"start": v(652, -702) * mm, "end": v(702, -702) * mm});
            skLineSegment(sketch, "E9.9.12.12", {"start": v(652, -652) * mm, "end": v(652, -702) * mm});
            skLineSegment(sketch, "E9.0.12.13", {"start": v(652, -706) * mm, "end": v(702, -706) * mm});
            skLineSegment(sketch, "E9.3.12.13", {"start": v(702, -706) * mm, "end": v(702, -756) * mm});
            skLineSegment(sketch, "E9.6.12.13", {"start": v(652, -756) * mm, "end": v(702, -756) * mm});
            skLineSegment(sketch, "E9.9.12.13", {"start": v(652, -706) * mm, "end": v(652, -756) * mm});
            skLineSegment(sketch, "E9.0.12.14", {"start": v(652, -760) * mm, "end": v(702, -760) * mm});
            skLineSegment(sketch, "E9.3.12.14", {"start": v(702, -760) * mm, "end": v(702, -810) * mm});
            skLineSegment(sketch, "E9.6.12.14", {"start": v(652, -810) * mm, "end": v(702, -810) * mm});
            skLineSegment(sketch, "E9.9.12.14", {"start": v(652, -760) * mm, "end": v(652, -810) * mm});
            skLineSegment(sketch, "E9.0.12.15", {"start": v(652, -814) * mm, "end": v(702, -814) * mm});
            skLineSegment(sketch, "E9.3.12.15", {"start": v(702, -814) * mm, "end": v(702, -864) * mm});
            skLineSegment(sketch, "E9.6.12.15", {"start": v(652, -864) * mm, "end": v(702, -864) * mm});
            skLineSegment(sketch, "E9.9.12.15", {"start": v(652, -814) * mm, "end": v(652, -864) * mm});
            skLineSegment(sketch, "E9.0.12.16", {"start": v(652, -868) * mm, "end": v(702, -868) * mm});
            skLineSegment(sketch, "E9.3.12.16", {"start": v(702, -868) * mm, "end": v(702, -918) * mm});
            skLineSegment(sketch, "E9.6.12.16", {"start": v(652, -918) * mm, "end": v(702, -918) * mm});
            skLineSegment(sketch, "E9.9.12.16", {"start": v(652, -868) * mm, "end": v(652, -918) * mm});
            skLineSegment(sketch, "E9.0.12.17", {"start": v(652, -922) * mm, "end": v(702, -922) * mm});
            skLineSegment(sketch, "E9.3.12.17", {"start": v(702, -922) * mm, "end": v(702, -972) * mm});
            skLineSegment(sketch, "E9.6.12.17", {"start": v(652, -972) * mm, "end": v(702, -972) * mm});
            skLineSegment(sketch, "E9.9.12.17", {"start": v(652, -922) * mm, "end": v(652, -972) * mm});
            skLineSegment(sketch, "E9.0.12.18", {"start": v(652, -976) * mm, "end": v(702, -976) * mm});
            skLineSegment(sketch, "E9.3.12.18", {"start": v(702, -976) * mm, "end": v(702, -1026) * mm});
            skLineSegment(sketch, "E9.6.12.18", {"start": v(652, -1026) * mm, "end": v(702, -1026) * mm});
            skLineSegment(sketch, "E9.9.12.18", {"start": v(652, -976) * mm, "end": v(652, -1026) * mm});
            skLineSegment(sketch, "E9.0.12.19", {"start": v(652, -1030) * mm, "end": v(702, -1030) * mm});
            skLineSegment(sketch, "E9.3.12.19", {"start": v(702, -1030) * mm, "end": v(702, -1080) * mm});
            skLineSegment(sketch, "E9.6.12.19", {"start": v(652, -1080) * mm, "end": v(702, -1080) * mm});
            skLineSegment(sketch, "E9.9.12.19", {"start": v(652, -1030) * mm, "end": v(652, -1080) * mm});
            skLineSegment(sketch, "E9.0.12.20", {"start": v(652, -1084) * mm, "end": v(702, -1084) * mm});
            skLineSegment(sketch, "E9.3.12.20", {"start": v(702, -1084) * mm, "end": v(702, -1134) * mm});
            skLineSegment(sketch, "E9.6.12.20", {"start": v(652, -1134) * mm, "end": v(702, -1134) * mm});
            skLineSegment(sketch, "E9.9.12.20", {"start": v(652, -1084) * mm, "end": v(652, -1134) * mm});
            skLineSegment(sketch, "E9.0.12.21", {"start": v(652, -1138) * mm, "end": v(702, -1138) * mm});
            skLineSegment(sketch, "E9.3.12.21", {"start": v(702, -1138) * mm, "end": v(702, -1188) * mm});
            skLineSegment(sketch, "E9.6.12.21", {"start": v(652, -1188) * mm, "end": v(702, -1188) * mm});
            skLineSegment(sketch, "E9.9.12.21", {"start": v(652, -1138) * mm, "end": v(652, -1188) * mm});
            skLineSegment(sketch, "E9.0.12.22", {"start": v(652, -1192) * mm, "end": v(702, -1192) * mm});
            skLineSegment(sketch, "E9.3.12.22", {"start": v(702, -1192) * mm, "end": v(702, -1242) * mm});
            skLineSegment(sketch, "E9.6.12.22", {"start": v(652, -1242) * mm, "end": v(702, -1242) * mm});
            skLineSegment(sketch, "E9.9.12.22", {"start": v(652, -1192) * mm, "end": v(652, -1242) * mm});
            skLineSegment(sketch, "E9.0.12.23", {"start": v(652, -1246) * mm, "end": v(702, -1246) * mm});
            skLineSegment(sketch, "E9.3.12.23", {"start": v(702, -1246) * mm, "end": v(702, -1296) * mm});
            skLineSegment(sketch, "E9.6.12.23", {"start": v(652, -1296) * mm, "end": v(702, -1296) * mm});
            skLineSegment(sketch, "E9.9.12.23", {"start": v(652, -1246) * mm, "end": v(652, -1296) * mm});
            skLineSegment(sketch, "E9.0.12.24", {"start": v(652, -1300) * mm, "end": v(702, -1300) * mm});
            skLineSegment(sketch, "E9.3.12.24", {"start": v(702, -1300) * mm, "end": v(702, -1350) * mm});
            skLineSegment(sketch, "E9.6.12.24", {"start": v(652, -1350) * mm, "end": v(702, -1350) * mm});
            skLineSegment(sketch, "E9.9.12.24", {"start": v(652, -1300) * mm, "end": v(652, -1350) * mm});
            skLineSegment(sketch, "E9.0.12.25", {"start": v(652, -1354) * mm, "end": v(702, -1354) * mm});
            skLineSegment(sketch, "E9.3.12.25", {"start": v(702, -1354) * mm, "end": v(702, -1404) * mm});
            skLineSegment(sketch, "E9.6.12.25", {"start": v(652, -1404) * mm, "end": v(702, -1404) * mm});
            skLineSegment(sketch, "E9.9.12.25", {"start": v(652, -1354) * mm, "end": v(652, -1404) * mm});
            skLineSegment(sketch, "E9.0.13.0", {"start": v(706, -4) * mm, "end": v(756, -4) * mm});
            skLineSegment(sketch, "E9.3.13.0", {"start": v(756, -4) * mm, "end": v(756, -54) * mm});
            skLineSegment(sketch, "E9.6.13.0", {"start": v(706, -54) * mm, "end": v(756, -54) * mm});
            skLineSegment(sketch, "E9.9.13.0", {"start": v(706, -4) * mm, "end": v(706, -54) * mm});
            skLineSegment(sketch, "E9.0.13.1", {"start": v(706, -58) * mm, "end": v(756, -58) * mm});
            skLineSegment(sketch, "E9.3.13.1", {"start": v(756, -58) * mm, "end": v(756, -108) * mm});
            skLineSegment(sketch, "E9.6.13.1", {"start": v(706, -108) * mm, "end": v(756, -108) * mm});
            skLineSegment(sketch, "E9.9.13.1", {"start": v(706, -58) * mm, "end": v(706, -108) * mm});
            skLineSegment(sketch, "E9.0.13.2", {"start": v(706, -112) * mm, "end": v(756, -112) * mm});
            skLineSegment(sketch, "E9.3.13.2", {"start": v(756, -112) * mm, "end": v(756, -162) * mm});
            skLineSegment(sketch, "E9.6.13.2", {"start": v(706, -162) * mm, "end": v(756, -162) * mm});
            skLineSegment(sketch, "E9.9.13.2", {"start": v(706, -112) * mm, "end": v(706, -162) * mm});
            skLineSegment(sketch, "E9.0.13.3", {"start": v(706, -166) * mm, "end": v(756, -166) * mm});
            skLineSegment(sketch, "E9.3.13.3", {"start": v(756, -166) * mm, "end": v(756, -216) * mm});
            skLineSegment(sketch, "E9.6.13.3", {"start": v(706, -216) * mm, "end": v(756, -216) * mm});
            skLineSegment(sketch, "E9.9.13.3", {"start": v(706, -166) * mm, "end": v(706, -216) * mm});
            skLineSegment(sketch, "E9.0.13.4", {"start": v(706, -220) * mm, "end": v(756, -220) * mm});
            skLineSegment(sketch, "E9.3.13.4", {"start": v(756, -220) * mm, "end": v(756, -270) * mm});
            skLineSegment(sketch, "E9.6.13.4", {"start": v(706, -270) * mm, "end": v(756, -270) * mm});
            skLineSegment(sketch, "E9.9.13.4", {"start": v(706, -220) * mm, "end": v(706, -270) * mm});
            skLineSegment(sketch, "E9.0.13.5", {"start": v(706, -274) * mm, "end": v(756, -274) * mm});
            skLineSegment(sketch, "E9.3.13.5", {"start": v(756, -274) * mm, "end": v(756, -324) * mm});
            skLineSegment(sketch, "E9.6.13.5", {"start": v(706, -324) * mm, "end": v(756, -324) * mm});
            skLineSegment(sketch, "E9.9.13.5", {"start": v(706, -274) * mm, "end": v(706, -324) * mm});
            skLineSegment(sketch, "E9.0.13.6", {"start": v(706, -328) * mm, "end": v(756, -328) * mm});
            skLineSegment(sketch, "E9.3.13.6", {"start": v(756, -328) * mm, "end": v(756, -378) * mm});
            skLineSegment(sketch, "E9.6.13.6", {"start": v(706, -378) * mm, "end": v(756, -378) * mm});
            skLineSegment(sketch, "E9.9.13.6", {"start": v(706, -328) * mm, "end": v(706, -378) * mm});
            skLineSegment(sketch, "E9.0.13.7", {"start": v(706, -382) * mm, "end": v(756, -382) * mm});
            skLineSegment(sketch, "E9.3.13.7", {"start": v(756, -382) * mm, "end": v(756, -432) * mm});
            skLineSegment(sketch, "E9.6.13.7", {"start": v(706, -432) * mm, "end": v(756, -432) * mm});
            skLineSegment(sketch, "E9.9.13.7", {"start": v(706, -382) * mm, "end": v(706, -432) * mm});
            skLineSegment(sketch, "E9.0.13.8", {"start": v(706, -436) * mm, "end": v(756, -436) * mm});
            skLineSegment(sketch, "E9.3.13.8", {"start": v(756, -436) * mm, "end": v(756, -486) * mm});
            skLineSegment(sketch, "E9.6.13.8", {"start": v(706, -486) * mm, "end": v(756, -486) * mm});
            skLineSegment(sketch, "E9.9.13.8", {"start": v(706, -436) * mm, "end": v(706, -486) * mm});
            skLineSegment(sketch, "E9.0.13.9", {"start": v(706, -490) * mm, "end": v(756, -490) * mm});
            skLineSegment(sketch, "E9.3.13.9", {"start": v(756, -490) * mm, "end": v(756, -540) * mm});
            skLineSegment(sketch, "E9.6.13.9", {"start": v(706, -540) * mm, "end": v(756, -540) * mm});
            skLineSegment(sketch, "E9.9.13.9", {"start": v(706, -490) * mm, "end": v(706, -540) * mm});
            skLineSegment(sketch, "E9.0.13.10", {"start": v(706, -544) * mm, "end": v(756, -544) * mm});
            skLineSegment(sketch, "E9.3.13.10", {"start": v(756, -544) * mm, "end": v(756, -594) * mm});
            skLineSegment(sketch, "E9.6.13.10", {"start": v(706, -594) * mm, "end": v(756, -594) * mm});
            skLineSegment(sketch, "E9.9.13.10", {"start": v(706, -544) * mm, "end": v(706, -594) * mm});
            skLineSegment(sketch, "E9.0.13.11", {"start": v(706, -598) * mm, "end": v(756, -598) * mm});
            skLineSegment(sketch, "E9.3.13.11", {"start": v(756, -598) * mm, "end": v(756, -648) * mm});
            skLineSegment(sketch, "E9.6.13.11", {"start": v(706, -648) * mm, "end": v(756, -648) * mm});
            skLineSegment(sketch, "E9.9.13.11", {"start": v(706, -598) * mm, "end": v(706, -648) * mm});
            skLineSegment(sketch, "E9.0.13.12", {"start": v(706, -652) * mm, "end": v(756, -652) * mm});
            skLineSegment(sketch, "E9.3.13.12", {"start": v(756, -652) * mm, "end": v(756, -702) * mm});
            skLineSegment(sketch, "E9.6.13.12", {"start": v(706, -702) * mm, "end": v(756, -702) * mm});
            skLineSegment(sketch, "E9.9.13.12", {"start": v(706, -652) * mm, "end": v(706, -702) * mm});
            skLineSegment(sketch, "E9.0.13.13", {"start": v(706, -706) * mm, "end": v(756, -706) * mm});
            skLineSegment(sketch, "E9.3.13.13", {"start": v(756, -706) * mm, "end": v(756, -756) * mm});
            skLineSegment(sketch, "E9.6.13.13", {"start": v(706, -756) * mm, "end": v(756, -756) * mm});
            skLineSegment(sketch, "E9.9.13.13", {"start": v(706, -706) * mm, "end": v(706, -756) * mm});
            skLineSegment(sketch, "E9.0.13.14", {"start": v(706, -760) * mm, "end": v(756, -760) * mm});
            skLineSegment(sketch, "E9.3.13.14", {"start": v(756, -760) * mm, "end": v(756, -810) * mm});
            skLineSegment(sketch, "E9.6.13.14", {"start": v(706, -810) * mm, "end": v(756, -810) * mm});
            skLineSegment(sketch, "E9.9.13.14", {"start": v(706, -760) * mm, "end": v(706, -810) * mm});
            skLineSegment(sketch, "E9.0.13.15", {"start": v(706, -814) * mm, "end": v(756, -814) * mm});
            skLineSegment(sketch, "E9.3.13.15", {"start": v(756, -814) * mm, "end": v(756, -864) * mm});
            skLineSegment(sketch, "E9.6.13.15", {"start": v(706, -864) * mm, "end": v(756, -864) * mm});
            skLineSegment(sketch, "E9.9.13.15", {"start": v(706, -814) * mm, "end": v(706, -864) * mm});
            skLineSegment(sketch, "E9.0.13.16", {"start": v(706, -868) * mm, "end": v(756, -868) * mm});
            skLineSegment(sketch, "E9.3.13.16", {"start": v(756, -868) * mm, "end": v(756, -918) * mm});
            skLineSegment(sketch, "E9.6.13.16", {"start": v(706, -918) * mm, "end": v(756, -918) * mm});
            skLineSegment(sketch, "E9.9.13.16", {"start": v(706, -868) * mm, "end": v(706, -918) * mm});
            skLineSegment(sketch, "E9.0.13.17", {"start": v(706, -922) * mm, "end": v(756, -922) * mm});
            skLineSegment(sketch, "E9.3.13.17", {"start": v(756, -922) * mm, "end": v(756, -972) * mm});
            skLineSegment(sketch, "E9.6.13.17", {"start": v(706, -972) * mm, "end": v(756, -972) * mm});
            skLineSegment(sketch, "E9.9.13.17", {"start": v(706, -922) * mm, "end": v(706, -972) * mm});
            skLineSegment(sketch, "E9.0.13.18", {"start": v(706, -976) * mm, "end": v(756, -976) * mm});
            skLineSegment(sketch, "E9.3.13.18", {"start": v(756, -976) * mm, "end": v(756, -1026) * mm});
            skLineSegment(sketch, "E9.6.13.18", {"start": v(706, -1026) * mm, "end": v(756, -1026) * mm});
            skLineSegment(sketch, "E9.9.13.18", {"start": v(706, -976) * mm, "end": v(706, -1026) * mm});
            skLineSegment(sketch, "E9.0.13.19", {"start": v(706, -1030) * mm, "end": v(756, -1030) * mm});
            skLineSegment(sketch, "E9.3.13.19", {"start": v(756, -1030) * mm, "end": v(756, -1080) * mm});
            skLineSegment(sketch, "E9.6.13.19", {"start": v(706, -1080) * mm, "end": v(756, -1080) * mm});
            skLineSegment(sketch, "E9.9.13.19", {"start": v(706, -1030) * mm, "end": v(706, -1080) * mm});
            skLineSegment(sketch, "E9.0.13.20", {"start": v(706, -1084) * mm, "end": v(756, -1084) * mm});
            skLineSegment(sketch, "E9.3.13.20", {"start": v(756, -1084) * mm, "end": v(756, -1134) * mm});
            skLineSegment(sketch, "E9.6.13.20", {"start": v(706, -1134) * mm, "end": v(756, -1134) * mm});
            skLineSegment(sketch, "E9.9.13.20", {"start": v(706, -1084) * mm, "end": v(706, -1134) * mm});
            skLineSegment(sketch, "E9.0.13.21", {"start": v(706, -1138) * mm, "end": v(756, -1138) * mm});
            skLineSegment(sketch, "E9.3.13.21", {"start": v(756, -1138) * mm, "end": v(756, -1188) * mm});
            skLineSegment(sketch, "E9.6.13.21", {"start": v(706, -1188) * mm, "end": v(756, -1188) * mm});
            skLineSegment(sketch, "E9.9.13.21", {"start": v(706, -1138) * mm, "end": v(706, -1188) * mm});
            skLineSegment(sketch, "E9.0.13.22", {"start": v(706, -1192) * mm, "end": v(756, -1192) * mm});
            skLineSegment(sketch, "E9.3.13.22", {"start": v(756, -1192) * mm, "end": v(756, -1242) * mm});
            skLineSegment(sketch, "E9.6.13.22", {"start": v(706, -1242) * mm, "end": v(756, -1242) * mm});
            skLineSegment(sketch, "E9.9.13.22", {"start": v(706, -1192) * mm, "end": v(706, -1242) * mm});
            skLineSegment(sketch, "E9.0.13.23", {"start": v(706, -1246) * mm, "end": v(756, -1246) * mm});
            skLineSegment(sketch, "E9.3.13.23", {"start": v(756, -1246) * mm, "end": v(756, -1296) * mm});
            skLineSegment(sketch, "E9.6.13.23", {"start": v(706, -1296) * mm, "end": v(756, -1296) * mm});
            skLineSegment(sketch, "E9.9.13.23", {"start": v(706, -1246) * mm, "end": v(706, -1296) * mm});
            skLineSegment(sketch, "E9.0.13.24", {"start": v(706, -1300) * mm, "end": v(756, -1300) * mm});
            skLineSegment(sketch, "E9.3.13.24", {"start": v(756, -1300) * mm, "end": v(756, -1350) * mm});
            skLineSegment(sketch, "E9.6.13.24", {"start": v(706, -1350) * mm, "end": v(756, -1350) * mm});
            skLineSegment(sketch, "E9.9.13.24", {"start": v(706, -1300) * mm, "end": v(706, -1350) * mm});
            skLineSegment(sketch, "E9.0.13.25", {"start": v(706, -1354) * mm, "end": v(756, -1354) * mm});
            skLineSegment(sketch, "E9.3.13.25", {"start": v(756, -1354) * mm, "end": v(756, -1404) * mm});
            skLineSegment(sketch, "E9.6.13.25", {"start": v(706, -1404) * mm, "end": v(756, -1404) * mm});
            skLineSegment(sketch, "E9.9.13.25", {"start": v(706, -1354) * mm, "end": v(706, -1404) * mm});
            skLineSegment(sketch, "E9.0.14.0", {"start": v(760, -4) * mm, "end": v(810, -4) * mm});
            skLineSegment(sketch, "E9.3.14.0", {"start": v(810, -4) * mm, "end": v(810, -54) * mm});
            skLineSegment(sketch, "E9.6.14.0", {"start": v(760, -54) * mm, "end": v(810, -54) * mm});
            skLineSegment(sketch, "E9.9.14.0", {"start": v(760, -4) * mm, "end": v(760, -54) * mm});
            skLineSegment(sketch, "E9.0.14.1", {"start": v(760, -58) * mm, "end": v(810, -58) * mm});
            skLineSegment(sketch, "E9.3.14.1", {"start": v(810, -58) * mm, "end": v(810, -108) * mm});
            skLineSegment(sketch, "E9.6.14.1", {"start": v(760, -108) * mm, "end": v(810, -108) * mm});
            skLineSegment(sketch, "E9.9.14.1", {"start": v(760, -58) * mm, "end": v(760, -108) * mm});
            skLineSegment(sketch, "E9.0.14.2", {"start": v(760, -112) * mm, "end": v(810, -112) * mm});
            skLineSegment(sketch, "E9.3.14.2", {"start": v(810, -112) * mm, "end": v(810, -162) * mm});
            skLineSegment(sketch, "E9.6.14.2", {"start": v(760, -162) * mm, "end": v(810, -162) * mm});
            skLineSegment(sketch, "E9.9.14.2", {"start": v(760, -112) * mm, "end": v(760, -162) * mm});
            skLineSegment(sketch, "E9.0.14.3", {"start": v(760, -166) * mm, "end": v(810, -166) * mm});
            skLineSegment(sketch, "E9.3.14.3", {"start": v(810, -166) * mm, "end": v(810, -216) * mm});
            skLineSegment(sketch, "E9.6.14.3", {"start": v(760, -216) * mm, "end": v(810, -216) * mm});
            skLineSegment(sketch, "E9.9.14.3", {"start": v(760, -166) * mm, "end": v(760, -216) * mm});
            skLineSegment(sketch, "E9.0.14.4", {"start": v(760, -220) * mm, "end": v(810, -220) * mm});
            skLineSegment(sketch, "E9.3.14.4", {"start": v(810, -220) * mm, "end": v(810, -270) * mm});
            skLineSegment(sketch, "E9.6.14.4", {"start": v(760, -270) * mm, "end": v(810, -270) * mm});
            skLineSegment(sketch, "E9.9.14.4", {"start": v(760, -220) * mm, "end": v(760, -270) * mm});
            skLineSegment(sketch, "E9.0.14.5", {"start": v(760, -274) * mm, "end": v(810, -274) * mm});
            skLineSegment(sketch, "E9.3.14.5", {"start": v(810, -274) * mm, "end": v(810, -324) * mm});
            skLineSegment(sketch, "E9.6.14.5", {"start": v(760, -324) * mm, "end": v(810, -324) * mm});
            skLineSegment(sketch, "E9.9.14.5", {"start": v(760, -274) * mm, "end": v(760, -324) * mm});
            skLineSegment(sketch, "E9.0.14.6", {"start": v(760, -328) * mm, "end": v(810, -328) * mm});
            skLineSegment(sketch, "E9.3.14.6", {"start": v(810, -328) * mm, "end": v(810, -378) * mm});
            skLineSegment(sketch, "E9.6.14.6", {"start": v(760, -378) * mm, "end": v(810, -378) * mm});
            skLineSegment(sketch, "E9.9.14.6", {"start": v(760, -328) * mm, "end": v(760, -378) * mm});
            skLineSegment(sketch, "E9.0.14.7", {"start": v(760, -382) * mm, "end": v(810, -382) * mm});
            skLineSegment(sketch, "E9.3.14.7", {"start": v(810, -382) * mm, "end": v(810, -432) * mm});
            skLineSegment(sketch, "E9.6.14.7", {"start": v(760, -432) * mm, "end": v(810, -432) * mm});
            skLineSegment(sketch, "E9.9.14.7", {"start": v(760, -382) * mm, "end": v(760, -432) * mm});
            skLineSegment(sketch, "E9.0.14.8", {"start": v(760, -436) * mm, "end": v(810, -436) * mm});
            skLineSegment(sketch, "E9.3.14.8", {"start": v(810, -436) * mm, "end": v(810, -486) * mm});
            skLineSegment(sketch, "E9.6.14.8", {"start": v(760, -486) * mm, "end": v(810, -486) * mm});
            skLineSegment(sketch, "E9.9.14.8", {"start": v(760, -436) * mm, "end": v(760, -486) * mm});
            skLineSegment(sketch, "E9.0.14.9", {"start": v(760, -490) * mm, "end": v(810, -490) * mm});
            skLineSegment(sketch, "E9.3.14.9", {"start": v(810, -490) * mm, "end": v(810, -540) * mm});
            skLineSegment(sketch, "E9.6.14.9", {"start": v(760, -540) * mm, "end": v(810, -540) * mm});
            skLineSegment(sketch, "E9.9.14.9", {"start": v(760, -490) * mm, "end": v(760, -540) * mm});
            skLineSegment(sketch, "E9.0.14.10", {"start": v(760, -544) * mm, "end": v(810, -544) * mm});
            skLineSegment(sketch, "E9.3.14.10", {"start": v(810, -544) * mm, "end": v(810, -594) * mm});
            skLineSegment(sketch, "E9.6.14.10", {"start": v(760, -594) * mm, "end": v(810, -594) * mm});
            skLineSegment(sketch, "E9.9.14.10", {"start": v(760, -544) * mm, "end": v(760, -594) * mm});
            skLineSegment(sketch, "E9.0.14.11", {"start": v(760, -598) * mm, "end": v(810, -598) * mm});
            skLineSegment(sketch, "E9.3.14.11", {"start": v(810, -598) * mm, "end": v(810, -648) * mm});
            skLineSegment(sketch, "E9.6.14.11", {"start": v(760, -648) * mm, "end": v(810, -648) * mm});
            skLineSegment(sketch, "E9.9.14.11", {"start": v(760, -598) * mm, "end": v(760, -648) * mm});
            skLineSegment(sketch, "E9.0.14.12", {"start": v(760, -652) * mm, "end": v(810, -652) * mm});
            skLineSegment(sketch, "E9.3.14.12", {"start": v(810, -652) * mm, "end": v(810, -702) * mm});
            skLineSegment(sketch, "E9.6.14.12", {"start": v(760, -702) * mm, "end": v(810, -702) * mm});
            skLineSegment(sketch, "E9.9.14.12", {"start": v(760, -652) * mm, "end": v(760, -702) * mm});
            skLineSegment(sketch, "E9.0.14.13", {"start": v(760, -706) * mm, "end": v(810, -706) * mm});
            skLineSegment(sketch, "E9.3.14.13", {"start": v(810, -706) * mm, "end": v(810, -756) * mm});
            skLineSegment(sketch, "E9.6.14.13", {"start": v(760, -756) * mm, "end": v(810, -756) * mm});
            skLineSegment(sketch, "E9.9.14.13", {"start": v(760, -706) * mm, "end": v(760, -756) * mm});
            skLineSegment(sketch, "E9.0.14.14", {"start": v(760, -760) * mm, "end": v(810, -760) * mm});
            skLineSegment(sketch, "E9.3.14.14", {"start": v(810, -760) * mm, "end": v(810, -810) * mm});
            skLineSegment(sketch, "E9.6.14.14", {"start": v(760, -810) * mm, "end": v(810, -810) * mm});
            skLineSegment(sketch, "E9.9.14.14", {"start": v(760, -760) * mm, "end": v(760, -810) * mm});
            skLineSegment(sketch, "E9.0.14.15", {"start": v(760, -814) * mm, "end": v(810, -814) * mm});
            skLineSegment(sketch, "E9.3.14.15", {"start": v(810, -814) * mm, "end": v(810, -864) * mm});
            skLineSegment(sketch, "E9.6.14.15", {"start": v(760, -864) * mm, "end": v(810, -864) * mm});
            skLineSegment(sketch, "E9.9.14.15", {"start": v(760, -814) * mm, "end": v(760, -864) * mm});
            skLineSegment(sketch, "E9.0.14.16", {"start": v(760, -868) * mm, "end": v(810, -868) * mm});
            skLineSegment(sketch, "E9.3.14.16", {"start": v(810, -868) * mm, "end": v(810, -918) * mm});
            skLineSegment(sketch, "E9.6.14.16", {"start": v(760, -918) * mm, "end": v(810, -918) * mm});
            skLineSegment(sketch, "E9.9.14.16", {"start": v(760, -868) * mm, "end": v(760, -918) * mm});
            skLineSegment(sketch, "E9.0.14.17", {"start": v(760, -922) * mm, "end": v(810, -922) * mm});
            skLineSegment(sketch, "E9.3.14.17", {"start": v(810, -922) * mm, "end": v(810, -972) * mm});
            skLineSegment(sketch, "E9.6.14.17", {"start": v(760, -972) * mm, "end": v(810, -972) * mm});
            skLineSegment(sketch, "E9.9.14.17", {"start": v(760, -922) * mm, "end": v(760, -972) * mm});
            skLineSegment(sketch, "E9.0.14.18", {"start": v(760, -976) * mm, "end": v(810, -976) * mm});
            skLineSegment(sketch, "E9.3.14.18", {"start": v(810, -976) * mm, "end": v(810, -1026) * mm});
            skLineSegment(sketch, "E9.6.14.18", {"start": v(760, -1026) * mm, "end": v(810, -1026) * mm});
            skLineSegment(sketch, "E9.9.14.18", {"start": v(760, -976) * mm, "end": v(760, -1026) * mm});
            skLineSegment(sketch, "E9.0.14.19", {"start": v(760, -1030) * mm, "end": v(810, -1030) * mm});
            skLineSegment(sketch, "E9.3.14.19", {"start": v(810, -1030) * mm, "end": v(810, -1080) * mm});
            skLineSegment(sketch, "E9.6.14.19", {"start": v(760, -1080) * mm, "end": v(810, -1080) * mm});
            skLineSegment(sketch, "E9.9.14.19", {"start": v(760, -1030) * mm, "end": v(760, -1080) * mm});
            skLineSegment(sketch, "E9.0.14.20", {"start": v(760, -1084) * mm, "end": v(810, -1084) * mm});
            skLineSegment(sketch, "E9.3.14.20", {"start": v(810, -1084) * mm, "end": v(810, -1134) * mm});
            skLineSegment(sketch, "E9.6.14.20", {"start": v(760, -1134) * mm, "end": v(810, -1134) * mm});
            skLineSegment(sketch, "E9.9.14.20", {"start": v(760, -1084) * mm, "end": v(760, -1134) * mm});
            skLineSegment(sketch, "E9.0.14.21", {"start": v(760, -1138) * mm, "end": v(810, -1138) * mm});
            skLineSegment(sketch, "E9.3.14.21", {"start": v(810, -1138) * mm, "end": v(810, -1188) * mm});
            skLineSegment(sketch, "E9.6.14.21", {"start": v(760, -1188) * mm, "end": v(810, -1188) * mm});
            skLineSegment(sketch, "E9.9.14.21", {"start": v(760, -1138) * mm, "end": v(760, -1188) * mm});
            skLineSegment(sketch, "E9.0.14.22", {"start": v(760, -1192) * mm, "end": v(810, -1192) * mm});
            skLineSegment(sketch, "E9.3.14.22", {"start": v(810, -1192) * mm, "end": v(810, -1242) * mm});
            skLineSegment(sketch, "E9.6.14.22", {"start": v(760, -1242) * mm, "end": v(810, -1242) * mm});
            skLineSegment(sketch, "E9.9.14.22", {"start": v(760, -1192) * mm, "end": v(760, -1242) * mm});
            skLineSegment(sketch, "E9.0.14.23", {"start": v(760, -1246) * mm, "end": v(810, -1246) * mm});
            skLineSegment(sketch, "E9.3.14.23", {"start": v(810, -1246) * mm, "end": v(810, -1296) * mm});
            skLineSegment(sketch, "E9.6.14.23", {"start": v(760, -1296) * mm, "end": v(810, -1296) * mm});
            skLineSegment(sketch, "E9.9.14.23", {"start": v(760, -1246) * mm, "end": v(760, -1296) * mm});
            skLineSegment(sketch, "E9.0.14.24", {"start": v(760, -1300) * mm, "end": v(810, -1300) * mm});
            skLineSegment(sketch, "E9.3.14.24", {"start": v(810, -1300) * mm, "end": v(810, -1350) * mm});
            skLineSegment(sketch, "E9.6.14.24", {"start": v(760, -1350) * mm, "end": v(810, -1350) * mm});
            skLineSegment(sketch, "E9.9.14.24", {"start": v(760, -1300) * mm, "end": v(760, -1350) * mm});
            skLineSegment(sketch, "E9.0.14.25", {"start": v(760, -1354) * mm, "end": v(810, -1354) * mm});
            skLineSegment(sketch, "E9.3.14.25", {"start": v(810, -1354) * mm, "end": v(810, -1404) * mm});
            skLineSegment(sketch, "E9.6.14.25", {"start": v(760, -1404) * mm, "end": v(810, -1404) * mm});
            skLineSegment(sketch, "E9.9.14.25", {"start": v(760, -1354) * mm, "end": v(760, -1404) * mm});
            skLineSegment(sketch, "E10.0.0.26", {"start": v(4, -1408) * mm, "end": v(54, -1408) * mm});
            skLineSegment(sketch, "E10.3.0.26", {"start": v(54, -1408) * mm, "end": v(54, -1458) * mm});
            skLineSegment(sketch, "E10.6.0.26", {"start": v(4, -1458) * mm, "end": v(54, -1458) * mm});
            skLineSegment(sketch, "E10.9.0.26", {"start": v(4, -1408) * mm, "end": v(4, -1458) * mm});
            skLineSegment(sketch, "E10.0.1.26", {"start": v(58, -1408) * mm, "end": v(108, -1408) * mm});
            skLineSegment(sketch, "E10.3.1.26", {"start": v(108, -1408) * mm, "end": v(108, -1458) * mm});
            skLineSegment(sketch, "E10.6.1.26", {"start": v(58, -1458) * mm, "end": v(108, -1458) * mm});
            skLineSegment(sketch, "E10.9.1.26", {"start": v(58, -1408) * mm, "end": v(58, -1458) * mm});
            skLineSegment(sketch, "E10.0.2.26", {"start": v(112, -1408) * mm, "end": v(162, -1408) * mm});
            skLineSegment(sketch, "E10.3.2.26", {"start": v(162, -1408) * mm, "end": v(162, -1458) * mm});
            skLineSegment(sketch, "E10.6.2.26", {"start": v(112, -1458) * mm, "end": v(162, -1458) * mm});
            skLineSegment(sketch, "E10.9.2.26", {"start": v(112, -1408) * mm, "end": v(112, -1458) * mm});
            skLineSegment(sketch, "E10.0.3.26", {"start": v(166, -1408) * mm, "end": v(216, -1408) * mm});
            skLineSegment(sketch, "E10.3.3.26", {"start": v(216, -1408) * mm, "end": v(216, -1458) * mm});
            skLineSegment(sketch, "E10.6.3.26", {"start": v(166, -1458) * mm, "end": v(216, -1458) * mm});
            skLineSegment(sketch, "E10.9.3.26", {"start": v(166, -1408) * mm, "end": v(166, -1458) * mm});
            skLineSegment(sketch, "E10.0.4.26", {"start": v(220, -1408) * mm, "end": v(270, -1408) * mm});
            skLineSegment(sketch, "E10.3.4.26", {"start": v(270, -1408) * mm, "end": v(270, -1458) * mm});
            skLineSegment(sketch, "E10.6.4.26", {"start": v(220, -1458) * mm, "end": v(270, -1458) * mm});
            skLineSegment(sketch, "E10.9.4.26", {"start": v(220, -1408) * mm, "end": v(220, -1458) * mm});
            skLineSegment(sketch, "E10.0.5.26", {"start": v(274, -1408) * mm, "end": v(324, -1408) * mm});
            skLineSegment(sketch, "E10.3.5.26", {"start": v(324, -1408) * mm, "end": v(324, -1458) * mm});
            skLineSegment(sketch, "E10.6.5.26", {"start": v(274, -1458) * mm, "end": v(324, -1458) * mm});
            skLineSegment(sketch, "E10.9.5.26", {"start": v(274, -1408) * mm, "end": v(274, -1458) * mm});
            skLineSegment(sketch, "E10.0.6.26", {"start": v(328, -1408) * mm, "end": v(378, -1408) * mm});
            skLineSegment(sketch, "E10.3.6.26", {"start": v(378, -1408) * mm, "end": v(378, -1458) * mm});
            skLineSegment(sketch, "E10.6.6.26", {"start": v(328, -1458) * mm, "end": v(378, -1458) * mm});
            skLineSegment(sketch, "E10.9.6.26", {"start": v(328, -1408) * mm, "end": v(328, -1458) * mm});
            skLineSegment(sketch, "E10.0.7.26", {"start": v(382, -1408) * mm, "end": v(432, -1408) * mm});
            skLineSegment(sketch, "E10.3.7.26", {"start": v(432, -1408) * mm, "end": v(432, -1458) * mm});
            skLineSegment(sketch, "E10.6.7.26", {"start": v(382, -1458) * mm, "end": v(432, -1458) * mm});
            skLineSegment(sketch, "E10.9.7.26", {"start": v(382, -1408) * mm, "end": v(382, -1458) * mm});
            skLineSegment(sketch, "E10.0.8.26", {"start": v(436, -1408) * mm, "end": v(486, -1408) * mm});
            skLineSegment(sketch, "E10.3.8.26", {"start": v(486, -1408) * mm, "end": v(486, -1458) * mm});
            skLineSegment(sketch, "E10.6.8.26", {"start": v(436, -1458) * mm, "end": v(486, -1458) * mm});
            skLineSegment(sketch, "E10.9.8.26", {"start": v(436, -1408) * mm, "end": v(436, -1458) * mm});
            skLineSegment(sketch, "E10.0.9.26", {"start": v(490, -1408) * mm, "end": v(540, -1408) * mm});
            skLineSegment(sketch, "E10.3.9.26", {"start": v(540, -1408) * mm, "end": v(540, -1458) * mm});
            skLineSegment(sketch, "E10.6.9.26", {"start": v(490, -1458) * mm, "end": v(540, -1458) * mm});
            skLineSegment(sketch, "E10.9.9.26", {"start": v(490, -1408) * mm, "end": v(490, -1458) * mm});
            skLineSegment(sketch, "E10.0.10.26", {"start": v(544, -1408) * mm, "end": v(594, -1408) * mm});
            skLineSegment(sketch, "E10.3.10.26", {"start": v(594, -1408) * mm, "end": v(594, -1458) * mm});
            skLineSegment(sketch, "E10.6.10.26", {"start": v(544, -1458) * mm, "end": v(594, -1458) * mm});
            skLineSegment(sketch, "E10.9.10.26", {"start": v(544, -1408) * mm, "end": v(544, -1458) * mm});
            skLineSegment(sketch, "E10.0.11.26", {"start": v(598, -1408) * mm, "end": v(648, -1408) * mm});
            skLineSegment(sketch, "E10.3.11.26", {"start": v(648, -1408) * mm, "end": v(648, -1458) * mm});
            skLineSegment(sketch, "E10.6.11.26", {"start": v(598, -1458) * mm, "end": v(648, -1458) * mm});
            skLineSegment(sketch, "E10.9.11.26", {"start": v(598, -1408) * mm, "end": v(598, -1458) * mm});
            skLineSegment(sketch, "E10.0.12.26", {"start": v(652, -1408) * mm, "end": v(702, -1408) * mm});
            skLineSegment(sketch, "E10.3.12.26", {"start": v(702, -1408) * mm, "end": v(702, -1458) * mm});
            skLineSegment(sketch, "E10.6.12.26", {"start": v(652, -1458) * mm, "end": v(702, -1458) * mm});
            skLineSegment(sketch, "E10.9.12.26", {"start": v(652, -1408) * mm, "end": v(652, -1458) * mm});
            skLineSegment(sketch, "E10.0.13.26", {"start": v(706, -1408) * mm, "end": v(756, -1408) * mm});
            skLineSegment(sketch, "E10.3.13.26", {"start": v(756, -1408) * mm, "end": v(756, -1458) * mm});
            skLineSegment(sketch, "E10.6.13.26", {"start": v(706, -1458) * mm, "end": v(756, -1458) * mm});
            skLineSegment(sketch, "E10.9.13.26", {"start": v(706, -1408) * mm, "end": v(706, -1458) * mm});
            skLineSegment(sketch, "E10.0.14.26", {"start": v(760, -1408) * mm, "end": v(810, -1408) * mm});
            skLineSegment(sketch, "E10.3.14.26", {"start": v(810, -1408) * mm, "end": v(810, -1458) * mm});
            skLineSegment(sketch, "E10.6.14.26", {"start": v(760, -1458) * mm, "end": v(810, -1458) * mm});
            skLineSegment(sketch, "E10.9.14.26", {"start": v(760, -1408) * mm, "end": v(760, -1458) * mm});
            skSolve(sketch);
        }
        {
            var Q0;
            Q0 = qSketchRegion(id + "F0", true);
            extrude(context, id + "F1", {"entities" : qUnion([Q0]), "depth" : 4 * mm, "offsetDistance" : 25 * mm});
        }
        {
            var Q0;
            Q0=qCreatedBy(makeId("Front.planeOp"),FACE);
            var sketch = newSketch(context, id + "F2", { "sketchPlane" : qUnion([Q0])});
            skLineSegment(sketch, "E11.0", {"start": v(0, 0) * mm, "end": v(0, -1465) * mm});
            skLineSegment(sketch, "E12.0", {"start": v(0, 0) * mm, "end": v(815, 0) * mm});
            skLineSegment(sketch, "E13.0", {"start": v(815, 0) * mm, "end": v(815, -1465) * mm});
            skLineSegment(sketch, "E14.0", {"start": v(0, -1465) * mm, "end": v(815, -1465) * mm});
            skLineSegment(sketch, "E15.bottom", {"start": v(788, -27.1) * mm, "end": v(27, -27.1) * mm});
            skLineSegment(sketch, "E15.top", {"start": v(788, -1467) * mm, "end": v(27, -1467) * mm});
            skLineSegment(sketch, "E15.left", {"start": v(788, -27.1) * mm, "end": v(788, -1467) * mm});
            skLineSegment(sketch, "E15.right", {"start": v(27, -27.1) * mm, "end": v(27, -1467) * mm});
            skLineSegment(sketch, "E16", {"start": v(788, -27.1) * mm, "end": v(818, 2.9) * mm});
            skLineSegment(sketch, "E17", {"start": v(818, 2.9) * mm, "end": v(-3, 2.9) * mm});
            skLineSegment(sketch, "E18", {"start": v(-3, 2.9) * mm, "end": v(27, -27.1) * mm});
            skLineSegment(sketch, "E19", {"start": v(-1.5, 1.4) * mm, "end": v(816.5, 1.4) * mm});
            skLineSegment(sketch, "E20", {"start": v(818, 2.9) * mm, "end": v(816.5, -1467) * mm});
            skLineSegment(sketch, "E21", {"start": v(816.5, -1467) * mm, "end": v(788, -1467) * mm});
            skLineSegment(sketch, "E22", {"start": v(-3, 2.9) * mm, "end": v(-3, -1467) * mm});
            skLineSegment(sketch, "E23", {"start": v(27, -1467) * mm, "end": v(-3, -1467) * mm});
            skLineSegment(sketch, "E24", {"start": v(-1.5, 1.4) * mm, "end": v(-1.5, -1467) * mm});
            skLineSegment(sketch, "E25", {"start": v(816.5, 1.4) * mm, "end": v(815, -1467) * mm});
            skSolve(sketch);
        }
        {
            var Q0;
            {var subQ0=sQuery(id+"F2.wireOp",EDGE,"E14.0");var subQ1=sQuery(id+"F2.wireOp",EDGE,"E13.0");var subQ2=makeQuery(id+"F2.imprint","INTERSECT",VERTEX,{"derivedFrom":[subQ1,subQ0]});Q0=makeQuery(id+"F2.imprint","IMPRINT",FACE,{"disambiguationData":[TD([[makeQuery(id+"F2.imprint","IMPRINT",EDGE,{"disambiguationData":[TD([[subQ2,1.0]])],"derivedFrom":subQ1}),-1.0]])]});}
            var Q1;
            {var subQ2=sQuery(id+"F2.wireOp",EDGE,"E12.0");Q1=makeQuery(id+"F2.imprint","IMPRINT",FACE,{"disambiguationData":[TD([[makeQuery(id+"F2.imprint","IMPRINT",EDGE,{"derivedFrom":subQ2}),-1.0]])]});}
            var Q2;
            {var subQ0=sQuery(id+"F2.wireOp",EDGE,"E14.0");var subQ1=sQuery(id+"F2.wireOp",EDGE,"E11.0");var subQ2=makeQuery(id+"F2.imprint","INTERSECT",VERTEX,{"derivedFrom":[subQ1,subQ0]});Q2=makeQuery(id+"F2.imprint","IMPRINT",FACE,{"disambiguationData":[TD([[makeQuery(id+"F2.imprint","IMPRINT",EDGE,{"disambiguationData":[TD([[subQ2,1.0]])],"derivedFrom":subQ1}),1.0]])]});}
            var Q3;
            {var subQ0=sQuery(id+"F2.wireOp",EDGE,"E25");Q3=makeQuery(id+"F2.imprint","IMPRINT",FACE,{"disambiguationData":[TD([[makeQuery(id+"F2.imprint","IMPRINT",EDGE,{"derivedFrom":subQ0}),-1.0]])]});}
            var Q4;
            {var subQ0=sQuery(id+"F2.wireOp",EDGE,"E20");Q4=makeQuery(id+"F2.imprint","IMPRINT",FACE,{"disambiguationData":[TD([[makeQuery(id+"F2.imprint","IMPRINT",EDGE,{"derivedFrom":subQ0}),-1.0]])]});}
            var Q5;
            {var subQ0=sQuery(id+"F2.wireOp",EDGE,"E24");Q5=makeQuery(id+"F2.imprint","IMPRINT",FACE,{"disambiguationData":[TD([[makeQuery(id+"F2.imprint","IMPRINT",EDGE,{"derivedFrom":subQ0}),1.0]])]});}
            var Q6;
            {var subQ0=sQuery(id+"F2.wireOp",EDGE,"E22");Q6=makeQuery(id+"F2.imprint","IMPRINT",FACE,{"disambiguationData":[TD([[makeQuery(id+"F2.imprint","IMPRINT",EDGE,{"derivedFrom":subQ0}),1.0]])]});}
            var Q7;
            {var subQ1=sQuery(id+"F2.wireOp",EDGE,"E12.0");Q7=makeQuery(id+"F2.imprint","IMPRINT",FACE,{"disambiguationData":[TD([[makeQuery(id+"F2.imprint","IMPRINT",EDGE,{"derivedFrom":subQ1}),1.0]])]});}
            var Q8;
            {var subQ0=sQuery(id+"F2.wireOp",EDGE,"E17");Q8=makeQuery(id+"F2.imprint","IMPRINT",FACE,{"disambiguationData":[TD([[makeQuery(id+"F2.imprint","IMPRINT",EDGE,{"derivedFrom":subQ0}),1.0]])]});}
            extrude(context, id + "F3", {"entities" : qUnion([Q0, Q1, Q2, Q3, Q4, Q5, Q6, Q7, Q8]), "oppositeDirection" : true, "depth" : 1.5 * mm, "offsetDistance" : 25 * mm});
        }
        {
            var Q0;
            {var subQ0=sQuery(id+"F2.wireOp",EDGE,"E22");Q0=makeQuery(id+"F2.imprint","IMPRINT",FACE,{"disambiguationData":[TD([[makeQuery(id+"F2.imprint","IMPRINT",EDGE,{"derivedFrom":subQ0}),1.0]])]});}
            var Q1;
            {var subQ0=sQuery(id+"F2.wireOp",EDGE,"E20");Q1=makeQuery(id+"F2.imprint","IMPRINT",FACE,{"disambiguationData":[TD([[makeQuery(id+"F2.imprint","IMPRINT",EDGE,{"derivedFrom":subQ0}),-1.0]])]});}
            extrude(context, id + "F4", {"entities" : qUnion([Q0, Q1]), "operationType" : NewBodyOperationType.ADD, "depth" : 30 * mm, "offsetDistance" : 25 * mm});
        }
    });
